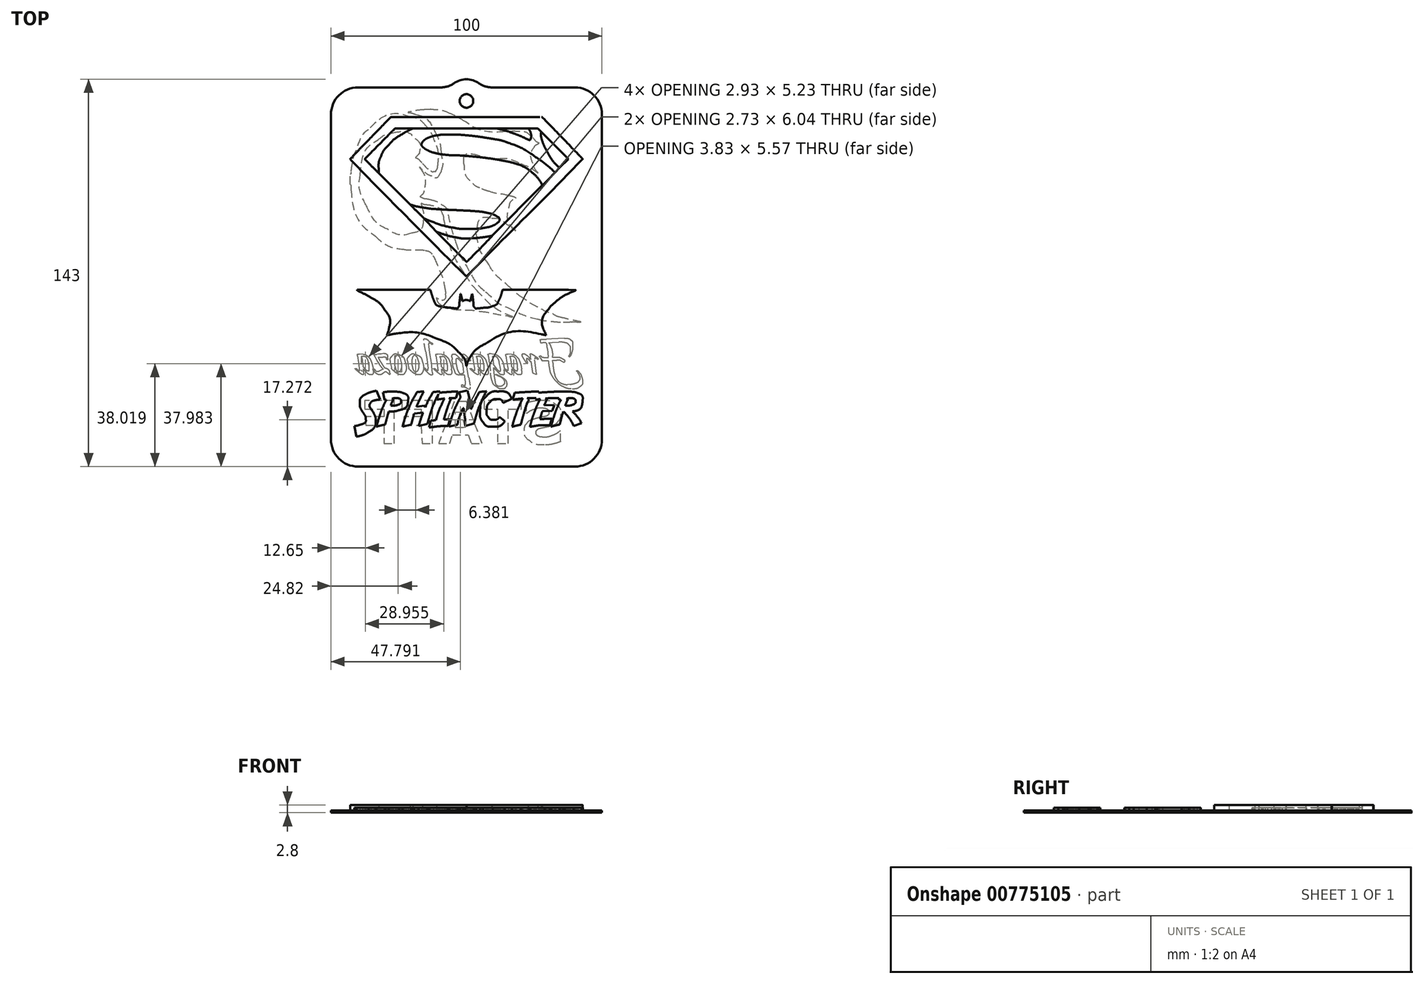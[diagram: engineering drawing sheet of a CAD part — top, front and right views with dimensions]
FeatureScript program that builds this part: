
annotation { "Feature Type Name" : "Feature", "Feature Type Description" : "" }
export const myFeature = defineFeature(function(context is Context, id is Id, definition is map)
    precondition{}
    {
        {
            var Q0;
            Q0=qCreatedBy(makeId("Top.planeOp"),FACE);
            var sketch = newSketch(context, id + "F0", { "sketchPlane" : qUnion([Q0])});
            skLineSegment(sketch, "E0.bottom", {"start": v(-40, 70) * mm, "end": v(-9.33, 70) * mm});
            skLineSegment(sketch, "E0.top", {"start": v(-40, -70) * mm, "end": v(40, -70) * mm});
            skLineSegment(sketch, "E0.left", {"start": v(-50, 60) * mm, "end": v(-50, -60) * mm});
            skLineSegment(sketch, "E0.right", {"start": v(50, 60) * mm, "end": v(50, -60) * mm});
            skPoint(sketch, "E0.middle", {"position": v(0, 0) * mm});
            skCircle(sketch, "E1", {"center": v(0, 65) * mm, "radius": 2.5 * mm});
            skPoint(sketch, "E2.visualSharp", {"position": v(-50, 70) * mm});
            skArc(sketch, "E2.filletArc", {"start": v(-40, 70) * mm, "mid": v(-47.07, 67.07) * mm, "end": v(-50, 60) * mm});
            skPoint(sketch, "E3.visualSharp", {"position": v(50, 70) * mm});
            skArc(sketch, "E3.filletArc", {"start": v(50, 60) * mm, "mid": v(47.07, 67.07) * mm, "end": v(40, 70) * mm});
            skPoint(sketch, "E4.visualSharp", {"position": v(50, -70) * mm});
            skArc(sketch, "E4.filletArc", {"start": v(40, -70) * mm, "mid": v(47.07, -67.07) * mm, "end": v(50, -60) * mm});
            skPoint(sketch, "E5.visualSharp", {"position": v(-50, -70) * mm});
            skArc(sketch, "E5.filletArc", {"start": v(-50, -60) * mm, "mid": v(-47.07, -67.07) * mm, "end": v(-40, -70) * mm});
            skArc(sketch, "E6", {"start": v(-4.66, 71.5) * mm, "mid": v(0, 73) * mm, "end": v(4.66, 71.5) * mm});
            skArc(sketch, "E7.filletArc", {"start": v(-9.33, 70) * mm, "mid": v(-6.88, 70.38) * mm, "end": v(-4.66, 71.5) * mm});
            skLineSegment(sketch, "E8", {"start": v(40, 70) * mm, "end": v(9.33, 70) * mm});
            skArc(sketch, "E9.filletArc", {"start": v(4.66, 71.5) * mm, "mid": v(6.88, 70.38) * mm, "end": v(9.33, 70) * mm});
            skSolve(sketch);
        }
        {
            var Q0;
            Q0=qCreatedBy(makeId("Top.planeOp"),FACE);
            var sketch = newSketch(context, id + "F1", { "sketchPlane" : qUnion([Q0])});
            skLineSegment(sketch, "E10", {"start": v(38.17, -16.7) * mm, "end": v(38.78, -16.7) * mm});
            skLineSegment(sketch, "E11", {"start": v(-13.07, 61.96) * mm, "end": v(-13.17, 61.96) * mm});
            skLineSegment(sketch, "E12", {"start": v(-14.17, 61.96) * mm, "end": v(-14.37, 61.96) * mm});
            skLineSegment(sketch, "E13", {"start": v(-42.85, 37.93) * mm, "end": v(-42.85, 36.81) * mm});
            skLineSegment(sketch, "E14", {"start": v(-42.85, 35.49) * mm, "end": v(-42.85, 34.98) * mm});
            skLineSegment(sketch, "E15", {"start": v(-42.85, 34.78) * mm, "end": v(-42.85, 34.16) * mm});
            skLineSegment(sketch, "E16", {"start": v(40.64, -16.7) * mm, "end": v(40.63, -16.62) * mm});
            skLineSegment(sketch, "E17", {"start": v(38.83, -16.7) * mm, "end": v(40.64, -16.7) * mm});
            skLineSegment(sketch, "E18", {"start": v(-42.85, 36.81) * mm, "end": v(-42.85, 35.49) * mm});
            skLineSegment(sketch, "E19", {"start": v(-13.21, 61.96) * mm, "end": v(-14.22, 61.96) * mm});
            skLineSegment(sketch, "E20", {"start": v(-42.85, 34.98) * mm, "end": v(-42.85, 34.77) * mm});
            skLineSegment(sketch, "E21", {"start": v(36.03, -31.52) * mm, "end": v(35.01, -30.98) * mm});
            skLineSegment(sketch, "E22", {"start": v(33.37, -30.7) * mm, "end": v(32.17, -30.75) * mm});
            skLineSegment(sketch, "E23", {"start": v(32.17, -30.75) * mm, "end": v(30.92, -30.82) * mm});
            skLineSegment(sketch, "E24", {"start": v(30.92, -30.82) * mm, "end": v(27.9, -30.82) * mm});
            skLineSegment(sketch, "E25", {"start": v(27.9, -30.82) * mm, "end": v(27.52, -30.26) * mm});
            skLineSegment(sketch, "E26", {"start": v(26.88, -29.35) * mm, "end": v(26.9, -29.28) * mm});
            skLineSegment(sketch, "E27", {"start": v(30.32, -29.76) * mm, "end": v(31.57, -29.76) * mm});
            skLineSegment(sketch, "E28", {"start": v(31.57, -29.76) * mm, "end": v(33.15, -29.76) * mm});
            skLineSegment(sketch, "E29", {"start": v(33.15, -29.76) * mm, "end": v(34.41, -29.76) * mm});
            skLineSegment(sketch, "E30", {"start": v(34.05, -24.06) * mm, "end": v(31.6, -24.16) * mm});
            skLineSegment(sketch, "E31", {"start": v(31.6, -24.16) * mm, "end": v(29.36, -24.3) * mm});
            skLineSegment(sketch, "E32", {"start": v(27.3, -24.39) * mm, "end": v(27.09, -23.13) * mm});
            skLineSegment(sketch, "E33", {"start": v(29.45, -22.97) * mm, "end": v(31.35, -22.93) * mm});
            skLineSegment(sketch, "E34", {"start": v(31.35, -22.93) * mm, "end": v(33.78, -22.78) * mm});
            skLineSegment(sketch, "E35", {"start": v(33.78, -22.78) * mm, "end": v(36.14, -22.66) * mm});
            skLineSegment(sketch, "E36", {"start": v(38.04, -29.5) * mm, "end": v(37.7, -29.32) * mm});
            skLineSegment(sketch, "E37", {"start": v(30.25, -30.2) * mm, "end": v(29.88, -26.54) * mm});
            skLineSegment(sketch, "E38", {"start": v(29.55, -24.56) * mm, "end": v(29.3, -24.3) * mm});
            skLineSegment(sketch, "E39", {"start": v(29.18, -23.96) * mm, "end": v(29.55, -24.04) * mm});
            skLineSegment(sketch, "E40", {"start": v(31.76, -29.06) * mm, "end": v(31.88, -31.82) * mm});
            skLineSegment(sketch, "E41", {"start": v(37.27, -39.71) * mm, "end": v(38.3, -39.63) * mm});
            skLineSegment(sketch, "E42", {"start": v(41.15, -35.4) * mm, "end": v(40.78, -34.92) * mm});
            skLineSegment(sketch, "E43", {"start": v(40.78, -34.92) * mm, "end": v(40.72, -34.76) * mm});
            skLineSegment(sketch, "E44", {"start": v(23.56, -29.53) * mm, "end": v(23.5, -28.89) * mm});
            skLineSegment(sketch, "E45", {"start": v(24.23, -28.54) * mm, "end": v(25.22, -29.23) * mm});
            skLineSegment(sketch, "E46", {"start": v(25.22, -29.23) * mm, "end": v(26.33, -30.01) * mm});
            skLineSegment(sketch, "E47", {"start": v(26.48, -30.3) * mm, "end": v(26.4, -30.34) * mm});
            skLineSegment(sketch, "E48", {"start": v(26.4, -30.34) * mm, "end": v(26.3, -30.32) * mm});
            skLineSegment(sketch, "E49", {"start": v(26.3, -30.32) * mm, "end": v(26.17, -30.3) * mm});
            skLineSegment(sketch, "E50", {"start": v(25.15, -30.3) * mm, "end": v(25.53, -33.54) * mm});
            skLineSegment(sketch, "E51", {"start": v(25.53, -33.54) * mm, "end": v(25.79, -35.64) * mm});
            skLineSegment(sketch, "E52", {"start": v(25.88, -36) * mm, "end": v(24.4, -35.44) * mm});
            skLineSegment(sketch, "E53", {"start": v(23.19, -29.85) * mm, "end": v(23.89, -30.75) * mm});
            skLineSegment(sketch, "E54", {"start": v(23.65, -31.18) * mm, "end": v(23.19, -30.77) * mm});
            skLineSegment(sketch, "E55", {"start": v(15.9, -29.4) * mm, "end": v(15.4, -29.4) * mm});
            skLineSegment(sketch, "E56", {"start": v(15.4, -29.4) * mm, "end": v(15.02, -29.33) * mm});
            skLineSegment(sketch, "E57", {"start": v(15.24, -28.42) * mm, "end": v(16.71, -28.55) * mm});
            skLineSegment(sketch, "E58", {"start": v(17.3, -34.56) * mm, "end": v(16.63, -33.84) * mm});
            skLineSegment(sketch, "E59", {"start": v(16.01, -32.3) * mm, "end": v(16.46, -32.84) * mm});
            skLineSegment(sketch, "E60", {"start": v(16.96, -29.4) * mm, "end": v(16.5, -29.4) * mm});
            skLineSegment(sketch, "E61", {"start": v(16.5, -29.4) * mm, "end": v(15.9, -29.4) * mm});
            skLineSegment(sketch, "E62", {"start": v(16.38, -31.1) * mm, "end": v(16.6, -32.79) * mm});
            skLineSegment(sketch, "E63", {"start": v(16.6, -32.79) * mm, "end": v(16.8, -34.4) * mm});
            skLineSegment(sketch, "E64", {"start": v(16.8, -34.4) * mm, "end": v(16.85, -35.3) * mm});
            skLineSegment(sketch, "E65", {"start": v(14.85, -34.45) * mm, "end": v(15.26, -34.75) * mm});
            skLineSegment(sketch, "E66", {"start": v(15.33, -34.51) * mm, "end": v(15.26, -33.72) * mm});
            skLineSegment(sketch, "E67", {"start": v(15.26, -33.72) * mm, "end": v(14.93, -31.64) * mm});
            skLineSegment(sketch, "E68", {"start": v(14.93, -31.64) * mm, "end": v(14.54, -29.14) * mm});
            skLineSegment(sketch, "E69", {"start": v(9.13, -29.4) * mm, "end": v(8.63, -29.4) * mm});
            skLineSegment(sketch, "E70", {"start": v(8.63, -29.4) * mm, "end": v(8.27, -29.31) * mm});
            skLineSegment(sketch, "E71", {"start": v(8.04, -29.08) * mm, "end": v(7.89, -28.74) * mm});
            skLineSegment(sketch, "E72", {"start": v(8.47, -28.35) * mm, "end": v(8.95, -28.35) * mm});
            skLineSegment(sketch, "E73", {"start": v(8.95, -28.35) * mm, "end": v(9.46, -28.52) * mm});
            skLineSegment(sketch, "E74", {"start": v(9.46, -28.52) * mm, "end": v(10.14, -28.6) * mm});
            skLineSegment(sketch, "E75", {"start": v(11.28, -34.74) * mm, "end": v(10.47, -33.88) * mm});
            skLineSegment(sketch, "E76", {"start": v(9.69, -32.05) * mm, "end": v(10.37, -32.95) * mm});
            skLineSegment(sketch, "E77", {"start": v(10.37, -32.95) * mm, "end": v(11.14, -33.94) * mm});
            skLineSegment(sketch, "E78", {"start": v(12.6, -34.13) * mm, "end": v(12.52, -33.32) * mm});
            skLineSegment(sketch, "E79", {"start": v(12.52, -33.32) * mm, "end": v(12.29, -32.26) * mm});
            skLineSegment(sketch, "E80", {"start": v(12.29, -32.26) * mm, "end": v(12.13, -31.6) * mm});
            skLineSegment(sketch, "E81", {"start": v(10.33, -29.4) * mm, "end": v(9.77, -29.4) * mm});
            skLineSegment(sketch, "E82", {"start": v(9.77, -29.4) * mm, "end": v(9.13, -29.4) * mm});
            skLineSegment(sketch, "E83", {"start": v(9.46, -28.84) * mm, "end": v(9.77, -30.97) * mm});
            skLineSegment(sketch, "E84", {"start": v(9.77, -30.97) * mm, "end": v(10.1, -34.04) * mm});
            skLineSegment(sketch, "E85", {"start": v(10.1, -34.04) * mm, "end": v(10.34, -36.29) * mm});
            skLineSegment(sketch, "E86", {"start": v(10.34, -36.29) * mm, "end": v(10.47, -37.68) * mm});
            skLineSegment(sketch, "E87", {"start": v(12.25, -36.7) * mm, "end": v(11.22, -36.28) * mm});
            skLineSegment(sketch, "E88", {"start": v(10.66, -36) * mm, "end": v(10.7, -35.94) * mm});
            skLineSegment(sketch, "E89", {"start": v(8.88, -35.3) * mm, "end": v(8.5, -31.75) * mm});
            skLineSegment(sketch, "E90", {"start": v(3.54, -29.4) * mm, "end": v(3.04, -29.4) * mm});
            skLineSegment(sketch, "E91", {"start": v(3.04, -29.4) * mm, "end": v(2.67, -29.33) * mm});
            skLineSegment(sketch, "E92", {"start": v(2.88, -28.42) * mm, "end": v(4.36, -28.55) * mm});
            skLineSegment(sketch, "E93", {"start": v(4.94, -34.56) * mm, "end": v(4.28, -33.84) * mm});
            skLineSegment(sketch, "E94", {"start": v(3.66, -32.3) * mm, "end": v(4.1, -32.84) * mm});
            skLineSegment(sketch, "E95", {"start": v(4.6, -29.4) * mm, "end": v(4.14, -29.4) * mm});
            skLineSegment(sketch, "E96", {"start": v(4.14, -29.4) * mm, "end": v(3.54, -29.4) * mm});
            skLineSegment(sketch, "E97", {"start": v(4.02, -31.1) * mm, "end": v(4.25, -32.79) * mm});
            skLineSegment(sketch, "E98", {"start": v(4.25, -32.79) * mm, "end": v(4.44, -34.4) * mm});
            skLineSegment(sketch, "E99", {"start": v(4.44, -34.4) * mm, "end": v(4.5, -35.3) * mm});
            skLineSegment(sketch, "E100", {"start": v(2.5, -34.45) * mm, "end": v(2.9, -34.75) * mm});
            skLineSegment(sketch, "E101", {"start": v(2.98, -34.51) * mm, "end": v(2.9, -33.72) * mm});
            skLineSegment(sketch, "E102", {"start": v(2.9, -33.72) * mm, "end": v(2.58, -31.64) * mm});
            skLineSegment(sketch, "E103", {"start": v(2.58, -31.64) * mm, "end": v(2.19, -29.14) * mm});
            skLineSegment(sketch, "E104", {"start": v(-0.07, -30.77) * mm, "end": v(0.03, -32.01) * mm});
            skLineSegment(sketch, "E105", {"start": v(0.03, -32.01) * mm, "end": v(0.35, -34.14) * mm});
            skLineSegment(sketch, "E106", {"start": v(0.35, -34.14) * mm, "end": v(0.85, -37.11) * mm});
            skLineSegment(sketch, "E107", {"start": v(0.96, -41.4) * mm, "end": v(0.32, -41.16) * mm});
            skLineSegment(sketch, "E108", {"start": v(-0.43, -39.67) * mm, "end": v(-0.47, -38.83) * mm});
            skLineSegment(sketch, "E109", {"start": v(-0.47, -38.83) * mm, "end": v(-0.77, -36.7) * mm});
            skLineSegment(sketch, "E110", {"start": v(-0.77, -36.7) * mm, "end": v(-1.14, -33.74) * mm});
            skLineSegment(sketch, "E111", {"start": v(-1.14, -33.74) * mm, "end": v(-1.34, -32.16) * mm});
            skLineSegment(sketch, "E112", {"start": v(-1.34, -32.16) * mm, "end": v(-1.56, -30.34) * mm});
            skLineSegment(sketch, "E113", {"start": v(-1.56, -30.34) * mm, "end": v(-1.62, -29.37) * mm});
            skLineSegment(sketch, "E114", {"start": v(-0.41, -35.45) * mm, "end": v(-0.36, -35.65) * mm});
            skLineSegment(sketch, "E115", {"start": v(-0.18, -36.1) * mm, "end": v(-0.24, -36.16) * mm});
            skLineSegment(sketch, "E116", {"start": v(-0.24, -36.16) * mm, "end": v(-0.31, -36.19) * mm});
            skLineSegment(sketch, "E117", {"start": v(-0.31, -36.19) * mm, "end": v(-0.7, -36.11) * mm});
            skLineSegment(sketch, "E118", {"start": v(-0.7, -36.11) * mm, "end": v(-1.4, -36.11) * mm});
            skLineSegment(sketch, "E119", {"start": v(-1.4, -36.11) * mm, "end": v(-2.27, -36.11) * mm});
            skLineSegment(sketch, "E120", {"start": v(-2.53, -30.03) * mm, "end": v(-1.85, -30.67) * mm});
            skLineSegment(sketch, "E121", {"start": v(-9.94, -29.4) * mm, "end": v(-10.44, -29.4) * mm});
            skLineSegment(sketch, "E122", {"start": v(-10.44, -29.4) * mm, "end": v(-10.8, -29.33) * mm});
            skLineSegment(sketch, "E123", {"start": v(-10.6, -28.42) * mm, "end": v(-9.12, -28.55) * mm});
            skLineSegment(sketch, "E124", {"start": v(-8.54, -34.56) * mm, "end": v(-9.2, -33.84) * mm});
            skLineSegment(sketch, "E125", {"start": v(-9.82, -32.3) * mm, "end": v(-9.37, -32.84) * mm});
            skLineSegment(sketch, "E126", {"start": v(-8.87, -29.4) * mm, "end": v(-9.34, -29.4) * mm});
            skLineSegment(sketch, "E127", {"start": v(-9.34, -29.4) * mm, "end": v(-9.94, -29.4) * mm});
            skLineSegment(sketch, "E128", {"start": v(-9.46, -31.1) * mm, "end": v(-9.23, -32.79) * mm});
            skLineSegment(sketch, "E129", {"start": v(-9.23, -32.79) * mm, "end": v(-9.04, -34.4) * mm});
            skLineSegment(sketch, "E130", {"start": v(-9.04, -34.4) * mm, "end": v(-8.99, -35.3) * mm});
            skLineSegment(sketch, "E131", {"start": v(-10.98, -34.45) * mm, "end": v(-10.58, -34.75) * mm});
            skLineSegment(sketch, "E132", {"start": v(-10.5, -34.51) * mm, "end": v(-10.58, -33.72) * mm});
            skLineSegment(sketch, "E133", {"start": v(-10.58, -33.72) * mm, "end": v(-10.9, -31.64) * mm});
            skLineSegment(sketch, "E134", {"start": v(-10.9, -31.64) * mm, "end": v(-11.29, -29.14) * mm});
            skLineSegment(sketch, "E135", {"start": v(-14.16, -33.74) * mm, "end": v(-14.26, -32.52) * mm});
            skLineSegment(sketch, "E136", {"start": v(-14.26, -32.52) * mm, "end": v(-14.56, -30.46) * mm});
            skLineSegment(sketch, "E137", {"start": v(-14.56, -30.46) * mm, "end": v(-15.08, -27.43) * mm});
            skLineSegment(sketch, "E138", {"start": v(-15, -22.92) * mm, "end": v(-14.03, -23.56) * mm});
            skLineSegment(sketch, "E139", {"start": v(-12.63, -24.87) * mm, "end": v(-12.86, -24.8) * mm});
            skLineSegment(sketch, "E140", {"start": v(-13.91, -24.76) * mm, "end": v(-13.85, -25.5) * mm});
            skLineSegment(sketch, "E141", {"start": v(-13.85, -25.5) * mm, "end": v(-13.65, -26.9) * mm});
            skLineSegment(sketch, "E142", {"start": v(-13.65, -26.9) * mm, "end": v(-13.36, -28.73) * mm});
            skLineSegment(sketch, "E143", {"start": v(-13.36, -28.73) * mm, "end": v(-13.08, -30.79) * mm});
            skLineSegment(sketch, "E144", {"start": v(-13.08, -30.79) * mm, "end": v(-12.8, -32.84) * mm});
            skLineSegment(sketch, "E145", {"start": v(-12.8, -32.84) * mm, "end": v(-12.61, -34.45) * mm});
            skLineSegment(sketch, "E146", {"start": v(-12.61, -34.45) * mm, "end": v(-12.55, -35.39) * mm});
            skLineSegment(sketch, "E147", {"start": v(-19.13, -35.54) * mm, "end": v(-20.12, -34.9) * mm});
            skLineSegment(sketch, "E148", {"start": v(-21.26, -33.55) * mm, "end": v(-21.5, -32.5) * mm});
            skLineSegment(sketch, "E149", {"start": v(-21.5, -32.5) * mm, "end": v(-21.73, -31.52) * mm});
            skLineSegment(sketch, "E150", {"start": v(-21.73, -31.52) * mm, "end": v(-21.79, -30.84) * mm});
            skLineSegment(sketch, "E151", {"start": v(-19.8, -28.37) * mm, "end": v(-19.36, -28.42) * mm});
            skLineSegment(sketch, "E152", {"start": v(-19.36, -28.42) * mm, "end": v(-18.37, -28.75) * mm});
            skLineSegment(sketch, "E153", {"start": v(-17.54, -31.66) * mm, "end": v(-18, -30.05) * mm});
            skLineSegment(sketch, "E154", {"start": v(-25.5, -35.54) * mm, "end": v(-26.5, -34.9) * mm});
            skLineSegment(sketch, "E155", {"start": v(-27.64, -33.55) * mm, "end": v(-27.88, -32.5) * mm});
            skLineSegment(sketch, "E156", {"start": v(-27.88, -32.5) * mm, "end": v(-28.1, -31.52) * mm});
            skLineSegment(sketch, "E157", {"start": v(-28.1, -31.52) * mm, "end": v(-28.17, -30.84) * mm});
            skLineSegment(sketch, "E158", {"start": v(-26.19, -28.37) * mm, "end": v(-25.74, -28.42) * mm});
            skLineSegment(sketch, "E159", {"start": v(-25.74, -28.42) * mm, "end": v(-24.75, -28.75) * mm});
            skLineSegment(sketch, "E160", {"start": v(-23.92, -31.66) * mm, "end": v(-24.38, -30.05) * mm});
            skLineSegment(sketch, "E161", {"start": v(-30.82, -29.63) * mm, "end": v(-31.6, -29.66) * mm});
            skLineSegment(sketch, "E162", {"start": v(-31.6, -29.66) * mm, "end": v(-32.28, -29.63) * mm});
            skLineSegment(sketch, "E163", {"start": v(-32.28, -29.63) * mm, "end": v(-32.6, -29.59) * mm});
            skLineSegment(sketch, "E164", {"start": v(-28.05, -35.7) * mm, "end": v(-28.34, -36) * mm});
            skLineSegment(sketch, "E165", {"start": v(-32.16, -32.19) * mm, "end": v(-32.67, -31.4) * mm});
            skLineSegment(sketch, "E166", {"start": v(-32.67, -31.4) * mm, "end": v(-33.23, -30.44) * mm});
            skLineSegment(sketch, "E167", {"start": v(-33.23, -30.44) * mm, "end": v(-33.8, -29.45) * mm});
            skLineSegment(sketch, "E168", {"start": v(-33.8, -29.45) * mm, "end": v(-34.28, -28.64) * mm});
            skLineSegment(sketch, "E169", {"start": v(-34.18, -28.33) * mm, "end": v(-34.02, -28.38) * mm});
            skLineSegment(sketch, "E170", {"start": v(-33.17, -28.56) * mm, "end": v(-32.43, -28.52) * mm});
            skLineSegment(sketch, "E171", {"start": v(-32.43, -28.52) * mm, "end": v(-31.52, -28.4) * mm});
            skLineSegment(sketch, "E172", {"start": v(-31.52, -28.4) * mm, "end": v(-30.4, -28.23) * mm});
            skLineSegment(sketch, "E173", {"start": v(-29.1, -29.33) * mm, "end": v(-29.02, -30) * mm});
            skLineSegment(sketch, "E174", {"start": v(-28.09, -35.68) * mm, "end": v(-28.22, -35.85) * mm});
            skLineSegment(sketch, "E175", {"start": v(-28.4, -35.95) * mm, "end": v(-29.27, -35.27) * mm});
            skLineSegment(sketch, "E176", {"start": v(-32.12, -34.67) * mm, "end": v(-31.13, -34.22) * mm});
            skLineSegment(sketch, "E177", {"start": v(-31.13, -34.22) * mm, "end": v(-30.22, -33.8) * mm});
            skLineSegment(sketch, "E178", {"start": v(-28.36, -35.08) * mm, "end": v(-28.32, -35.29) * mm});
            skLineSegment(sketch, "E179", {"start": v(-28.32, -35.29) * mm, "end": v(-28.26, -35.48) * mm});
            skLineSegment(sketch, "E180", {"start": v(-28.26, -35.48) * mm, "end": v(-28.09, -35.68) * mm});
            skLineSegment(sketch, "E181", {"start": v(-38.9, -29.4) * mm, "end": v(-39.4, -29.4) * mm});
            skLineSegment(sketch, "E182", {"start": v(-39.4, -29.4) * mm, "end": v(-39.76, -29.33) * mm});
            skLineSegment(sketch, "E183", {"start": v(-39.55, -28.42) * mm, "end": v(-38.08, -28.55) * mm});
            skLineSegment(sketch, "E184", {"start": v(-37.5, -34.56) * mm, "end": v(-38.15, -33.84) * mm});
            skLineSegment(sketch, "E185", {"start": v(-38.77, -32.3) * mm, "end": v(-38.33, -32.84) * mm});
            skLineSegment(sketch, "E186", {"start": v(-37.82, -29.4) * mm, "end": v(-38.3, -29.4) * mm});
            skLineSegment(sketch, "E187", {"start": v(-38.3, -29.4) * mm, "end": v(-38.9, -29.4) * mm});
            skLineSegment(sketch, "E188", {"start": v(-38.41, -31.1) * mm, "end": v(-38.19, -32.79) * mm});
            skLineSegment(sketch, "E189", {"start": v(-38.19, -32.79) * mm, "end": v(-38, -34.4) * mm});
            skLineSegment(sketch, "E190", {"start": v(-38, -34.4) * mm, "end": v(-37.94, -35.3) * mm});
            skLineSegment(sketch, "E191", {"start": v(-39.94, -34.45) * mm, "end": v(-39.53, -34.75) * mm});
            skLineSegment(sketch, "E192", {"start": v(-39.45, -34.51) * mm, "end": v(-39.53, -33.72) * mm});
            skLineSegment(sketch, "E193", {"start": v(-39.53, -33.72) * mm, "end": v(-39.86, -31.64) * mm});
            skLineSegment(sketch, "E194", {"start": v(-39.86, -31.64) * mm, "end": v(-40.24, -29.14) * mm});
            skLineSegment(sketch, "E195", {"start": v(22.49, -50.22) * mm, "end": v(22.06, -50.22) * mm});
            skLineSegment(sketch, "E196", {"start": v(22.06, -50.22) * mm, "end": v(22.06, -46.56) * mm});
            skLineSegment(sketch, "E197", {"start": v(34.32, -56.92) * mm, "end": v(34.76, -56.92) * mm});
            skLineSegment(sketch, "E198", {"start": v(34.76, -56.92) * mm, "end": v(34.76, -60.73) * mm});
            skLineSegment(sketch, "E199", {"start": v(6.54, -45.64) * mm, "end": v(20.3, -45.64) * mm});
            skLineSegment(sketch, "E200", {"start": v(20.3, -45.64) * mm, "end": v(20.3, -48.81) * mm});
            skLineSegment(sketch, "E201", {"start": v(20.3, -48.81) * mm, "end": v(15.36, -48.81) * mm});
            skLineSegment(sketch, "E202", {"start": v(15.36, -48.81) * mm, "end": v(15.36, -61.51) * mm});
            skLineSegment(sketch, "E203", {"start": v(15.36, -61.51) * mm, "end": v(11.47, -61.51) * mm});
            skLineSegment(sketch, "E204", {"start": v(11.47, -61.51) * mm, "end": v(11.47, -48.81) * mm});
            skLineSegment(sketch, "E205", {"start": v(11.47, -48.81) * mm, "end": v(6.54, -48.81) * mm});
            skLineSegment(sketch, "E206", {"start": v(6.54, -48.81) * mm, "end": v(6.54, -45.64) * mm});
            skLineSegment(sketch, "E207", {"start": v(-4.56, -45.99) * mm, "end": v(0.04, -45.99) * mm});
            skLineSegment(sketch, "E208", {"start": v(0.04, -45.99) * mm, "end": v(5.78, -61.51) * mm});
            skLineSegment(sketch, "E209", {"start": v(5.78, -61.51) * mm, "end": v(1.8, -61.51) * mm});
            skLineSegment(sketch, "E210", {"start": v(1.8, -61.51) * mm, "end": v(0.7, -58.34) * mm});
            skLineSegment(sketch, "E211", {"start": v(0.7, -58.34) * mm, "end": v(-5.12, -58.34) * mm});
            skLineSegment(sketch, "E212", {"start": v(-5.12, -58.34) * mm, "end": v(-6.2, -61.51) * mm});
            skLineSegment(sketch, "E213", {"start": v(-6.2, -61.51) * mm, "end": v(-10.3, -61.51) * mm});
            skLineSegment(sketch, "E214", {"start": v(-10.3, -61.51) * mm, "end": v(-4.56, -45.99) * mm});
            skLineSegment(sketch, "E215", {"start": v(-0.3, -55.51) * mm, "end": v(-2.2, -49.94) * mm});
            skLineSegment(sketch, "E216", {"start": v(-2.2, -49.94) * mm, "end": v(-4.12, -55.51) * mm});
            skLineSegment(sketch, "E217", {"start": v(-4.12, -55.51) * mm, "end": v(-0.3, -55.51) * mm});
            skLineSegment(sketch, "E218", {"start": v(-23.8, -45.64) * mm, "end": v(-12.51, -45.64) * mm});
            skLineSegment(sketch, "E219", {"start": v(-12.51, -45.64) * mm, "end": v(-12.51, -61.51) * mm});
            skLineSegment(sketch, "E220", {"start": v(-12.51, -61.51) * mm, "end": v(-16.4, -61.51) * mm});
            skLineSegment(sketch, "E221", {"start": v(-16.4, -61.51) * mm, "end": v(-16.75, -54.8) * mm});
            skLineSegment(sketch, "E222", {"start": v(-16.75, -54.8) * mm, "end": v(-23.1, -54.8) * mm});
            skLineSegment(sketch, "E223", {"start": v(-23.1, -54.8) * mm, "end": v(-23.1, -51.63) * mm});
            skLineSegment(sketch, "E224", {"start": v(-23.1, -51.63) * mm, "end": v(-16.75, -51.63) * mm});
            skLineSegment(sketch, "E225", {"start": v(-16.75, -51.63) * mm, "end": v(-16.75, -48.81) * mm});
            skLineSegment(sketch, "E226", {"start": v(-16.75, -48.81) * mm, "end": v(-23.8, -48.81) * mm});
            skLineSegment(sketch, "E227", {"start": v(-23.8, -48.81) * mm, "end": v(-23.8, -45.64) * mm});
            skLineSegment(sketch, "E228", {"start": v(-37.56, -45.64) * mm, "end": v(-26.63, -45.64) * mm});
            skLineSegment(sketch, "E229", {"start": v(-26.63, -45.64) * mm, "end": v(-26.63, -61.51) * mm});
            skLineSegment(sketch, "E230", {"start": v(-26.63, -61.51) * mm, "end": v(-30.5, -61.51) * mm});
            skLineSegment(sketch, "E231", {"start": v(-30.5, -61.51) * mm, "end": v(-30.5, -54.8) * mm});
            skLineSegment(sketch, "E232", {"start": v(-30.5, -54.8) * mm, "end": v(-37.2, -54.8) * mm});
            skLineSegment(sketch, "E233", {"start": v(-37.2, -54.8) * mm, "end": v(-37.2, -51.63) * mm});
            skLineSegment(sketch, "E234", {"start": v(-37.2, -51.63) * mm, "end": v(-30.5, -51.63) * mm});
            skLineSegment(sketch, "E235", {"start": v(-30.5, -51.63) * mm, "end": v(-30.5, -48.81) * mm});
            skLineSegment(sketch, "E236", {"start": v(-30.5, -48.81) * mm, "end": v(-37.56, -48.81) * mm});
            skLineSegment(sketch, "E237", {"start": v(-37.56, -48.81) * mm, "end": v(-37.56, -45.64) * mm});
            skFitSpline(sketch, "E238", {"points": [v(-14.37, 61.96) * mm, v(-14.8, 61.78) * mm, v(-15.26, 61.8) * mm, v(-15.71, 61.76) * mm]});
            skFitSpline(sketch, "E239", {"points": [v(-15.71, 61.76) * mm, v(-17.53, 61.62) * mm, v(-19.32, 61.38) * mm, v(-21.1, 60.93) * mm]});
            skFitSpline(sketch, "E240", {"points": [v(-21.1, 60.93) * mm, v(-21.24, 60.9) * mm, v(-21.43, 60.9) * mm, v(-21.54, 60.66) * mm]});
            skFitSpline(sketch, "E241", {"points": [v(-21.54, 60.66) * mm, v(-20.54, 60.63) * mm, v(-19.62, 60.35) * mm, v(-18.7, 60.03) * mm]});
            skFitSpline(sketch, "E242", {"points": [v(-18.7, 60.03) * mm, v(-15.38, 58.87) * mm, v(-13.15, 56.52) * mm, v(-11.58, 53.44) * mm]});
            skFitSpline(sketch, "E243", {"points": [v(-11.58, 53.44) * mm, v(-10.47, 51.29) * mm, v(-9.71, 49) * mm, v(-9.41, 46.6) * mm]});
            skFitSpline(sketch, "E244", {"points": [v(-9.41, 46.6) * mm, v(-9.11, 44.15) * mm, v(-8.77, 41.68) * mm, v(-9.35, 39.2) * mm]});
            skFitSpline(sketch, "E245", {"points": [v(-9.35, 39.2) * mm, v(-9.4, 38.94) * mm, v(-9.5, 38.7) * mm, v(-9.63, 38.47) * mm]});
            skFitSpline(sketch, "E246", {"points": [v(-9.63, 38.47) * mm, v(-10.22, 37.39) * mm, v(-11.1, 36.57) * mm, v(-12.72, 37.2) * mm]});
            skFitSpline(sketch, "E247", {"points": [v(-12.72, 37.2) * mm, v(-14.12, 37.75) * mm, v(-15.28, 38.64) * mm, v(-16.36, 39.65) * mm]});
            skFitSpline(sketch, "E248", {"points": [v(-16.36, 39.65) * mm, v(-16.66, 39.92) * mm, v(-16.91, 40.23) * mm, v(-17.25, 40.59) * mm]});
            skFitSpline(sketch, "E249", {"points": [v(-17.25, 40.59) * mm, v(-17.26, 40.3) * mm, v(-17.11, 40.19) * mm, v(-17.03, 40.05) * mm]});
            skFitSpline(sketch, "E250", {"points": [v(-17.03, 40.05) * mm, v(-15.47, 37.53) * mm, v(-15.17, 34.78) * mm, v(-15.68, 31.91) * mm]});
            skFitSpline(sketch, "E251", {"points": [v(-15.68, 31.91) * mm, v(-15.8, 31.24) * mm, v(-16.1, 30.64) * mm, v(-16.6, 30.16) * mm]});
            skFitSpline(sketch, "E252", {"points": [v(-16.6, 30.16) * mm, v(-17.12, 29.67) * mm, v(-17.1, 29.65) * mm, v(-16.44, 29.37) * mm]});
            skFitSpline(sketch, "E253", {"points": [v(-16.44, 29.37) * mm, v(-15.51, 28.97) * mm, v(-14.51, 28.87) * mm, v(-13.54, 28.62) * mm]});
            skFitSpline(sketch, "E254", {"points": [v(-13.54, 28.62) * mm, v(-11.87, 28.2) * mm, v(-10.3, 27.56) * mm, v(-8.86, 26.56) * mm]});
            skFitSpline(sketch, "E255", {"points": [v(-8.86, 26.56) * mm, v(-7.66, 25.72) * mm, v(-7.05, 24.5) * mm, v(-6.77, 23.12) * mm]});
            skFitSpline(sketch, "E256", {"points": [v(-6.77, 23.12) * mm, v(-6.07, 19.68) * mm, v(-5.15, 16.3) * mm, v(-4.03, 13) * mm]});
            skFitSpline(sketch, "E257", {"points": [v(-4.03, 13) * mm, v(-3.06, 10.12) * mm, v(-1.94, 7.3) * mm, v(-0.43, 4.69) * mm]});
            skFitSpline(sketch, "E258", {"points": [v(-0.43, 4.69) * mm, v(1.68, 1.04) * mm, v(3.89, -2.54) * mm, v(7.02, -5.42) * mm]});
            skFitSpline(sketch, "E259", {"points": [v(7.02, -5.42) * mm, v(9.48, -7.68) * mm, v(12.02, -9.8) * mm, v(15.04, -11.25) * mm]});
            skFitSpline(sketch, "E260", {"points": [v(15.04, -11.25) * mm, v(18.76, -13.03) * mm, v(22.58, -14.59) * mm, v(26.59, -15.61) * mm]});
            skFitSpline(sketch, "E261", {"points": [v(26.59, -15.61) * mm, v(28.25, -16.04) * mm, v(29.96, -16.23) * mm, v(31.67, -16.4) * mm]});
            skFitSpline(sketch, "E262", {"points": [v(31.67, -16.4) * mm, v(33.03, -16.54) * mm, v(34.4, -16.62) * mm, v(35.77, -16.62) * mm]});
            skFitSpline(sketch, "E263", {"points": [v(35.77, -16.62) * mm, v(36.22, -16.7) * mm, v(36.67, -16.64) * mm, v(37.13, -16.66) * mm]});
            skFitSpline(sketch, "E264", {"points": [v(37.13, -16.66) * mm, v(37.48, -16.68) * mm, v(37.83, -16.6) * mm, v(38.17, -16.7) * mm]});
            skFitSpline(sketch, "E265", {"points": [v(38.78, -16.7) * mm, v(39.38, -16.6) * mm, v(39.99, -16.69) * mm, v(40.59, -16.66) * mm]});
            skFitSpline(sketch, "E266", {"points": [v(40.59, -16.66) * mm, v(41.03, -16.65) * mm, v(41.48, -16.66) * mm, v(41.92, -16.65) * mm]});
            skFitSpline(sketch, "E267", {"points": [v(41.92, -16.65) * mm, v(42.02, -16.65) * mm, v(42.17, -16.71) * mm, v(42.18, -16.52) * mm]});
            skFitSpline(sketch, "E268", {"points": [v(42.18, -16.52) * mm, v(40.35, -16.18) * mm, v(38.52, -15.83) * mm, v(36.71, -15.35) * mm]});
            skFitSpline(sketch, "E269", {"points": [v(36.71, -15.35) * mm, v(36, -15.16) * mm, v(35.25, -15.03) * mm, v(34.53, -14.82) * mm]});
            skFitSpline(sketch, "E270", {"points": [v(34.53, -14.82) * mm, v(33.1, -14.38) * mm, v(31.81, -13.6) * mm, v(30.4, -13.1) * mm]});
            skFitSpline(sketch, "E271", {"points": [v(30.4, -13.1) * mm, v(28.9, -12.57) * mm, v(27.54, -11.75) * mm, v(26.13, -11.04) * mm]});
            skFitSpline(sketch, "E272", {"points": [v(26.13, -11.04) * mm, v(24.28, -10.1) * mm, v(22.61, -8.9) * mm, v(20.9, -7.78) * mm]});
            skFitSpline(sketch, "E273", {"points": [v(20.9, -7.78) * mm, v(19.32, -6.73) * mm, v(17.87, -5.46) * mm, v(16.43, -4.2) * mm]});
            skFitSpline(sketch, "E274", {"points": [v(16.43, -4.2) * mm, v(13.43, -1.57) * mm, v(10.5, 1.14) * mm, v(8.29, 4.51) * mm]});
            skFitSpline(sketch, "E275", {"points": [v(8.29, 4.51) * mm, v(6.39, 7.4) * mm, v(4.75, 10.42) * mm, v(4.04, 13.87) * mm]});
            skFitSpline(sketch, "E276", {"points": [v(4.04, 13.87) * mm, v(3.74, 15.29) * mm, v(3.6, 16.77) * mm, v(3.96, 18.15) * mm]});
            skFitSpline(sketch, "E277", {"points": [v(3.96, 18.15) * mm, v(4.68, 20.94) * mm, v(6.59, 22.1) * mm, v(9.37, 21.76) * mm]});
            skFitSpline(sketch, "E278", {"points": [v(9.37, 21.76) * mm, v(12.14, 21.42) * mm, v(14.36, 19.9) * mm, v(16.53, 18.28) * mm]});
            skFitSpline(sketch, "E279", {"points": [v(16.53, 18.28) * mm, v(17.05, 17.9) * mm, v(17.55, 17.5) * mm, v(18.06, 17.1) * mm]});
            skFitSpline(sketch, "E280", {"points": [v(18.06, 17.1) * mm, v(18.14, 17.24) * mm, v(18.06, 17.27) * mm, v(18.02, 17.3) * mm]});
            skFitSpline(sketch, "E281", {"points": [v(18.02, 17.3) * mm, v(15.67, 19.8) * mm, v(15.1, 22.76) * mm, v(15.81, 26.03) * mm]});
            skFitSpline(sketch, "E282", {"points": [v(15.81, 26.03) * mm, v(16.12, 27.45) * mm, v(16.96, 28.48) * mm, v(18.36, 29.08) * mm]});
            skFitSpline(sketch, "E283", {"points": [v(18.36, 29.08) * mm, v(17.45, 29.57) * mm, v(16.52, 29.83) * mm, v(15.58, 30.04) * mm]});
            skFitSpline(sketch, "E284", {"points": [v(15.58, 30.04) * mm, v(13.22, 30.57) * mm, v(10.83, 30.9) * mm, v(8.5, 31.57) * mm]});
            skFitSpline(sketch, "E285", {"points": [v(8.5, 31.57) * mm, v(7.27, 31.92) * mm, v(6.07, 32.36) * mm, v(4.9, 32.88) * mm]});
            skFitSpline(sketch, "E286", {"points": [v(4.9, 32.88) * mm, v(3.5, 33.5) * mm, v(2.36, 34.42) * mm, v(1.34, 35.53) * mm]});
            skFitSpline(sketch, "E287", {"points": [v(1.34, 35.53) * mm, v(0.04, 36.96) * mm, v(-0.59, 38.66) * mm, v(-0.74, 40.57) * mm]});
            skFitSpline(sketch, "E288", {"points": [v(-0.74, 40.57) * mm, v(-0.8, 41.38) * mm, v(-1, 42.17) * mm, v(-0.94, 43) * mm]});
            skFitSpline(sketch, "E289", {"points": [v(-0.94, 43) * mm, v(-0.85, 44.55) * mm, v(0.53, 45.67) * mm, v(2.04, 45.42) * mm]});
            skFitSpline(sketch, "E290", {"points": [v(2.04, 45.42) * mm, v(3.57, 45.16) * mm, v(5.04, 44.69) * mm, v(6.55, 44.35) * mm]});
            skFitSpline(sketch, "E291", {"points": [v(6.55, 44.35) * mm, v(8.37, 43.95) * mm, v(10.2, 43.7) * mm, v(12.06, 43.72) * mm]});
            skFitSpline(sketch, "E292", {"points": [v(12.06, 43.72) * mm, v(14.87, 43.77) * mm, v(17.47, 42.99) * mm, v(20.03, 41.9) * mm]});
            skFitSpline(sketch, "E293", {"points": [v(20.03, 41.9) * mm, v(22.15, 41) * mm, v(24.19, 39.94) * mm, v(26.08, 38.6) * mm]});
            skFitSpline(sketch, "E294", {"points": [v(26.08, 38.6) * mm, v(26.17, 38.53) * mm, v(26.25, 38.43) * mm, v(26.44, 38.49) * mm]});
            skFitSpline(sketch, "E295", {"points": [v(26.44, 38.49) * mm, v(25.56, 39.48) * mm, v(24.9, 40.61) * mm, v(24.5, 41.84) * mm]});
            skFitSpline(sketch, "E296", {"points": [v(24.5, 41.84) * mm, v(23.83, 43.93) * mm, v(23.78, 46.02) * mm, v(25.03, 47.97) * mm]});
            skFitSpline(sketch, "E297", {"points": [v(25.03, 47.97) * mm, v(25.46, 48.64) * mm, v(26.12, 49) * mm, v(26.82, 49.4) * mm]});
            skFitSpline(sketch, "E298", {"points": [v(26.82, 49.4) * mm, v(25.63, 50.1) * mm, v(24.78, 51.15) * mm, v(23.76, 52) * mm]});
            skFitSpline(sketch, "E299", {"points": [v(23.76, 52) * mm, v(22.25, 53.27) * mm, v(20.44, 53.7) * mm, v(18.55, 53.75) * mm]});
            skFitSpline(sketch, "E300", {"points": [v(18.55, 53.75) * mm, v(17.1, 53.78) * mm, v(15.64, 53.72) * mm, v(14.19, 53.67) * mm]});
            skFitSpline(sketch, "E301", {"points": [v(14.19, 53.67) * mm, v(9.06, 53.52) * mm, v(4.2, 54.58) * mm, v(-0.26, 57.24) * mm]});
            skFitSpline(sketch, "E302", {"points": [v(-0.26, 57.24) * mm, v(-2.15, 58.37) * mm, v(-4.03, 59.52) * mm, v(-6.07, 60.37) * mm]});
            skFitSpline(sketch, "E303", {"points": [v(-6.07, 60.37) * mm, v(-8.01, 61.18) * mm, v(-10.04, 61.62) * mm, v(-12.13, 61.77) * mm]});
            skFitSpline(sketch, "E304", {"points": [v(-12.13, 61.77) * mm, v(-12.45, 61.8) * mm, v(-12.78, 61.8) * mm, v(-13.07, 61.96) * mm]});
            skFitSpline(sketch, "E305", {"points": [v(-13.17, 61.96) * mm, v(-13.5, 61.88) * mm, v(-13.84, 61.88) * mm, v(-14.17, 61.96) * mm]});
            skFitSpline(sketch, "E306", {"points": [v(-42.85, 34.16) * mm, v(-42.6, 33.55) * mm, v(-42.66, 32.89) * mm, v(-42.57, 32.25) * mm]});
            skFitSpline(sketch, "E307", {"points": [v(-42.57, 32.25) * mm, v(-41.63, 25.4) * mm, v(-38.8, 19.57) * mm, v(-33.58, 15.04) * mm]});
            skFitSpline(sketch, "E308", {"points": [v(-33.58, 15.04) * mm, v(-30.64, 12.5) * mm, v(-27.24, 10.89) * mm, v(-23.4, 10.27) * mm]});
            skFitSpline(sketch, "E309", {"points": [v(-23.4, 10.27) * mm, v(-21.75, 10) * mm, v(-20.07, 10.08) * mm, v(-18.4, 10.01) * mm]});
            skFitSpline(sketch, "E310", {"points": [v(-18.4, 10.01) * mm, v(-17.32, 9.97) * mm, v(-16.24, 9.98) * mm, v(-15.16, 9.75) * mm]});
            skFitSpline(sketch, "E311", {"points": [v(-15.16, 9.75) * mm, v(-13.94, 9.5) * mm, v(-13.02, 8.84) * mm, v(-12.34, 7.82) * mm]});
            skFitSpline(sketch, "E312", {"points": [v(-12.34, 7.82) * mm, v(-12.12, 7.48) * mm, v(-11.9, 7.13) * mm, v(-11.74, 6.76) * mm]});
            skFitSpline(sketch, "E313", {"points": [v(-11.74, 6.76) * mm, v(-10.3, 3.3) * mm, v(-8.86, -0.17) * mm, v(-8.04, -3.86) * mm]});
            skFitSpline(sketch, "E314", {"points": [v(-8.04, -3.86) * mm, v(-7.85, -4.74) * mm, v(-7.75, -5.63) * mm, v(-7.8, -6.53) * mm]});
            skFitSpline(sketch, "E315", {"points": [v(-7.8, -6.53) * mm, v(-7.87, -7.98) * mm, v(-8.87, -8.66) * mm, v(-10.2, -8.17) * mm]});
            skFitSpline(sketch, "E316", {"points": [v(-10.2, -8.17) * mm, v(-10.5, -8.06) * mm, v(-10.77, -7.92) * mm, v(-11.11, -7.77) * mm]});
            skFitSpline(sketch, "E317", {"points": [v(-11.11, -7.77) * mm, v(-10.83, -8.76) * mm, v(-10.4, -9.55) * mm, v(-9.6, -10.14) * mm]});
            skFitSpline(sketch, "E318", {"points": [v(-9.6, -10.14) * mm, v(-8.24, -11.18) * mm, v(-6.68, -11.65) * mm, v(-5.02, -11.86) * mm]});
            skFitSpline(sketch, "E319", {"points": [v(-5.02, -11.86) * mm, v(-3.36, -12.08) * mm, v(-1.69, -12.11) * mm, v(-0.02, -12.17) * mm]});
            skFitSpline(sketch, "E320", {"points": [v(-0.02, -12.17) * mm, v(1.77, -12.22) * mm, v(3.54, -12.5) * mm, v(5.32, -12.72) * mm]});
            skFitSpline(sketch, "E321", {"points": [v(5.32, -12.72) * mm, v(8.35, -13.1) * mm, v(11.34, -13.75) * mm, v(14.36, -14.21) * mm]});
            skFitSpline(sketch, "E322", {"points": [v(14.36, -14.21) * mm, v(15.18, -14.34) * mm, v(15.97, -14.63) * mm, v(16.8, -14.73) * mm]});
            skFitSpline(sketch, "E323", {"points": [v(16.8, -14.73) * mm, v(16.9, -14.75) * mm, v(17.02, -14.82) * mm, v(17.01, -14.63) * mm]});
            skFitSpline(sketch, "E324", {"points": [v(17.01, -14.63) * mm, v(12.02, -12.4) * mm, v(7.75, -9.18) * mm, v(4.03, -5.13) * mm]});
            skFitSpline(sketch, "E325", {"points": [v(4.03, -5.13) * mm, v(2.16, -3.09) * mm, v(0.67, -0.8) * mm, v(-0.78, 1.53) * mm]});
            skFitSpline(sketch, "E326", {"points": [v(-0.78, 1.53) * mm, v(-4.46, 7.42) * mm, v(-6.77, 13.86) * mm, v(-8.17, 20.65) * mm]});
            skFitSpline(sketch, "E327", {"points": [v(-8.17, 20.65) * mm, v(-8.35, 21.53) * mm, v(-8.42, 22.43) * mm, v(-8.82, 23.24) * mm]});
            skFitSpline(sketch, "E328", {"points": [v(-8.82, 23.24) * mm, v(-9.7, 25.03) * mm, v(-11.2, 25.93) * mm, v(-13, 26.38) * mm]});
            skFitSpline(sketch, "E329", {"points": [v(-13, 26.38) * mm, v(-13.23, 26.44) * mm, v(-13.46, 26.48) * mm, v(-13.7, 26.5) * mm]});
            skFitSpline(sketch, "E330", {"points": [v(-13.7, 26.5) * mm, v(-14.73, 26.63) * mm, v(-15.75, 26.77) * mm, v(-16.72, 27.26) * mm]});
            skFitSpline(sketch, "E331", {"points": [v(-16.72, 27.26) * mm, v(-16.76, 26.85) * mm, v(-16.57, 26.54) * mm, v(-16.48, 26.2) * mm]});
            skFitSpline(sketch, "E332", {"points": [v(-16.48, 26.2) * mm, v(-16, 24.4) * mm, v(-15.74, 22.58) * mm, v(-16, 20.73) * mm]});
            skFitSpline(sketch, "E333", {"points": [v(-16, 20.73) * mm, v(-16.34, 18.26) * mm, v(-17.79, 16.82) * mm, v(-20.15, 16.25) * mm]});
            skFitSpline(sketch, "E334", {"points": [v(-20.15, 16.25) * mm, v(-23.4, 15.45) * mm, v(-26.44, 16.11) * mm, v(-29.3, 17.73) * mm]});
            skFitSpline(sketch, "E335", {"points": [v(-29.3, 17.73) * mm, v(-32.8, 19.7) * mm, v(-35.18, 22.74) * mm, v(-36.93, 26.32) * mm]});
            skFitSpline(sketch, "E336", {"points": [v(-36.93, 26.32) * mm, v(-38.65, 29.84) * mm, v(-39.63, 33.57) * mm, v(-39.2, 37.5) * mm]});
            skFitSpline(sketch, "E337", {"points": [v(-39.2, 37.5) * mm, v(-38.63, 42.7) * mm, v(-36.87, 47.38) * mm, v(-32.6, 50.7) * mm]});
            skFitSpline(sketch, "E338", {"points": [v(-32.6, 50.7) * mm, v(-31, 51.94) * mm, v(-29.21, 52.95) * mm, v(-27.17, 53.25) * mm]});
            skFitSpline(sketch, "E339", {"points": [v(-27.17, 53.25) * mm, v(-24.16, 53.7) * mm, v(-21.31, 53.26) * mm, v(-18.96, 51.14) * mm]});
            skFitSpline(sketch, "E340", {"points": [v(-18.96, 51.14) * mm, v(-17.44, 49.76) * mm, v(-17.08, 47.92) * mm, v(-17.36, 45.94) * mm]});
            skFitSpline(sketch, "E341", {"points": [v(-17.36, 45.94) * mm, v(-17.41, 45.6) * mm, v(-17.63, 45.32) * mm, v(-17.87, 45.07) * mm]});
            skFitSpline(sketch, "E342", {"points": [v(-17.87, 45.07) * mm, v(-18.18, 44.74) * mm, v(-18.5, 44.41) * mm, v(-18.82, 44.07) * mm]});
            skFitSpline(sketch, "E343", {"points": [v(-18.82, 44.07) * mm, v(-17.8, 43.58) * mm, v(-17.01, 42.78) * mm, v(-16.24, 41.96) * mm]});
            skFitSpline(sketch, "E344", {"points": [v(-16.24, 41.96) * mm, v(-15.3, 40.97) * mm, v(-14.34, 40.01) * mm, v(-13.2, 39.25) * mm]});
            skFitSpline(sketch, "E345", {"points": [v(-13.2, 39.25) * mm, v(-12.69, 38.9) * mm, v(-12.15, 38.94) * mm, v(-11.61, 38.96) * mm]});
            skFitSpline(sketch, "E346", {"points": [v(-11.61, 38.96) * mm, v(-11.36, 38.97) * mm, v(-11.24, 39.24) * mm, v(-11.12, 39.43) * mm]});
            skFitSpline(sketch, "E347", {"points": [v(-11.12, 39.43) * mm, v(-10.82, 39.9) * mm, v(-10.67, 40.43) * mm, v(-10.62, 40.96) * mm]});
            skFitSpline(sketch, "E348", {"points": [v(-10.62, 40.96) * mm, v(-10.29, 44.25) * mm, v(-10.66, 47.45) * mm, v(-11.87, 50.53) * mm]});
            skFitSpline(sketch, "E349", {"points": [v(-11.87, 50.53) * mm, v(-12.63, 52.45) * mm, v(-13.6, 54.26) * mm, v(-15, 55.8) * mm]});
            skFitSpline(sketch, "E350", {"points": [v(-15, 55.8) * mm, v(-16.53, 57.5) * mm, v(-18.38, 58.65) * mm, v(-20.61, 59.1) * mm]});
            skFitSpline(sketch, "E351", {"points": [v(-20.61, 59.1) * mm, v(-26.57, 60.31) * mm, v(-31.67, 58.5) * mm, v(-36.12, 54.5) * mm]});
            skFitSpline(sketch, "E352", {"points": [v(-36.12, 54.5) * mm, v(-38.56, 52.3) * mm, v(-39.83, 49.38) * mm, v(-40.94, 46.37) * mm]});
            skFitSpline(sketch, "E353", {"points": [v(-40.94, 46.37) * mm, v(-41.85, 43.9) * mm, v(-42.33, 41.33) * mm, v(-42.66, 38.73) * mm]});
            skFitSpline(sketch, "E354", {"points": [v(-42.66, 38.73) * mm, v(-42.7, 38.46) * mm, v(-42.67, 38.17) * mm, v(-42.85, 37.93) * mm]});
            skFitSpline(sketch, "E355", {"points": [v(-42.85, 36.81) * mm, v(-42.77, 36.37) * mm, v(-42.77, 35.93) * mm, v(-42.85, 35.49) * mm]});
            skFitSpline(sketch, "E356", {"points": [v(-42.85, 34.98) * mm, v(-42.8, 34.91) * mm, v(-42.8, 34.84) * mm, v(-42.85, 34.78) * mm]});
            skFitSpline(sketch, "E357", {"points": [v(40.63, -16.62) * mm, v(40.03, -16.65) * mm, v(39.42, -16.48) * mm, v(38.83, -16.7) * mm]});
            skFitSpline(sketch, "E358", {"points": [v(-42.85, 35.49) * mm, v(-42.69, 35.93) * mm, v(-42.69, 36.37) * mm, v(-42.85, 36.81) * mm]});
            skFitSpline(sketch, "E359", {"points": [v(-14.22, 61.96) * mm, v(-13.88, 61.8) * mm, v(-13.55, 61.8) * mm, v(-13.21, 61.96) * mm]});
            skFitSpline(sketch, "E360", {"points": [v(-42.85, 34.77) * mm, v(-42.7, 34.84) * mm, v(-42.72, 34.91) * mm, v(-42.85, 34.98) * mm]});
            skFitSpline(sketch, "E361", {"points": [v(36.2, -31.09) * mm, v(36.2, -31.19) * mm, v(36.14, -31.33) * mm, v(36.03, -31.52) * mm]});
            skFitSpline(sketch, "E362", {"points": [v(35.01, -30.98) * mm, v(34.51, -30.8) * mm, v(33.97, -30.7) * mm, v(33.37, -30.7) * mm]});
            skFitSpline(sketch, "E363", {"points": [v(27.52, -30.26) * mm, v(27.27, -29.84) * mm, v(27.06, -29.54) * mm, v(26.88, -29.35) * mm]});
            skFitSpline(sketch, "E364", {"points": [v(26.9, -29.28) * mm, v(26.91, -29.26) * mm, v(26.95, -29.22) * mm, v(27.02, -29.17) * mm]});
            skFitSpline(sketch, "E365", {"points": [v(27.02, -29.17) * mm, v(27.1, -29.12) * mm, v(27.16, -29.1) * mm, v(27.2, -29.1) * mm]});
            skFitSpline(sketch, "E366", {"points": [v(27.2, -29.1) * mm, v(27.32, -29.1) * mm, v(27.44, -29.17) * mm, v(27.55, -29.3) * mm]});
            skFitSpline(sketch, "E367", {"points": [v(27.55, -29.3) * mm, v(27.67, -29.44) * mm, v(27.78, -29.53) * mm, v(27.9, -29.57) * mm]});
            skFitSpline(sketch, "E368", {"points": [v(27.9, -29.57) * mm, v(28.63, -29.7) * mm, v(29.44, -29.76) * mm, v(30.32, -29.76) * mm]});
            skFitSpline(sketch, "E369", {"points": [v(34.41, -29.76) * mm, v(34.56, -29.76) * mm, v(34.8, -29.83) * mm, v(35.12, -29.97) * mm]});
            skFitSpline(sketch, "E370", {"points": [v(35.12, -29.97) * mm, v(35.46, -30.15) * mm, v(35.73, -30.31) * mm, v(35.93, -30.47) * mm]});
            skFitSpline(sketch, "E371", {"points": [v(35.93, -30.47) * mm, v(36.1, -30.6) * mm, v(36.2, -30.81) * mm, v(36.2, -31.09) * mm]});
            skFitSpline(sketch, "E372", {"points": [v(37.7, -29.32) * mm, v(38.17, -28.53) * mm, v(38.41, -27.65) * mm, v(38.41, -26.7) * mm]});
            skFitSpline(sketch, "E373", {"points": [v(38.41, -26.7) * mm, v(38.41, -26.04) * mm, v(38.22, -25.5) * mm, v(37.83, -25.09) * mm]});
            skFitSpline(sketch, "E374", {"points": [v(37.83, -25.09) * mm, v(37.44, -24.67) * mm, v(36.94, -24.4) * mm, v(36.33, -24.26) * mm]});
            skFitSpline(sketch, "E375", {"points": [v(36.33, -24.26) * mm, v(35.71, -24.13) * mm, v(34.95, -24.06) * mm, v(34.05, -24.06) * mm]});
            skFitSpline(sketch, "E376", {"points": [v(29.36, -24.3) * mm, v(28.94, -24.3) * mm, v(28.54, -24.31) * mm, v(28.15, -24.33) * mm]});
            skFitSpline(sketch, "E377", {"points": [v(28.15, -24.33) * mm, v(27.77, -24.35) * mm, v(27.48, -24.37) * mm, v(27.3, -24.39) * mm]});
            skFitSpline(sketch, "E378", {"points": [v(27.09, -23.13) * mm, v(28, -23.03) * mm, v(28.78, -22.97) * mm, v(29.45, -22.97) * mm]});
            skFitSpline(sketch, "E379", {"points": [v(36.14, -22.66) * mm, v(37.23, -22.66) * mm, v(38, -22.85) * mm, v(38.45, -23.23) * mm]});
            skFitSpline(sketch, "E380", {"points": [v(38.45, -23.23) * mm, v(38.93, -23.57) * mm, v(39.17, -24.28) * mm, v(39.17, -25.34) * mm]});
            skFitSpline(sketch, "E381", {"points": [v(39.17, -25.34) * mm, v(39.17, -26.27) * mm, v(39.07, -27.09) * mm, v(38.87, -27.8) * mm]});
            skFitSpline(sketch, "E382", {"points": [v(38.87, -27.8) * mm, v(38.67, -28.5) * mm, v(38.4, -29.07) * mm, v(38.04, -29.5) * mm]});
            skFitSpline(sketch, "E383", {"points": [v(41.6, -35.22) * mm, v(41.97, -35.64) * mm, v(42.27, -36.2) * mm, v(42.5, -36.9) * mm]});
            skFitSpline(sketch, "E384", {"points": [v(42.5, -36.9) * mm, v(42.74, -37.59) * mm, v(42.85, -38.1) * mm, v(42.85, -38.46) * mm]});
            skFitSpline(sketch, "E385", {"points": [v(42.85, -38.46) * mm, v(42.85, -39.3) * mm, v(42.5, -39.99) * mm, v(41.78, -40.53) * mm]});
            skFitSpline(sketch, "E386", {"points": [v(41.78, -40.53) * mm, v(41.06, -41.07) * mm, v(40, -41.34) * mm, v(38.6, -41.34) * mm]});
            skFitSpline(sketch, "E387", {"points": [v(38.6, -41.34) * mm, v(38.15, -41.34) * mm, v(37.7, -41.28) * mm, v(37.25, -41.15) * mm]});
            skFitSpline(sketch, "E388", {"points": [v(37.25, -41.15) * mm, v(36.8, -41.02) * mm, v(36.23, -40.79) * mm, v(35.56, -40.46) * mm]});
            skFitSpline(sketch, "E389", {"points": [v(35.56, -40.46) * mm, v(34.89, -40.13) * mm, v(34.18, -39.58) * mm, v(33.43, -38.82) * mm]});
            skFitSpline(sketch, "E390", {"points": [v(33.43, -38.82) * mm, v(32.68, -38.05) * mm, v(32.09, -37.3) * mm, v(31.65, -36.54) * mm]});
            skFitSpline(sketch, "E391", {"points": [v(31.65, -36.54) * mm, v(31.22, -35.8) * mm, v(30.9, -34.88) * mm, v(30.71, -33.8) * mm]});
            skFitSpline(sketch, "E392", {"points": [v(30.71, -33.8) * mm, v(30.52, -32.72) * mm, v(30.36, -31.52) * mm, v(30.25, -30.2) * mm]});
            skFitSpline(sketch, "E393", {"points": [v(29.88, -26.54) * mm, v(29.74, -25.38) * mm, v(29.63, -24.72) * mm, v(29.55, -24.56) * mm]});
            skFitSpline(sketch, "E394", {"points": [v(29.3, -24.3) * mm, v(29.2, -24.2) * mm, v(29.15, -24.15) * mm, v(29.13, -24.1) * mm]});
            skFitSpline(sketch, "E395", {"points": [v(29.13, -24.1) * mm, v(29.11, -24.07) * mm, v(29.1, -24.04) * mm, v(29.08, -24) * mm]});
            skFitSpline(sketch, "E396", {"points": [v(29.08, -24) * mm, v(29.12, -23.98) * mm, v(29.15, -23.96) * mm, v(29.18, -23.96) * mm]});
            skFitSpline(sketch, "E397", {"points": [v(29.55, -24.04) * mm, v(30.22, -24.23) * mm, v(30.7, -24.7) * mm, v(31.01, -25.46) * mm]});
            skFitSpline(sketch, "E398", {"points": [v(31.01, -25.46) * mm, v(31.32, -26.2) * mm, v(31.52, -26.85) * mm, v(31.61, -27.39) * mm]});
            skFitSpline(sketch, "E399", {"points": [v(31.61, -27.39) * mm, v(31.71, -27.92) * mm, v(31.76, -28.48) * mm, v(31.76, -29.06) * mm]});
            skFitSpline(sketch, "E400", {"points": [v(31.88, -31.82) * mm, v(31.88, -32.1) * mm, v(31.89, -32.36) * mm, v(31.92, -32.58) * mm]});
            skFitSpline(sketch, "E401", {"points": [v(31.92, -32.58) * mm, v(31.94, -32.8) * mm, v(32, -33.16) * mm, v(32.07, -33.64) * mm]});
            skFitSpline(sketch, "E402", {"points": [v(32.07, -33.64) * mm, v(32.15, -34.3) * mm, v(32.27, -34.99) * mm, v(32.45, -35.7) * mm]});
            skFitSpline(sketch, "E403", {"points": [v(32.45, -35.7) * mm, v(32.62, -36.42) * mm, v(32.86, -37.03) * mm, v(33.17, -37.52) * mm]});
            skFitSpline(sketch, "E404", {"points": [v(33.17, -37.52) * mm, v(33.47, -38.01) * mm, v(33.84, -38.43) * mm, v(34.26, -38.78) * mm]});
            skFitSpline(sketch, "E405", {"points": [v(34.26, -38.78) * mm, v(34.69, -39.09) * mm, v(35.16, -39.32) * mm, v(35.68, -39.48) * mm]});
            skFitSpline(sketch, "E406", {"points": [v(35.68, -39.48) * mm, v(36.2, -39.63) * mm, v(36.72, -39.71) * mm, v(37.27, -39.71) * mm]});
            skFitSpline(sketch, "E407", {"points": [v(38.3, -39.63) * mm, v(38.88, -39.54) * mm, v(39.37, -39.44) * mm, v(39.78, -39.32) * mm]});
            skFitSpline(sketch, "E408", {"points": [v(39.78, -39.32) * mm, v(40.19, -39.2) * mm, v(40.56, -39.06) * mm, v(40.88, -38.89) * mm]});
            skFitSpline(sketch, "E409", {"points": [v(40.88, -38.89) * mm, v(41.21, -38.72) * mm, v(41.47, -38.5) * mm, v(41.65, -38.22) * mm]});
            skFitSpline(sketch, "E410", {"points": [v(41.65, -38.22) * mm, v(41.83, -37.95) * mm, v(41.92, -37.64) * mm, v(41.92, -37.28) * mm]});
            skFitSpline(sketch, "E411", {"points": [v(41.92, -37.28) * mm, v(41.92, -37.03) * mm, v(41.88, -36.79) * mm, v(41.8, -36.55) * mm]});
            skFitSpline(sketch, "E412", {"points": [v(41.8, -36.55) * mm, v(41.73, -36.31) * mm, v(41.63, -36.11) * mm, v(41.52, -35.94) * mm]});
            skFitSpline(sketch, "E413", {"points": [v(41.52, -35.94) * mm, v(41.46, -35.83) * mm, v(41.42, -35.74) * mm, v(41.37, -35.68) * mm]});
            skFitSpline(sketch, "E414", {"points": [v(41.37, -35.68) * mm, v(41.32, -35.62) * mm, v(41.25, -35.53) * mm, v(41.15, -35.4) * mm]});
            skFitSpline(sketch, "E415", {"points": [v(40.72, -34.76) * mm, v(40.72, -34.65) * mm, v(40.78, -34.6) * mm, v(40.91, -34.6) * mm]});
            skFitSpline(sketch, "E416", {"points": [v(40.91, -34.6) * mm, v(41, -34.6) * mm, v(41.23, -34.8) * mm, v(41.6, -35.22) * mm]});
            skFitSpline(sketch, "E417", {"points": [v(24.15, -33.75) * mm, v(24.06, -33.18) * mm, v(23.87, -31.77) * mm, v(23.56, -29.53) * mm]});
            skFitSpline(sketch, "E418", {"points": [v(23.5, -28.89) * mm, v(23.5, -28.54) * mm, v(23.58, -28.37) * mm, v(23.75, -28.37) * mm]});
            skFitSpline(sketch, "E419", {"points": [v(23.75, -28.37) * mm, v(23.88, -28.37) * mm, v(24.04, -28.42) * mm, v(24.23, -28.54) * mm]});
            skFitSpline(sketch, "E420", {"points": [v(26.33, -30.01) * mm, v(26.43, -30.09) * mm, v(26.48, -30.19) * mm, v(26.48, -30.3) * mm]});
            skFitSpline(sketch, "E421", {"points": [v(26.17, -30.3) * mm, v(26.07, -30.28) * mm, v(25.91, -30.2) * mm, v(25.7, -30.04) * mm]});
            skFitSpline(sketch, "E422", {"points": [v(25.7, -30.04) * mm, v(25.49, -29.9) * mm, v(25.34, -29.82) * mm, v(25.26, -29.82) * mm]});
            skFitSpline(sketch, "E423", {"points": [v(25.26, -29.82) * mm, v(25.19, -29.82) * mm, v(25.15, -29.98) * mm, v(25.15, -30.3) * mm]});
            skFitSpline(sketch, "E424", {"points": [v(25.79, -35.64) * mm, v(25.8, -35.72) * mm, v(25.82, -35.8) * mm, v(25.83, -35.86) * mm]});
            skFitSpline(sketch, "E425", {"points": [v(25.83, -35.86) * mm, v(25.85, -35.93) * mm, v(25.87, -35.98) * mm, v(25.88, -36) * mm]});
            skFitSpline(sketch, "E426", {"points": [v(24.4, -35.44) * mm, v(24.32, -34.88) * mm, v(24.23, -34.32) * mm, v(24.15, -33.75) * mm]});
            skFitSpline(sketch, "E427", {"points": [v(21.46, -30.67) * mm, v(20.87, -29.75) * mm, v(20.57, -29.17) * mm, v(20.57, -28.93) * mm]});
            skFitSpline(sketch, "E428", {"points": [v(20.57, -28.93) * mm, v(20.57, -28.55) * mm, v(20.73, -28.37) * mm, v(21.05, -28.37) * mm]});
            skFitSpline(sketch, "E429", {"points": [v(21.05, -28.37) * mm, v(21.3, -28.37) * mm, v(21.63, -28.5) * mm, v(22.03, -28.76) * mm]});
            skFitSpline(sketch, "E430", {"points": [v(22.03, -28.76) * mm, v(22.44, -29.03) * mm, v(22.83, -29.4) * mm, v(23.19, -29.85) * mm]});
            skFitSpline(sketch, "E431", {"points": [v(23.89, -30.75) * mm, v(24.12, -30.85) * mm, v(24.23, -31.02) * mm, v(24.23, -31.25) * mm]});
            skFitSpline(sketch, "E432", {"points": [v(24.23, -31.25) * mm, v(24.23, -31.3) * mm, v(24.2, -31.35) * mm, v(24.14, -31.4) * mm]});
            skFitSpline(sketch, "E433", {"points": [v(24.14, -31.4) * mm, v(24.03, -31.4) * mm, v(23.87, -31.33) * mm, v(23.65, -31.18) * mm]});
            skFitSpline(sketch, "E434", {"points": [v(23.19, -30.77) * mm, v(22.74, -30.3) * mm, v(22.42, -30.07) * mm, v(22.24, -30.07) * mm]});
            skFitSpline(sketch, "E435", {"points": [v(22.24, -30.07) * mm, v(22.15, -30.07) * mm, v(22.1, -30.14) * mm, v(22.1, -30.27) * mm]});
            skFitSpline(sketch, "E436", {"points": [v(22.1, -30.27) * mm, v(22.1, -30.43) * mm, v(22.16, -30.68) * mm, v(22.27, -31) * mm]});
            skFitSpline(sketch, "E437", {"points": [v(22.27, -31) * mm, v(22.38, -31.33) * mm, v(22.44, -31.56) * mm, v(22.47, -31.7) * mm]});
            skFitSpline(sketch, "E438", {"points": [v(22.47, -31.7) * mm, v(22.5, -31.84) * mm, v(22.52, -31.96) * mm, v(22.53, -32.05) * mm]});
            skFitSpline(sketch, "E439", {"points": [v(22.53, -32.05) * mm, v(22.41, -32.05) * mm, v(22.06, -31.59) * mm, v(21.46, -30.67) * mm]});
            skFitSpline(sketch, "E440", {"points": [v(15.02, -29.33) * mm, v(14.92, -29.28) * mm, v(14.83, -29.19) * mm, v(14.76, -29.06) * mm]});
            skFitSpline(sketch, "E441", {"points": [v(14.76, -29.06) * mm, v(14.7, -28.94) * mm, v(14.65, -28.82) * mm, v(14.65, -28.72) * mm]});
            skFitSpline(sketch, "E442", {"points": [v(14.65, -28.72) * mm, v(14.65, -28.52) * mm, v(14.85, -28.42) * mm, v(15.24, -28.42) * mm]});
            skFitSpline(sketch, "E443", {"points": [v(16.71, -28.55) * mm, v(17.06, -28.55) * mm, v(17.39, -28.64) * mm, v(17.7, -28.8) * mm]});
            skFitSpline(sketch, "E444", {"points": [v(17.7, -28.8) * mm, v(18, -28.96) * mm, v(18.35, -29.24) * mm, v(18.73, -29.65) * mm]});
            skFitSpline(sketch, "E445", {"points": [v(18.73, -29.65) * mm, v(19.1, -30.06) * mm, v(19.4, -30.54) * mm, v(19.6, -31.09) * mm]});
            skFitSpline(sketch, "E446", {"points": [v(19.6, -31.09) * mm, v(19.8, -31.63) * mm, v(19.96, -32.08) * mm, v(20.05, -32.43) * mm]});
            skFitSpline(sketch, "E447", {"points": [v(20.05, -32.43) * mm, v(20.14, -32.78) * mm, v(20.2, -33.1) * mm, v(20.25, -33.38) * mm]});
            skFitSpline(sketch, "E448", {"points": [v(20.25, -33.38) * mm, v(20.3, -33.67) * mm, v(20.32, -33.9) * mm, v(20.34, -34.1) * mm]});
            skFitSpline(sketch, "E449", {"points": [v(20.34, -34.1) * mm, v(20.35, -34.28) * mm, v(20.36, -34.42) * mm, v(20.36, -34.5) * mm]});
            skFitSpline(sketch, "E450", {"points": [v(20.36, -34.5) * mm, v(20.36, -35.53) * mm, v(20.07, -36.04) * mm, v(19.5, -36.04) * mm]});
            skFitSpline(sketch, "E451", {"points": [v(19.5, -36.04) * mm, v(18.97, -36.04) * mm, v(18.24, -35.55) * mm, v(17.3, -34.56) * mm]});
            skFitSpline(sketch, "E452", {"points": [v(16.63, -33.84) * mm, v(16.43, -33.63) * mm, v(16.26, -33.42) * mm, v(16.13, -33.2) * mm]});
            skFitSpline(sketch, "E453", {"points": [v(16.13, -33.2) * mm, v(16, -32.97) * mm, v(15.93, -32.75) * mm, v(15.93, -32.53) * mm]});
            skFitSpline(sketch, "E454", {"points": [v(15.93, -32.53) * mm, v(15.93, -32.47) * mm, v(15.96, -32.39) * mm, v(16.01, -32.3) * mm]});
            skFitSpline(sketch, "E455", {"points": [v(16.46, -32.84) * mm, v(16.73, -33.22) * mm, v(17.05, -33.61) * mm, v(17.43, -34) * mm]});
            skFitSpline(sketch, "E456", {"points": [v(17.43, -34) * mm, v(17.8, -34.4) * mm, v(18.13, -34.6) * mm, v(18.4, -34.6) * mm]});
            skFitSpline(sketch, "E457", {"points": [v(18.4, -34.6) * mm, v(18.72, -34.6) * mm, v(18.88, -34.26) * mm, v(18.88, -33.58) * mm]});
            skFitSpline(sketch, "E458", {"points": [v(18.88, -33.58) * mm, v(18.88, -33.1) * mm, v(18.81, -32.5) * mm, v(18.68, -31.8) * mm]});
            skFitSpline(sketch, "E459", {"points": [v(18.68, -31.8) * mm, v(18.54, -31.1) * mm, v(18.39, -30.58) * mm, v(18.21, -30.24) * mm]});
            skFitSpline(sketch, "E460", {"points": [v(18.21, -30.24) * mm, v(18.04, -29.9) * mm, v(17.85, -29.68) * mm, v(17.65, -29.57) * mm]});
            skFitSpline(sketch, "E461", {"points": [v(17.65, -29.57) * mm, v(17.45, -29.46) * mm, v(17.22, -29.4) * mm, v(16.96, -29.4) * mm]});
            skFitSpline(sketch, "E462", {"points": [v(14.54, -29.14) * mm, v(14.54, -28.69) * mm, v(14.68, -28.46) * mm, v(14.97, -28.46) * mm]});
            skFitSpline(sketch, "E463", {"points": [v(14.97, -28.46) * mm, v(15.12, -28.46) * mm, v(15.3, -28.55) * mm, v(15.53, -28.73) * mm]});
            skFitSpline(sketch, "E464", {"points": [v(15.53, -28.73) * mm, v(15.72, -28.93) * mm, v(15.88, -29.18) * mm, v(16, -29.48) * mm]});
            skFitSpline(sketch, "E465", {"points": [v(16, -29.48) * mm, v(16.12, -29.78) * mm, v(16.2, -30.05) * mm, v(16.26, -30.28) * mm]});
            skFitSpline(sketch, "E466", {"points": [v(16.26, -30.28) * mm, v(16.31, -30.5) * mm, v(16.35, -30.78) * mm, v(16.38, -31.1) * mm]});
            skFitSpline(sketch, "E467", {"points": [v(16.85, -35.3) * mm, v(16.85, -35.79) * mm, v(16.74, -36.03) * mm, v(16.52, -36.03) * mm]});
            skFitSpline(sketch, "E468", {"points": [v(16.52, -36.03) * mm, v(16.3, -36.03) * mm, v(16.02, -35.88) * mm, v(15.66, -35.6) * mm]});
            skFitSpline(sketch, "E469", {"points": [v(15.66, -35.6) * mm, v(15.3, -35.35) * mm, v(14.71, -34.87) * mm, v(13.9, -34.14) * mm]});
            skFitSpline(sketch, "E470", {"points": [v(13.9, -34.14) * mm, v(13.85, -34.08) * mm, v(13.8, -34.03) * mm, v(13.78, -33.99) * mm]});
            skFitSpline(sketch, "E471", {"points": [v(13.78, -33.99) * mm, v(13.76, -33.95) * mm, v(13.74, -33.91) * mm, v(13.72, -33.87) * mm]});
            skFitSpline(sketch, "E472", {"points": [v(13.72, -33.87) * mm, v(13.72, -33.85) * mm, v(13.76, -33.81) * mm, v(13.82, -33.78) * mm]});
            skFitSpline(sketch, "E473", {"points": [v(13.82, -33.78) * mm, v(13.91, -33.78) * mm, v(14.02, -33.82) * mm, v(14.16, -33.91) * mm]});
            skFitSpline(sketch, "E474", {"points": [v(14.16, -33.91) * mm, v(14.3, -34) * mm, v(14.42, -34.1) * mm, v(14.54, -34.18) * mm]});
            skFitSpline(sketch, "E475", {"points": [v(14.54, -34.18) * mm, v(14.65, -34.27) * mm, v(14.76, -34.36) * mm, v(14.85, -34.45) * mm]});
            skFitSpline(sketch, "E476", {"points": [v(15.26, -34.75) * mm, v(15.27, -34.73) * mm, v(15.28, -34.71) * mm, v(15.3, -34.68) * mm]});
            skFitSpline(sketch, "E477", {"points": [v(15.3, -34.68) * mm, v(15.32, -34.65) * mm, v(15.33, -34.6) * mm, v(15.33, -34.51) * mm]});
            skFitSpline(sketch, "E478", {"points": [v(8.27, -29.31) * mm, v(8.17, -29.25) * mm, v(8.1, -29.17) * mm, v(8.04, -29.08) * mm]});
            skFitSpline(sketch, "E479", {"points": [v(7.89, -28.74) * mm, v(7.89, -28.55) * mm, v(8.08, -28.46) * mm, v(8.47, -28.35) * mm]});
            skFitSpline(sketch, "E480", {"points": [v(10.14, -28.6) * mm, v(10.8, -28.66) * mm, v(11.4, -28.9) * mm, v(11.9, -29.32) * mm]});
            skFitSpline(sketch, "E481", {"points": [v(11.9, -29.32) * mm, v(12.39, -29.73) * mm, v(12.8, -30.26) * mm, v(13.12, -30.9) * mm]});
            skFitSpline(sketch, "E482", {"points": [v(13.12, -30.9) * mm, v(13.45, -31.53) * mm, v(13.66, -32.18) * mm, v(13.76, -32.84) * mm]});
            skFitSpline(sketch, "E483", {"points": [v(13.76, -32.84) * mm, v(13.87, -33.5) * mm, v(13.92, -34.06) * mm, v(13.92, -34.53) * mm]});
            skFitSpline(sketch, "E484", {"points": [v(13.92, -34.53) * mm, v(13.92, -35.58) * mm, v(13.67, -36.1) * mm, v(13.16, -36.1) * mm]});
            skFitSpline(sketch, "E485", {"points": [v(13.16, -36.1) * mm, v(12.73, -36.1) * mm, v(12.1, -35.65) * mm, v(11.28, -34.74) * mm]});
            skFitSpline(sketch, "E486", {"points": [v(10.47, -33.88) * mm, v(10.2, -33.6) * mm, v(10.01, -33.4) * mm, v(9.88, -33.26) * mm]});
            skFitSpline(sketch, "E487", {"points": [v(9.88, -33.26) * mm, v(9.75, -33.12) * mm, v(9.62, -32.94) * mm, v(9.49, -32.74) * mm]});
            skFitSpline(sketch, "E488", {"points": [v(9.49, -32.74) * mm, v(9.35, -32.54) * mm, v(9.28, -32.33) * mm, v(9.28, -32.1) * mm]});
            skFitSpline(sketch, "E489", {"points": [v(9.28, -32.1) * mm, v(9.28, -31.93) * mm, v(9.32, -31.84) * mm, v(9.4, -31.84) * mm]});
            skFitSpline(sketch, "E490", {"points": [v(9.4, -31.84) * mm, v(9.48, -31.84) * mm, v(9.57, -31.9) * mm, v(9.69, -32.05) * mm]});
            skFitSpline(sketch, "E491", {"points": [v(11.14, -33.94) * mm, v(11.65, -34.48) * mm, v(12.02, -34.75) * mm, v(12.27, -34.75) * mm]});
            skFitSpline(sketch, "E492", {"points": [v(12.27, -34.75) * mm, v(12.49, -34.75) * mm, v(12.6, -34.54) * mm, v(12.6, -34.13) * mm]});
            skFitSpline(sketch, "E493", {"points": [v(12.13, -31.6) * mm, v(12.02, -31.02) * mm, v(11.87, -30.55) * mm, v(11.68, -30.21) * mm]});
            skFitSpline(sketch, "E494", {"points": [v(11.68, -30.21) * mm, v(11.5, -29.87) * mm, v(11.29, -29.65) * mm, v(11.07, -29.55) * mm]});
            skFitSpline(sketch, "E495", {"points": [v(11.07, -29.55) * mm, v(10.85, -29.44) * mm, v(10.6, -29.4) * mm, v(10.33, -29.4) * mm]});
            skFitSpline(sketch, "E496", {"points": [v(8.7, -28.7) * mm, v(8.82, -28.7) * mm, v(8.99, -28.7) * mm, v(9.2, -28.7) * mm]});
            skFitSpline(sketch, "E497", {"points": [v(9.2, -28.7) * mm, v(9.37, -28.7) * mm, v(9.46, -28.75) * mm, v(9.46, -28.84) * mm]});
            skFitSpline(sketch, "E498", {"points": [v(10.47, -37.68) * mm, v(10.47, -38.03) * mm, v(10.49, -38.32) * mm, v(10.52, -38.56) * mm]});
            skFitSpline(sketch, "E499", {"points": [v(10.52, -38.56) * mm, v(10.56, -38.8) * mm, v(10.61, -39.05) * mm, v(10.68, -39.3) * mm]});
            skFitSpline(sketch, "E500", {"points": [v(10.68, -39.3) * mm, v(10.78, -39.59) * mm, v(10.95, -39.8) * mm, v(11.18, -39.95) * mm]});
            skFitSpline(sketch, "E501", {"points": [v(11.18, -39.95) * mm, v(11.44, -40.14) * mm, v(11.82, -40.24) * mm, v(12.3, -40.24) * mm]});
            skFitSpline(sketch, "E502", {"points": [v(12.3, -40.24) * mm, v(12.8, -40.24) * mm, v(13.23, -40.1) * mm, v(13.6, -39.8) * mm]});
            skFitSpline(sketch, "E503", {"points": [v(13.6, -39.8) * mm, v(13.97, -39.51) * mm, v(14.15, -39.17) * mm, v(14.15, -38.79) * mm]});
            skFitSpline(sketch, "E504", {"points": [v(14.15, -38.79) * mm, v(14.15, -38.63) * mm, v(14.09, -38.42) * mm, v(13.97, -38.16) * mm]});
            skFitSpline(sketch, "E505", {"points": [v(13.97, -38.16) * mm, v(13.84, -37.9) * mm, v(13.64, -37.65) * mm, v(13.36, -37.43) * mm]});
            skFitSpline(sketch, "E506", {"points": [v(13.36, -37.43) * mm, v(13.09, -37.2) * mm, v(12.88, -37.06) * mm, v(12.75, -36.97) * mm]});
            skFitSpline(sketch, "E507", {"points": [v(12.75, -36.97) * mm, v(12.63, -36.89) * mm, v(12.46, -36.8) * mm, v(12.25, -36.7) * mm]});
            skFitSpline(sketch, "E508", {"points": [v(11.22, -36.28) * mm, v(11.05, -36.22) * mm, v(10.93, -36.17) * mm, v(10.85, -36.13) * mm]});
            skFitSpline(sketch, "E509", {"points": [v(10.85, -36.13) * mm, v(10.78, -36.1) * mm, v(10.71, -36.05) * mm, v(10.66, -36) * mm]});
            skFitSpline(sketch, "E510", {"points": [v(10.7, -35.94) * mm, v(10.92, -35.94) * mm, v(11.3, -36.06) * mm, v(11.84, -36.3) * mm]});
            skFitSpline(sketch, "E511", {"points": [v(11.84, -36.3) * mm, v(12.39, -36.55) * mm, v(12.92, -36.85) * mm, v(13.44, -37.22) * mm]});
            skFitSpline(sketch, "E512", {"points": [v(13.44, -37.22) * mm, v(13.97, -37.58) * mm, v(14.33, -37.93) * mm, v(14.53, -38.26) * mm]});
            skFitSpline(sketch, "E513", {"points": [v(14.53, -38.26) * mm, v(14.73, -38.6) * mm, v(14.83, -39.01) * mm, v(14.83, -39.5) * mm]});
            skFitSpline(sketch, "E514", {"points": [v(14.83, -39.5) * mm, v(14.83, -40) * mm, v(14.68, -40.42) * mm, v(14.4, -40.78) * mm]});
            skFitSpline(sketch, "E515", {"points": [v(14.4, -40.78) * mm, v(14.1, -41.15) * mm, v(13.7, -41.33) * mm, v(13.16, -41.33) * mm]});
            skFitSpline(sketch, "E516", {"points": [v(13.16, -41.33) * mm, v(12.49, -41.33) * mm, v(11.78, -41.05) * mm, v(11.02, -40.5) * mm]});
            skFitSpline(sketch, "E517", {"points": [v(11.02, -40.5) * mm, v(10.26, -39.94) * mm, v(9.75, -39.25) * mm, v(9.49, -38.43) * mm]});
            skFitSpline(sketch, "E518", {"points": [v(9.49, -38.43) * mm, v(9.22, -37.6) * mm, v(9.02, -36.56) * mm, v(8.88, -35.3) * mm]});
            skFitSpline(sketch, "E519", {"points": [v(8.5, -31.75) * mm, v(8.4, -30.62) * mm, v(8.24, -29.7) * mm, v(8.04, -28.95) * mm]});
            skFitSpline(sketch, "E520", {"points": [v(8.04, -28.95) * mm, v(8.04, -28.79) * mm, v(8.26, -28.7) * mm, v(8.7, -28.7) * mm]});
            skFitSpline(sketch, "E521", {"points": [v(2.67, -29.33) * mm, v(2.57, -29.28) * mm, v(2.48, -29.19) * mm, v(2.4, -29.06) * mm]});
            skFitSpline(sketch, "E522", {"points": [v(2.4, -29.06) * mm, v(2.34, -28.94) * mm, v(2.3, -28.82) * mm, v(2.3, -28.72) * mm]});
            skFitSpline(sketch, "E523", {"points": [v(2.3, -28.72) * mm, v(2.3, -28.52) * mm, v(2.5, -28.42) * mm, v(2.88, -28.42) * mm]});
            skFitSpline(sketch, "E524", {"points": [v(4.36, -28.55) * mm, v(4.7, -28.55) * mm, v(5.04, -28.64) * mm, v(5.35, -28.8) * mm]});
            skFitSpline(sketch, "E525", {"points": [v(5.35, -28.8) * mm, v(5.66, -28.96) * mm, v(6, -29.24) * mm, v(6.37, -29.65) * mm]});
            skFitSpline(sketch, "E526", {"points": [v(6.37, -29.65) * mm, v(6.75, -30.06) * mm, v(7.04, -30.54) * mm, v(7.25, -31.09) * mm]});
            skFitSpline(sketch, "E527", {"points": [v(7.25, -31.09) * mm, v(7.45, -31.63) * mm, v(7.6, -32.08) * mm, v(7.7, -32.43) * mm]});
            skFitSpline(sketch, "E528", {"points": [v(7.7, -32.43) * mm, v(7.78, -32.78) * mm, v(7.85, -33.1) * mm, v(7.9, -33.38) * mm]});
            skFitSpline(sketch, "E529", {"points": [v(7.9, -33.38) * mm, v(7.94, -33.67) * mm, v(7.97, -33.9) * mm, v(7.98, -34.1) * mm]});
            skFitSpline(sketch, "E530", {"points": [v(7.98, -34.1) * mm, v(8, -34.28) * mm, v(8, -34.42) * mm, v(8, -34.5) * mm]});
            skFitSpline(sketch, "E531", {"points": [v(8, -34.5) * mm, v(8, -35.53) * mm, v(7.72, -36.04) * mm, v(7.15, -36.04) * mm]});
            skFitSpline(sketch, "E532", {"points": [v(7.15, -36.04) * mm, v(6.62, -36.04) * mm, v(5.88, -35.55) * mm, v(4.94, -34.56) * mm]});
            skFitSpline(sketch, "E533", {"points": [v(4.28, -33.84) * mm, v(4.07, -33.63) * mm, v(3.9, -33.42) * mm, v(3.78, -33.2) * mm]});
            skFitSpline(sketch, "E534", {"points": [v(3.78, -33.2) * mm, v(3.65, -32.97) * mm, v(3.58, -32.75) * mm, v(3.58, -32.53) * mm]});
            skFitSpline(sketch, "E535", {"points": [v(3.58, -32.53) * mm, v(3.58, -32.47) * mm, v(3.6, -32.39) * mm, v(3.66, -32.3) * mm]});
            skFitSpline(sketch, "E536", {"points": [v(4.1, -32.84) * mm, v(4.38, -33.22) * mm, v(4.7, -33.61) * mm, v(5.07, -34) * mm]});
            skFitSpline(sketch, "E537", {"points": [v(5.07, -34) * mm, v(5.45, -34.4) * mm, v(5.77, -34.6) * mm, v(6.04, -34.6) * mm]});
            skFitSpline(sketch, "E538", {"points": [v(6.04, -34.6) * mm, v(6.37, -34.6) * mm, v(6.53, -34.26) * mm, v(6.53, -33.58) * mm]});
            skFitSpline(sketch, "E539", {"points": [v(6.53, -33.58) * mm, v(6.53, -33.1) * mm, v(6.46, -32.5) * mm, v(6.33, -31.8) * mm]});
            skFitSpline(sketch, "E540", {"points": [v(6.33, -31.8) * mm, v(6.19, -31.1) * mm, v(6.03, -30.58) * mm, v(5.86, -30.24) * mm]});
            skFitSpline(sketch, "E541", {"points": [v(5.86, -30.24) * mm, v(5.69, -29.9) * mm, v(5.5, -29.68) * mm, v(5.3, -29.57) * mm]});
            skFitSpline(sketch, "E542", {"points": [v(5.3, -29.57) * mm, v(5.1, -29.46) * mm, v(4.87, -29.4) * mm, v(4.6, -29.4) * mm]});
            skFitSpline(sketch, "E543", {"points": [v(2.19, -29.14) * mm, v(2.19, -28.69) * mm, v(2.33, -28.46) * mm, v(2.62, -28.46) * mm]});
            skFitSpline(sketch, "E544", {"points": [v(2.62, -28.46) * mm, v(2.77, -28.46) * mm, v(2.96, -28.55) * mm, v(3.17, -28.73) * mm]});
            skFitSpline(sketch, "E545", {"points": [v(3.17, -28.73) * mm, v(3.37, -28.93) * mm, v(3.52, -29.18) * mm, v(3.65, -29.48) * mm]});
            skFitSpline(sketch, "E546", {"points": [v(3.65, -29.48) * mm, v(3.77, -29.78) * mm, v(3.86, -30.05) * mm, v(3.9, -30.28) * mm]});
            skFitSpline(sketch, "E547", {"points": [v(3.9, -30.28) * mm, v(3.96, -30.5) * mm, v(4, -30.78) * mm, v(4.02, -31.1) * mm]});
            skFitSpline(sketch, "E548", {"points": [v(4.5, -35.3) * mm, v(4.5, -35.79) * mm, v(4.38, -36.03) * mm, v(4.16, -36.03) * mm]});
            skFitSpline(sketch, "E549", {"points": [v(4.16, -36.03) * mm, v(3.96, -36.03) * mm, v(3.67, -35.88) * mm, v(3.3, -35.6) * mm]});
            skFitSpline(sketch, "E550", {"points": [v(3.3, -35.6) * mm, v(2.95, -35.35) * mm, v(2.36, -34.87) * mm, v(1.54, -34.14) * mm]});
            skFitSpline(sketch, "E551", {"points": [v(1.54, -34.14) * mm, v(1.5, -34.08) * mm, v(1.45, -34.03) * mm, v(1.43, -33.99) * mm]});
            skFitSpline(sketch, "E552", {"points": [v(1.43, -33.99) * mm, v(1.4, -33.95) * mm, v(1.38, -33.91) * mm, v(1.37, -33.87) * mm]});
            skFitSpline(sketch, "E553", {"points": [v(1.37, -33.87) * mm, v(1.37, -33.85) * mm, v(1.4, -33.81) * mm, v(1.47, -33.78) * mm]});
            skFitSpline(sketch, "E554", {"points": [v(1.47, -33.78) * mm, v(1.56, -33.78) * mm, v(1.67, -33.82) * mm, v(1.8, -33.91) * mm]});
            skFitSpline(sketch, "E555", {"points": [v(1.8, -33.91) * mm, v(1.94, -34) * mm, v(2.07, -34.1) * mm, v(2.18, -34.18) * mm]});
            skFitSpline(sketch, "E556", {"points": [v(2.18, -34.18) * mm, v(2.3, -34.27) * mm, v(2.4, -34.36) * mm, v(2.5, -34.45) * mm]});
            skFitSpline(sketch, "E557", {"points": [v(2.9, -34.75) * mm, v(2.92, -34.73) * mm, v(2.93, -34.71) * mm, v(2.95, -34.68) * mm]});
            skFitSpline(sketch, "E558", {"points": [v(2.95, -34.68) * mm, v(2.97, -34.65) * mm, v(2.98, -34.6) * mm, v(2.98, -34.51) * mm]});
            skFitSpline(sketch, "E559", {"points": [v(0.84, -30.58) * mm, v(0.58, -30.28) * mm, v(0.36, -30.13) * mm, v(0.17, -30.13) * mm]});
            skFitSpline(sketch, "E560", {"points": [v(0.17, -30.13) * mm, v(0.01, -30.13) * mm, v(-0.07, -30.34) * mm, v(-0.07, -30.77) * mm]});
            skFitSpline(sketch, "E561", {"points": [v(0.85, -37.11) * mm, v(1.16, -38.88) * mm, v(1.31, -40.07) * mm, v(1.31, -40.66) * mm]});
            skFitSpline(sketch, "E562", {"points": [v(1.31, -40.66) * mm, v(1.31, -41.15) * mm, v(1.2, -41.4) * mm, v(0.96, -41.4) * mm]});
            skFitSpline(sketch, "E563", {"points": [v(0.32, -41.16) * mm, v(0.12, -41.06) * mm, v(-0.05, -40.98) * mm, v(-0.17, -40.93) * mm]});
            skFitSpline(sketch, "E564", {"points": [v(-0.17, -40.93) * mm, v(-0.3, -40.88) * mm, v(-0.44, -40.82) * mm, v(-0.6, -40.76) * mm]});
            skFitSpline(sketch, "E565", {"points": [v(-0.6, -40.76) * mm, v(-0.78, -40.7) * mm, v(-1.03, -40.66) * mm, v(-1.36, -40.66) * mm]});
            skFitSpline(sketch, "E566", {"points": [v(-1.36, -40.66) * mm, v(-1.61, -40.66) * mm, v(-1.73, -40.49) * mm, v(-1.73, -40.14) * mm]});
            skFitSpline(sketch, "E567", {"points": [v(-1.73, -40.14) * mm, v(-1.73, -39.9) * mm, v(-1.62, -39.79) * mm, v(-1.4, -39.79) * mm]});
            skFitSpline(sketch, "E568", {"points": [v(-1.4, -39.79) * mm, v(-1, -40.03) * mm, v(-0.75, -40.16) * mm, v(-0.65, -40.16) * mm]});
            skFitSpline(sketch, "E569", {"points": [v(-0.65, -40.16) * mm, v(-0.5, -40.16) * mm, v(-0.43, -40) * mm, v(-0.43, -39.67) * mm]});
            skFitSpline(sketch, "E570", {"points": [v(-1.62, -29.37) * mm, v(-1.62, -28.8) * mm, v(-1.5, -28.52) * mm, v(-1.25, -28.52) * mm]});
            skFitSpline(sketch, "E571", {"points": [v(-1.25, -28.52) * mm, v(-0.9, -28.52) * mm, v(-0.36, -28.87) * mm, v(0.38, -29.58) * mm]});
            skFitSpline(sketch, "E572", {"points": [v(0.38, -29.58) * mm, v(1.12, -30.28) * mm, v(1.49, -30.7) * mm, v(1.49, -30.85) * mm]});
            skFitSpline(sketch, "E573", {"points": [v(1.49, -30.85) * mm, v(1.49, -30.96) * mm, v(1.44, -31.02) * mm, v(1.35, -31.02) * mm]});
            skFitSpline(sketch, "E574", {"points": [v(1.35, -31.02) * mm, v(1.26, -31.02) * mm, v(1.09, -30.87) * mm, v(0.84, -30.58) * mm]});
            skFitSpline(sketch, "E575", {"points": [v(-0.94, -35.28) * mm, v(-0.83, -35.19) * mm, v(-0.72, -35.14) * mm, v(-0.6, -35.14) * mm]});
            skFitSpline(sketch, "E576", {"points": [v(-0.6, -35.14) * mm, v(-0.53, -35.15) * mm, v(-0.48, -35.19) * mm, v(-0.45, -35.24) * mm]});
            skFitSpline(sketch, "E577", {"points": [v(-0.45, -35.24) * mm, v(-0.43, -35.3) * mm, v(-0.41, -35.36) * mm, v(-0.41, -35.45) * mm]});
            skFitSpline(sketch, "E578", {"points": [v(-0.36, -35.65) * mm, v(-0.24, -35.85) * mm, v(-0.18, -36) * mm, v(-0.18, -36.1) * mm]});
            skFitSpline(sketch, "E579", {"points": [v(-2.27, -36.11) * mm, v(-3.28, -36.11) * mm, v(-3.98, -35.64) * mm, v(-4.35, -34.7) * mm]});
            skFitSpline(sketch, "E580", {"points": [v(-4.35, -34.7) * mm, v(-4.72, -33.76) * mm, v(-4.97, -32.87) * mm, v(-5.1, -32.03) * mm]});
            skFitSpline(sketch, "E581", {"points": [v(-5.1, -32.03) * mm, v(-5.24, -31.2) * mm, v(-5.3, -30.66) * mm, v(-5.32, -30.45) * mm]});
            skFitSpline(sketch, "E582", {"points": [v(-5.32, -30.45) * mm, v(-5.33, -30.24) * mm, v(-5.34, -30.04) * mm, v(-5.34, -29.84) * mm]});
            skFitSpline(sketch, "E583", {"points": [v(-5.34, -29.84) * mm, v(-5.34, -28.94) * mm, v(-5.11, -28.49) * mm, v(-4.66, -28.49) * mm]});
            skFitSpline(sketch, "E584", {"points": [v(-4.66, -28.49) * mm, v(-4.2, -28.49) * mm, v(-3.5, -29) * mm, v(-2.53, -30.03) * mm]});
            skFitSpline(sketch, "E585", {"points": [v(-1.85, -30.67) * mm, v(-1.51, -30.98) * mm, v(-1.27, -31.23) * mm, v(-1.13, -31.41) * mm]});
            skFitSpline(sketch, "E586", {"points": [v(-1.13, -31.41) * mm, v(-0.99, -31.6) * mm, v(-0.92, -31.79) * mm, v(-0.92, -32) * mm]});
            skFitSpline(sketch, "E587", {"points": [v(-0.92, -32) * mm, v(-0.92, -32.05) * mm, v(-0.95, -32.1) * mm, v(-1.02, -32.17) * mm]});
            skFitSpline(sketch, "E588", {"points": [v(-1.02, -32.17) * mm, v(-1.18, -32.17) * mm, v(-1.58, -31.8) * mm, v(-2.22, -31.05) * mm]});
            skFitSpline(sketch, "E589", {"points": [v(-2.22, -31.05) * mm, v(-2.76, -30.47) * mm, v(-3.17, -30.18) * mm, v(-3.44, -30.18) * mm]});
            skFitSpline(sketch, "E590", {"points": [v(-3.44, -30.18) * mm, v(-3.72, -30.18) * mm, v(-3.87, -30.47) * mm, v(-3.87, -31.07) * mm]});
            skFitSpline(sketch, "E591", {"points": [v(-3.87, -31.07) * mm, v(-3.87, -31.6) * mm, v(-3.78, -32.28) * mm, v(-3.6, -33.1) * mm]});
            skFitSpline(sketch, "E592", {"points": [v(-3.6, -33.1) * mm, v(-3.43, -33.93) * mm, v(-3.2, -34.56) * mm, v(-2.94, -35) * mm]});
            skFitSpline(sketch, "E593", {"points": [v(-2.94, -35) * mm, v(-2.68, -35.43) * mm, v(-2.37, -35.65) * mm, v(-2, -35.65) * mm]});
            skFitSpline(sketch, "E594", {"points": [v(-2, -35.65) * mm, v(-1.7, -35.65) * mm, v(-1.34, -35.52) * mm, v(-0.94, -35.28) * mm]});
            skFitSpline(sketch, "E595", {"points": [v(-10.8, -29.33) * mm, v(-10.91, -29.28) * mm, v(-11, -29.19) * mm, v(-11.07, -29.06) * mm]});
            skFitSpline(sketch, "E596", {"points": [v(-11.07, -29.06) * mm, v(-11.14, -28.94) * mm, v(-11.18, -28.82) * mm, v(-11.18, -28.72) * mm]});
            skFitSpline(sketch, "E597", {"points": [v(-11.18, -28.72) * mm, v(-11.18, -28.52) * mm, v(-10.98, -28.42) * mm, v(-10.6, -28.42) * mm]});
            skFitSpline(sketch, "E598", {"points": [v(-9.12, -28.55) * mm, v(-8.77, -28.55) * mm, v(-8.44, -28.64) * mm, v(-8.13, -28.8) * mm]});
            skFitSpline(sketch, "E599", {"points": [v(-8.13, -28.8) * mm, v(-7.82, -28.96) * mm, v(-7.48, -29.24) * mm, v(-7.1, -29.65) * mm]});
            skFitSpline(sketch, "E600", {"points": [v(-7.1, -29.65) * mm, v(-6.73, -30.06) * mm, v(-6.44, -30.54) * mm, v(-6.23, -31.09) * mm]});
            skFitSpline(sketch, "E601", {"points": [v(-6.23, -31.09) * mm, v(-6.03, -31.63) * mm, v(-5.88, -32.08) * mm, v(-5.79, -32.43) * mm]});
            skFitSpline(sketch, "E602", {"points": [v(-5.79, -32.43) * mm, v(-5.7, -32.78) * mm, v(-5.63, -33.1) * mm, v(-5.58, -33.38) * mm]});
            skFitSpline(sketch, "E603", {"points": [v(-5.58, -33.38) * mm, v(-5.54, -33.67) * mm, v(-5.5, -33.9) * mm, v(-5.5, -34.1) * mm]});
            skFitSpline(sketch, "E604", {"points": [v(-5.5, -34.1) * mm, v(-5.48, -34.28) * mm, v(-5.48, -34.42) * mm, v(-5.48, -34.5) * mm]});
            skFitSpline(sketch, "E605", {"points": [v(-5.48, -34.5) * mm, v(-5.48, -35.53) * mm, v(-5.76, -36.04) * mm, v(-6.33, -36.04) * mm]});
            skFitSpline(sketch, "E606", {"points": [v(-6.33, -36.04) * mm, v(-6.86, -36.04) * mm, v(-7.6, -35.55) * mm, v(-8.54, -34.56) * mm]});
            skFitSpline(sketch, "E607", {"points": [v(-9.2, -33.84) * mm, v(-9.4, -33.63) * mm, v(-9.57, -33.42) * mm, v(-9.7, -33.2) * mm]});
            skFitSpline(sketch, "E608", {"points": [v(-9.7, -33.2) * mm, v(-9.83, -32.97) * mm, v(-9.9, -32.75) * mm, v(-9.9, -32.53) * mm]});
            skFitSpline(sketch, "E609", {"points": [v(-9.9, -32.53) * mm, v(-9.9, -32.47) * mm, v(-9.87, -32.39) * mm, v(-9.82, -32.3) * mm]});
            skFitSpline(sketch, "E610", {"points": [v(-9.37, -32.84) * mm, v(-9.1, -33.22) * mm, v(-8.78, -33.61) * mm, v(-8.4, -34) * mm]});
            skFitSpline(sketch, "E611", {"points": [v(-8.4, -34) * mm, v(-8.03, -34.4) * mm, v(-7.7, -34.6) * mm, v(-7.43, -34.6) * mm]});
            skFitSpline(sketch, "E612", {"points": [v(-7.43, -34.6) * mm, v(-7.11, -34.6) * mm, v(-6.95, -34.26) * mm, v(-6.95, -33.58) * mm]});
            skFitSpline(sketch, "E613", {"points": [v(-6.95, -33.58) * mm, v(-6.95, -33.1) * mm, v(-7.02, -32.5) * mm, v(-7.15, -31.8) * mm]});
            skFitSpline(sketch, "E614", {"points": [v(-7.15, -31.8) * mm, v(-7.29, -31.1) * mm, v(-7.44, -30.58) * mm, v(-7.62, -30.24) * mm]});
            skFitSpline(sketch, "E615", {"points": [v(-7.62, -30.24) * mm, v(-7.8, -29.9) * mm, v(-7.98, -29.68) * mm, v(-8.18, -29.57) * mm]});
            skFitSpline(sketch, "E616", {"points": [v(-8.18, -29.57) * mm, v(-8.38, -29.46) * mm, v(-8.61, -29.4) * mm, v(-8.87, -29.4) * mm]});
            skFitSpline(sketch, "E617", {"points": [v(-11.29, -29.14) * mm, v(-11.29, -28.69) * mm, v(-11.15, -28.46) * mm, v(-10.86, -28.46) * mm]});
            skFitSpline(sketch, "E618", {"points": [v(-10.86, -28.46) * mm, v(-10.7, -28.46) * mm, v(-10.52, -28.55) * mm, v(-10.3, -28.73) * mm]});
            skFitSpline(sketch, "E619", {"points": [v(-10.3, -28.73) * mm, v(-10.11, -28.93) * mm, v(-9.95, -29.18) * mm, v(-9.83, -29.48) * mm]});
            skFitSpline(sketch, "E620", {"points": [v(-9.83, -29.48) * mm, v(-9.7, -29.78) * mm, v(-9.62, -30.05) * mm, v(-9.57, -30.28) * mm]});
            skFitSpline(sketch, "E621", {"points": [v(-9.57, -30.28) * mm, v(-9.52, -30.5) * mm, v(-9.48, -30.78) * mm, v(-9.46, -31.1) * mm]});
            skFitSpline(sketch, "E622", {"points": [v(-8.99, -35.3) * mm, v(-8.99, -35.79) * mm, v(-9.1, -36.03) * mm, v(-9.32, -36.03) * mm]});
            skFitSpline(sketch, "E623", {"points": [v(-9.32, -36.03) * mm, v(-9.52, -36.03) * mm, v(-9.8, -35.88) * mm, v(-10.17, -35.6) * mm]});
            skFitSpline(sketch, "E624", {"points": [v(-10.17, -35.6) * mm, v(-10.53, -35.35) * mm, v(-11.12, -34.87) * mm, v(-11.93, -34.14) * mm]});
            skFitSpline(sketch, "E625", {"points": [v(-11.93, -34.14) * mm, v(-11.99, -34.08) * mm, v(-12.02, -34.03) * mm, v(-12.05, -33.99) * mm]});
            skFitSpline(sketch, "E626", {"points": [v(-12.05, -33.99) * mm, v(-12.08, -33.95) * mm, v(-12.1, -33.91) * mm, v(-12.1, -33.87) * mm]});
            skFitSpline(sketch, "E627", {"points": [v(-12.1, -33.87) * mm, v(-12.1, -33.85) * mm, v(-12.08, -33.81) * mm, v(-12.01, -33.78) * mm]});
            skFitSpline(sketch, "E628", {"points": [v(-12.01, -33.78) * mm, v(-11.92, -33.78) * mm, v(-11.8, -33.82) * mm, v(-11.67, -33.91) * mm]});
            skFitSpline(sketch, "E629", {"points": [v(-11.67, -33.91) * mm, v(-11.54, -34) * mm, v(-11.41, -34.1) * mm, v(-11.3, -34.18) * mm]});
            skFitSpline(sketch, "E630", {"points": [v(-11.3, -34.18) * mm, v(-11.18, -34.27) * mm, v(-11.07, -34.36) * mm, v(-10.98, -34.45) * mm]});
            skFitSpline(sketch, "E631", {"points": [v(-10.58, -34.75) * mm, v(-10.56, -34.73) * mm, v(-10.55, -34.71) * mm, v(-10.53, -34.68) * mm]});
            skFitSpline(sketch, "E632", {"points": [v(-10.53, -34.68) * mm, v(-10.5, -34.65) * mm, v(-10.5, -34.6) * mm, v(-10.5, -34.51) * mm]});
            skFitSpline(sketch, "E633", {"points": [v(-15.04, -33.96) * mm, v(-14.75, -34.25) * mm, v(-14.54, -34.4) * mm, v(-14.4, -34.4) * mm]});
            skFitSpline(sketch, "E634", {"points": [v(-14.4, -34.4) * mm, v(-14.24, -34.4) * mm, v(-14.16, -34.18) * mm, v(-14.16, -33.74) * mm]});
            skFitSpline(sketch, "E635", {"points": [v(-15.08, -27.43) * mm, v(-15.46, -25.24) * mm, v(-15.66, -23.89) * mm, v(-15.66, -23.38) * mm]});
            skFitSpline(sketch, "E636", {"points": [v(-15.66, -23.38) * mm, v(-15.66, -22.98) * mm, v(-15.57, -22.78) * mm, v(-15.39, -22.78) * mm]});
            skFitSpline(sketch, "E637", {"points": [v(-15.39, -22.78) * mm, v(-15.26, -22.78) * mm, v(-15.13, -22.83) * mm, v(-15, -22.92) * mm]});
            skFitSpline(sketch, "E638", {"points": [v(-14.03, -23.56) * mm, v(-13.56, -23.88) * mm, v(-13.19, -24.12) * mm, v(-12.9, -24.28) * mm]});
            skFitSpline(sketch, "E639", {"points": [v(-12.9, -24.28) * mm, v(-12.62, -24.44) * mm, v(-12.48, -24.6) * mm, v(-12.48, -24.72) * mm]});
            skFitSpline(sketch, "E640", {"points": [v(-12.48, -24.72) * mm, v(-12.5, -24.82) * mm, v(-12.55, -24.87) * mm, v(-12.63, -24.87) * mm]});
            skFitSpline(sketch, "E641", {"points": [v(-12.86, -24.8) * mm, v(-13.36, -24.5) * mm, v(-13.64, -24.35) * mm, v(-13.72, -24.35) * mm]});
            skFitSpline(sketch, "E642", {"points": [v(-13.72, -24.35) * mm, v(-13.85, -24.35) * mm, v(-13.91, -24.49) * mm, v(-13.91, -24.76) * mm]});
            skFitSpline(sketch, "E643", {"points": [v(-12.55, -35.39) * mm, v(-12.55, -35.9) * mm, v(-12.67, -36.16) * mm, v(-12.9, -36.16) * mm]});
            skFitSpline(sketch, "E644", {"points": [v(-12.9, -36.16) * mm, v(-13.25, -36.16) * mm, v(-13.82, -35.77) * mm, v(-14.6, -35) * mm]});
            skFitSpline(sketch, "E645", {"points": [v(-14.6, -35) * mm, v(-15.37, -34.22) * mm, v(-15.75, -33.78) * mm, v(-15.75, -33.66) * mm]});
            skFitSpline(sketch, "E646", {"points": [v(-15.75, -33.66) * mm, v(-15.75, -33.57) * mm, v(-15.7, -33.52) * mm, v(-15.6, -33.52) * mm]});
            skFitSpline(sketch, "E647", {"points": [v(-15.6, -33.52) * mm, v(-15.5, -33.52) * mm, v(-15.32, -33.67) * mm, v(-15.04, -33.96) * mm]});
            skFitSpline(sketch, "E648", {"points": [v(-18.37, -28.75) * mm, v(-17.76, -28.96) * mm, v(-17.33, -29.2) * mm, v(-17.05, -29.48) * mm]});
            skFitSpline(sketch, "E649", {"points": [v(-17.05, -29.48) * mm, v(-16.78, -29.75) * mm, v(-16.52, -30.34) * mm, v(-16.26, -31.23) * mm]});
            skFitSpline(sketch, "E650", {"points": [v(-16.26, -31.23) * mm, v(-16, -32.12) * mm, v(-15.87, -32.85) * mm, v(-15.87, -33.43) * mm]});
            skFitSpline(sketch, "E651", {"points": [v(-15.87, -33.43) * mm, v(-15.87, -34.16) * mm, v(-16.02, -34.78) * mm, v(-16.32, -35.3) * mm]});
            skFitSpline(sketch, "E652", {"points": [v(-16.32, -35.3) * mm, v(-16.61, -35.8) * mm, v(-17.03, -36.06) * mm, v(-17.56, -36.06) * mm]});
            skFitSpline(sketch, "E653", {"points": [v(-17.56, -36.06) * mm, v(-18.1, -36.06) * mm, v(-18.62, -35.9) * mm, v(-19.13, -35.54) * mm]});
            skFitSpline(sketch, "E654", {"points": [v(-20.12, -34.9) * mm, v(-20.3, -34.79) * mm, v(-20.45, -34.68) * mm, v(-20.58, -34.57) * mm]});
            skFitSpline(sketch, "E655", {"points": [v(-20.58, -34.57) * mm, v(-20.71, -34.46) * mm, v(-20.84, -34.34) * mm, v(-20.97, -34.2) * mm]});
            skFitSpline(sketch, "E656", {"points": [v(-20.97, -34.2) * mm, v(-21.1, -34.08) * mm, v(-21.2, -33.86) * mm, v(-21.26, -33.55) * mm]});
            skFitSpline(sketch, "E657", {"points": [v(-21.79, -30.84) * mm, v(-21.79, -30.26) * mm, v(-21.54, -29.7) * mm, v(-21.06, -29.17) * mm]});
            skFitSpline(sketch, "E658", {"points": [v(-21.06, -29.17) * mm, v(-20.57, -28.63) * mm, v(-20.16, -28.37) * mm, v(-19.8, -28.37) * mm]});
            skFitSpline(sketch, "E659", {"points": [v(-18, -30.05) * mm, v(-18.1, -29.8) * mm, v(-18.2, -29.6) * mm, v(-18.3, -29.45) * mm]});
            skFitSpline(sketch, "E660", {"points": [v(-18.3, -29.45) * mm, v(-18.42, -29.32) * mm, v(-18.52, -29.24) * mm, v(-18.58, -29.2) * mm]});
            skFitSpline(sketch, "E661", {"points": [v(-18.58, -29.2) * mm, v(-18.63, -29.16) * mm, v(-18.7, -29.11) * mm, v(-18.79, -29.05) * mm]});
            skFitSpline(sketch, "E662", {"points": [v(-18.79, -29.05) * mm, v(-18.87, -29) * mm, v(-18.97, -28.97) * mm, v(-19.1, -28.97) * mm]});
            skFitSpline(sketch, "E663", {"points": [v(-19.1, -28.97) * mm, v(-19.3, -28.97) * mm, v(-19.5, -29.07) * mm, v(-19.68, -29.29) * mm]});
            skFitSpline(sketch, "E664", {"points": [v(-19.68, -29.29) * mm, v(-19.86, -29.5) * mm, v(-19.96, -29.73) * mm, v(-20, -29.97) * mm]});
            skFitSpline(sketch, "E665", {"points": [v(-20, -29.97) * mm, v(-20.1, -30.43) * mm, v(-20.16, -30.87) * mm, v(-20.16, -31.31) * mm]});
            skFitSpline(sketch, "E666", {"points": [v(-20.16, -31.31) * mm, v(-20.16, -32.05) * mm, v(-20.07, -32.74) * mm, v(-19.9, -33.39) * mm]});
            skFitSpline(sketch, "E667", {"points": [v(-19.9, -33.39) * mm, v(-19.74, -34.03) * mm, v(-19.53, -34.46) * mm, v(-19.3, -34.68) * mm]});
            skFitSpline(sketch, "E668", {"points": [v(-19.3, -34.68) * mm, v(-19.05, -34.9) * mm, v(-18.89, -35) * mm, v(-18.8, -35) * mm]});
            skFitSpline(sketch, "E669", {"points": [v(-18.8, -35) * mm, v(-18.64, -35) * mm, v(-18.45, -34.92) * mm, v(-18.2, -34.77) * mm]});
            skFitSpline(sketch, "E670", {"points": [v(-18.2, -34.77) * mm, v(-17.97, -34.61) * mm, v(-17.78, -34.33) * mm, v(-17.65, -33.91) * mm]});
            skFitSpline(sketch, "E671", {"points": [v(-17.65, -33.91) * mm, v(-17.5, -33.5) * mm, v(-17.44, -33.04) * mm, v(-17.44, -32.53) * mm]});
            skFitSpline(sketch, "E672", {"points": [v(-17.44, -32.53) * mm, v(-17.44, -32.15) * mm, v(-17.47, -31.86) * mm, v(-17.54, -31.66) * mm]});
            skFitSpline(sketch, "E673", {"points": [v(-24.75, -28.75) * mm, v(-24.15, -28.96) * mm, v(-23.7, -29.2) * mm, v(-23.43, -29.48) * mm]});
            skFitSpline(sketch, "E674", {"points": [v(-23.43, -29.48) * mm, v(-23.16, -29.75) * mm, v(-22.9, -30.34) * mm, v(-22.64, -31.23) * mm]});
            skFitSpline(sketch, "E675", {"points": [v(-22.64, -31.23) * mm, v(-22.38, -32.12) * mm, v(-22.25, -32.85) * mm, v(-22.25, -33.43) * mm]});
            skFitSpline(sketch, "E676", {"points": [v(-22.25, -33.43) * mm, v(-22.25, -34.16) * mm, v(-22.4, -34.78) * mm, v(-22.7, -35.3) * mm]});
            skFitSpline(sketch, "E677", {"points": [v(-22.7, -35.3) * mm, v(-23, -35.8) * mm, v(-23.4, -36.06) * mm, v(-23.94, -36.06) * mm]});
            skFitSpline(sketch, "E678", {"points": [v(-23.94, -36.06) * mm, v(-24.48, -36.06) * mm, v(-25, -35.9) * mm, v(-25.5, -35.54) * mm]});
            skFitSpline(sketch, "E679", {"points": [v(-26.5, -34.9) * mm, v(-26.68, -34.79) * mm, v(-26.83, -34.68) * mm, v(-26.96, -34.57) * mm]});
            skFitSpline(sketch, "E680", {"points": [v(-26.96, -34.57) * mm, v(-27.1, -34.46) * mm, v(-27.22, -34.34) * mm, v(-27.35, -34.2) * mm]});
            skFitSpline(sketch, "E681", {"points": [v(-27.35, -34.2) * mm, v(-27.48, -34.08) * mm, v(-27.58, -33.86) * mm, v(-27.64, -33.55) * mm]});
            skFitSpline(sketch, "E682", {"points": [v(-28.17, -30.84) * mm, v(-28.17, -30.26) * mm, v(-27.92, -29.7) * mm, v(-27.44, -29.17) * mm]});
            skFitSpline(sketch, "E683", {"points": [v(-27.44, -29.17) * mm, v(-26.95, -28.63) * mm, v(-26.54, -28.37) * mm, v(-26.19, -28.37) * mm]});
            skFitSpline(sketch, "E684", {"points": [v(-24.38, -30.05) * mm, v(-24.48, -29.8) * mm, v(-24.57, -29.6) * mm, v(-24.68, -29.45) * mm]});
            skFitSpline(sketch, "E685", {"points": [v(-24.68, -29.45) * mm, v(-24.8, -29.32) * mm, v(-24.9, -29.24) * mm, v(-24.96, -29.2) * mm]});
            skFitSpline(sketch, "E686", {"points": [v(-24.96, -29.2) * mm, v(-25.02, -29.16) * mm, v(-25.09, -29.11) * mm, v(-25.17, -29.05) * mm]});
            skFitSpline(sketch, "E687", {"points": [v(-25.17, -29.05) * mm, v(-25.25, -29) * mm, v(-25.35, -28.97) * mm, v(-25.47, -28.97) * mm]});
            skFitSpline(sketch, "E688", {"points": [v(-25.47, -28.97) * mm, v(-25.7, -28.97) * mm, v(-25.89, -29.07) * mm, v(-26.06, -29.29) * mm]});
            skFitSpline(sketch, "E689", {"points": [v(-26.06, -29.29) * mm, v(-26.24, -29.5) * mm, v(-26.34, -29.73) * mm, v(-26.38, -29.97) * mm]});
            skFitSpline(sketch, "E690", {"points": [v(-26.38, -29.97) * mm, v(-26.49, -30.43) * mm, v(-26.54, -30.87) * mm, v(-26.54, -31.31) * mm]});
            skFitSpline(sketch, "E691", {"points": [v(-26.54, -31.31) * mm, v(-26.54, -32.05) * mm, v(-26.45, -32.74) * mm, v(-26.29, -33.39) * mm]});
            skFitSpline(sketch, "E692", {"points": [v(-26.29, -33.39) * mm, v(-26.12, -34.03) * mm, v(-25.91, -34.46) * mm, v(-25.67, -34.68) * mm]});
            skFitSpline(sketch, "E693", {"points": [v(-25.67, -34.68) * mm, v(-25.43, -34.9) * mm, v(-25.27, -35) * mm, v(-25.18, -35) * mm]});
            skFitSpline(sketch, "E694", {"points": [v(-25.18, -35) * mm, v(-25.02, -35) * mm, v(-24.83, -34.92) * mm, v(-24.59, -34.77) * mm]});
            skFitSpline(sketch, "E695", {"points": [v(-24.59, -34.77) * mm, v(-24.35, -34.61) * mm, v(-24.16, -34.33) * mm, v(-24.03, -33.91) * mm]});
            skFitSpline(sketch, "E696", {"points": [v(-24.03, -33.91) * mm, v(-23.9, -33.5) * mm, v(-23.82, -33.04) * mm, v(-23.82, -32.53) * mm]});
            skFitSpline(sketch, "E697", {"points": [v(-23.82, -32.53) * mm, v(-23.82, -32.15) * mm, v(-23.85, -31.86) * mm, v(-23.92, -31.66) * mm]});
            skFitSpline(sketch, "E698", {"points": [v(-29.49, -30.2) * mm, v(-29.52, -29.94) * mm, v(-29.64, -29.77) * mm, v(-29.82, -29.71) * mm]});
            skFitSpline(sketch, "E699", {"points": [v(-29.82, -29.71) * mm, v(-30.01, -29.65) * mm, v(-30.34, -29.63) * mm, v(-30.82, -29.63) * mm]});
            skFitSpline(sketch, "E700", {"points": [v(-32.6, -29.59) * mm, v(-32.3, -30.26) * mm, v(-31.89, -31) * mm, v(-31.38, -31.82) * mm]});
            skFitSpline(sketch, "E701", {"points": [v(-31.38, -31.82) * mm, v(-30.87, -32.63) * mm, v(-30.37, -33.32) * mm, v(-29.9, -33.87) * mm]});
            skFitSpline(sketch, "E702", {"points": [v(-29.9, -33.87) * mm, v(-29.43, -34.43) * mm, v(-28.81, -35.04) * mm, v(-28.05, -35.7) * mm]});
            skFitSpline(sketch, "E703", {"points": [v(-28.34, -36) * mm, v(-28.77, -35.68) * mm, v(-29.35, -35.2) * mm, v(-30.1, -34.53) * mm]});
            skFitSpline(sketch, "E704", {"points": [v(-30.1, -34.53) * mm, v(-30.84, -33.87) * mm, v(-31.53, -33.1) * mm, v(-32.16, -32.19) * mm]});
            skFitSpline(sketch, "E705", {"points": [v(-34.28, -28.64) * mm, v(-34.3, -28.6) * mm, v(-34.31, -28.54) * mm, v(-34.31, -28.46) * mm]});
            skFitSpline(sketch, "E706", {"points": [v(-34.31, -28.46) * mm, v(-34.31, -28.37) * mm, v(-34.27, -28.33) * mm, v(-34.18, -28.33) * mm]});
            skFitSpline(sketch, "E707", {"points": [v(-34.02, -28.38) * mm, v(-33.87, -28.5) * mm, v(-33.58, -28.56) * mm, v(-33.17, -28.56) * mm]});
            skFitSpline(sketch, "E708", {"points": [v(-30.4, -28.23) * mm, v(-30.06, -28.23) * mm, v(-29.8, -28.29) * mm, v(-29.6, -28.4) * mm]});
            skFitSpline(sketch, "E709", {"points": [v(-29.6, -28.4) * mm, v(-29.4, -28.52) * mm, v(-29.28, -28.65) * mm, v(-29.22, -28.8) * mm]});
            skFitSpline(sketch, "E710", {"points": [v(-29.22, -28.8) * mm, v(-29.17, -28.93) * mm, v(-29.12, -29.12) * mm, v(-29.1, -29.33) * mm]});
            skFitSpline(sketch, "E711", {"points": [v(-29.02, -30) * mm, v(-29.02, -30.4) * mm, v(-29.1, -30.61) * mm, v(-29.23, -30.61) * mm]});
            skFitSpline(sketch, "E712", {"points": [v(-29.23, -30.61) * mm, v(-29.36, -30.61) * mm, v(-29.45, -30.48) * mm, v(-29.49, -30.2) * mm]});
            skFitSpline(sketch, "E713", {"points": [v(-28.22, -35.85) * mm, v(-28.25, -35.88) * mm, v(-28.3, -35.9) * mm, v(-28.4, -35.95) * mm]});
            skFitSpline(sketch, "E714", {"points": [v(-29.27, -35.27) * mm, v(-29.45, -35.15) * mm, v(-29.62, -35.1) * mm, v(-29.78, -35.1) * mm]});
            skFitSpline(sketch, "E715", {"points": [v(-29.78, -35.1) * mm, v(-30.02, -35.1) * mm, v(-30.42, -35.3) * mm, v(-30.96, -35.68) * mm]});
            skFitSpline(sketch, "E716", {"points": [v(-30.96, -35.68) * mm, v(-31.27, -35.94) * mm, v(-31.63, -36.06) * mm, v(-32.03, -36.06) * mm]});
            skFitSpline(sketch, "E717", {"points": [v(-32.03, -36.06) * mm, v(-32.43, -36.06) * mm, v(-32.81, -35.93) * mm, v(-33.19, -35.66) * mm]});
            skFitSpline(sketch, "E718", {"points": [v(-33.19, -35.66) * mm, v(-33.56, -35.4) * mm, v(-33.83, -35.1) * mm, v(-33.98, -34.79) * mm]});
            skFitSpline(sketch, "E719", {"points": [v(-33.98, -34.79) * mm, v(-34.14, -34.47) * mm, v(-34.22, -34.25) * mm, v(-34.22, -34.12) * mm]});
            skFitSpline(sketch, "E720", {"points": [v(-34.22, -34.12) * mm, v(-34.22, -34.07) * mm, v(-34.19, -34.02) * mm, v(-34.12, -33.97) * mm]});
            skFitSpline(sketch, "E721", {"points": [v(-34.12, -33.97) * mm, v(-34, -33.97) * mm, v(-33.9, -34.05) * mm, v(-33.83, -34.22) * mm]});
            skFitSpline(sketch, "E722", {"points": [v(-33.83, -34.22) * mm, v(-33.56, -34.62) * mm, v(-33.23, -34.82) * mm, v(-32.84, -34.82) * mm]});
            skFitSpline(sketch, "E723", {"points": [v(-32.84, -34.82) * mm, v(-32.71, -34.82) * mm, v(-32.6, -34.81) * mm, v(-32.48, -34.78) * mm]});
            skFitSpline(sketch, "E724", {"points": [v(-32.48, -34.78) * mm, v(-32.37, -34.76) * mm, v(-32.25, -34.72) * mm, v(-32.12, -34.67) * mm]});
            skFitSpline(sketch, "E725", {"points": [v(-30.22, -33.8) * mm, v(-30.1, -33.74) * mm, v(-29.98, -33.72) * mm, v(-29.83, -33.72) * mm]});
            skFitSpline(sketch, "E726", {"points": [v(-29.83, -33.72) * mm, v(-29.5, -33.72) * mm, v(-29.2, -33.86) * mm, v(-28.91, -34.13) * mm]});
            skFitSpline(sketch, "E727", {"points": [v(-28.91, -34.13) * mm, v(-28.64, -34.41) * mm, v(-28.45, -34.73) * mm, v(-28.36, -35.08) * mm]});
            skFitSpline(sketch, "E728", {"points": [v(-39.76, -29.33) * mm, v(-39.87, -29.28) * mm, v(-39.95, -29.19) * mm, v(-40.03, -29.06) * mm]});
            skFitSpline(sketch, "E729", {"points": [v(-40.03, -29.06) * mm, v(-40.1, -28.94) * mm, v(-40.13, -28.82) * mm, v(-40.13, -28.72) * mm]});
            skFitSpline(sketch, "E730", {"points": [v(-40.13, -28.72) * mm, v(-40.13, -28.52) * mm, v(-39.94, -28.42) * mm, v(-39.55, -28.42) * mm]});
            skFitSpline(sketch, "E731", {"points": [v(-38.08, -28.55) * mm, v(-37.73, -28.55) * mm, v(-37.4, -28.64) * mm, v(-37.09, -28.8) * mm]});
            skFitSpline(sketch, "E732", {"points": [v(-37.09, -28.8) * mm, v(-36.78, -28.96) * mm, v(-36.43, -29.24) * mm, v(-36.06, -29.65) * mm]});
            skFitSpline(sketch, "E733", {"points": [v(-36.06, -29.65) * mm, v(-35.68, -30.06) * mm, v(-35.4, -30.54) * mm, v(-35.19, -31.09) * mm]});
            skFitSpline(sketch, "E734", {"points": [v(-35.19, -31.09) * mm, v(-34.98, -31.63) * mm, v(-34.83, -32.08) * mm, v(-34.74, -32.43) * mm]});
            skFitSpline(sketch, "E735", {"points": [v(-34.74, -32.43) * mm, v(-34.65, -32.78) * mm, v(-34.58, -33.1) * mm, v(-34.54, -33.38) * mm]});
            skFitSpline(sketch, "E736", {"points": [v(-34.54, -33.38) * mm, v(-34.5, -33.67) * mm, v(-34.46, -33.9) * mm, v(-34.45, -34.1) * mm]});
            skFitSpline(sketch, "E737", {"points": [v(-34.45, -34.1) * mm, v(-34.44, -34.28) * mm, v(-34.43, -34.42) * mm, v(-34.43, -34.5) * mm]});
            skFitSpline(sketch, "E738", {"points": [v(-34.43, -34.5) * mm, v(-34.43, -35.53) * mm, v(-34.71, -36.04) * mm, v(-35.28, -36.04) * mm]});
            skFitSpline(sketch, "E739", {"points": [v(-35.28, -36.04) * mm, v(-35.81, -36.04) * mm, v(-36.55, -35.55) * mm, v(-37.5, -34.56) * mm]});
            skFitSpline(sketch, "E740", {"points": [v(-38.15, -33.84) * mm, v(-38.36, -33.63) * mm, v(-38.53, -33.42) * mm, v(-38.66, -33.2) * mm]});
            skFitSpline(sketch, "E741", {"points": [v(-38.66, -33.2) * mm, v(-38.79, -32.97) * mm, v(-38.85, -32.75) * mm, v(-38.85, -32.53) * mm]});
            skFitSpline(sketch, "E742", {"points": [v(-38.85, -32.53) * mm, v(-38.85, -32.47) * mm, v(-38.83, -32.39) * mm, v(-38.77, -32.3) * mm]});
            skFitSpline(sketch, "E743", {"points": [v(-38.33, -32.84) * mm, v(-38.06, -33.22) * mm, v(-37.73, -33.61) * mm, v(-37.36, -34) * mm]});
            skFitSpline(sketch, "E744", {"points": [v(-37.36, -34) * mm, v(-36.98, -34.4) * mm, v(-36.66, -34.6) * mm, v(-36.39, -34.6) * mm]});
            skFitSpline(sketch, "E745", {"points": [v(-36.39, -34.6) * mm, v(-36.07, -34.6) * mm, v(-35.9, -34.26) * mm, v(-35.9, -33.58) * mm]});
            skFitSpline(sketch, "E746", {"points": [v(-35.9, -33.58) * mm, v(-35.9, -33.1) * mm, v(-35.97, -32.5) * mm, v(-36.1, -31.8) * mm]});
            skFitSpline(sketch, "E747", {"points": [v(-36.1, -31.8) * mm, v(-36.24, -31.1) * mm, v(-36.4, -30.58) * mm, v(-36.57, -30.24) * mm]});
            skFitSpline(sketch, "E748", {"points": [v(-36.57, -30.24) * mm, v(-36.75, -29.9) * mm, v(-36.94, -29.68) * mm, v(-37.14, -29.57) * mm]});
            skFitSpline(sketch, "E749", {"points": [v(-37.14, -29.57) * mm, v(-37.34, -29.46) * mm, v(-37.57, -29.4) * mm, v(-37.82, -29.4) * mm]});
            skFitSpline(sketch, "E750", {"points": [v(-40.24, -29.14) * mm, v(-40.24, -28.69) * mm, v(-40.1, -28.46) * mm, v(-39.82, -28.46) * mm]});
            skFitSpline(sketch, "E751", {"points": [v(-39.82, -28.46) * mm, v(-39.66, -28.46) * mm, v(-39.48, -28.55) * mm, v(-39.26, -28.73) * mm]});
            skFitSpline(sketch, "E752", {"points": [v(-39.26, -28.73) * mm, v(-39.07, -28.93) * mm, v(-38.9, -29.18) * mm, v(-38.79, -29.48) * mm]});
            skFitSpline(sketch, "E753", {"points": [v(-38.79, -29.48) * mm, v(-38.66, -29.78) * mm, v(-38.58, -30.05) * mm, v(-38.53, -30.28) * mm]});
            skFitSpline(sketch, "E754", {"points": [v(-38.53, -30.28) * mm, v(-38.47, -30.5) * mm, v(-38.44, -30.78) * mm, v(-38.41, -31.1) * mm]});
            skFitSpline(sketch, "E755", {"points": [v(-37.94, -35.3) * mm, v(-37.94, -35.79) * mm, v(-38.05, -36.03) * mm, v(-38.27, -36.03) * mm]});
            skFitSpline(sketch, "E756", {"points": [v(-38.27, -36.03) * mm, v(-38.48, -36.03) * mm, v(-38.76, -35.88) * mm, v(-39.12, -35.6) * mm]});
            skFitSpline(sketch, "E757", {"points": [v(-39.12, -35.6) * mm, v(-39.49, -35.35) * mm, v(-40.07, -34.87) * mm, v(-40.89, -34.14) * mm]});
            skFitSpline(sketch, "E758", {"points": [v(-40.89, -34.14) * mm, v(-40.94, -34.08) * mm, v(-40.98, -34.03) * mm, v(-41, -33.99) * mm]});
            skFitSpline(sketch, "E759", {"points": [v(-41, -33.99) * mm, v(-41.03, -33.95) * mm, v(-41.05, -33.91) * mm, v(-41.06, -33.87) * mm]});
            skFitSpline(sketch, "E760", {"points": [v(-41.06, -33.87) * mm, v(-41.06, -33.85) * mm, v(-41.03, -33.81) * mm, v(-40.97, -33.78) * mm]});
            skFitSpline(sketch, "E761", {"points": [v(-40.97, -33.78) * mm, v(-40.88, -33.78) * mm, v(-40.76, -33.82) * mm, v(-40.63, -33.91) * mm]});
            skFitSpline(sketch, "E762", {"points": [v(-40.63, -33.91) * mm, v(-40.5, -34) * mm, v(-40.37, -34.1) * mm, v(-40.25, -34.18) * mm]});
            skFitSpline(sketch, "E763", {"points": [v(-40.25, -34.18) * mm, v(-40.13, -34.27) * mm, v(-40.03, -34.36) * mm, v(-39.94, -34.45) * mm]});
            skFitSpline(sketch, "E764", {"points": [v(-39.53, -34.75) * mm, v(-39.52, -34.73) * mm, v(-39.5, -34.71) * mm, v(-39.48, -34.68) * mm]});
            skFitSpline(sketch, "E765", {"points": [v(-39.48, -34.68) * mm, v(-39.46, -34.65) * mm, v(-39.45, -34.6) * mm, v(-39.45, -34.51) * mm]});
            skFitSpline(sketch, "E766", {"points": [v(22.3, -54) * mm, v(22.86, -53.32) * mm, v(23.74, -52.78) * mm, v(24.93, -52.38) * mm]});
            skFitSpline(sketch, "E767", {"points": [v(24.93, -52.38) * mm, v(25.54, -52.18) * mm, v(26.1, -52.02) * mm, v(26.63, -51.9) * mm]});
            skFitSpline(sketch, "E768", {"points": [v(26.63, -51.9) * mm, v(27.16, -51.8) * mm, v(27.71, -51.68) * mm, v(28.28, -51.56) * mm]});
            skFitSpline(sketch, "E769", {"points": [v(28.28, -51.56) * mm, v(29.15, -51.37) * mm, v(29.75, -51.17) * mm, v(30.06, -50.94) * mm]});
            skFitSpline(sketch, "E770", {"points": [v(30.06, -50.94) * mm, v(30.37, -50.72) * mm, v(30.53, -50.4) * mm, v(30.53, -49.98) * mm]});
            skFitSpline(sketch, "E771", {"points": [v(30.53, -49.98) * mm, v(30.53, -49.7) * mm, v(30.43, -49.45) * mm, v(30.24, -49.23) * mm]});
            skFitSpline(sketch, "E772", {"points": [v(30.24, -49.23) * mm, v(30.04, -49.02) * mm, v(29.8, -48.86) * mm, v(29.54, -48.75) * mm]});
            skFitSpline(sketch, "E773", {"points": [v(29.54, -48.75) * mm, v(29.23, -48.62) * mm, v(28.91, -48.53) * mm, v(28.58, -48.49) * mm]});
            skFitSpline(sketch, "E774", {"points": [v(28.58, -48.49) * mm, v(28.25, -48.44) * mm, v(27.92, -48.42) * mm, v(27.58, -48.42) * mm]});
            skFitSpline(sketch, "E775", {"points": [v(27.58, -48.42) * mm, v(26.63, -48.42) * mm, v(25.7, -48.6) * mm, v(24.8, -48.94) * mm]});
            skFitSpline(sketch, "E776", {"points": [v(24.8, -48.94) * mm, v(23.88, -49.28) * mm, v(23.11, -49.7) * mm, v(22.49, -50.22) * mm]});
            skFitSpline(sketch, "E777", {"points": [v(22.06, -46.56) * mm, v(22.8, -46.25) * mm, v(23.66, -46) * mm, v(24.66, -45.8) * mm]});
            skFitSpline(sketch, "E778", {"points": [v(24.66, -45.8) * mm, v(25.66, -45.6) * mm, v(26.67, -45.5) * mm, v(27.7, -45.5) * mm]});
            skFitSpline(sketch, "E779", {"points": [v(27.7, -45.5) * mm, v(29.74, -45.5) * mm, v(31.41, -45.96) * mm, v(32.71, -46.9) * mm]});
            skFitSpline(sketch, "E780", {"points": [v(32.71, -46.9) * mm, v(34.01, -47.83) * mm, v(34.66, -49.04) * mm, v(34.66, -50.52) * mm]});
            skFitSpline(sketch, "E781", {"points": [v(34.66, -50.52) * mm, v(34.66, -51.62) * mm, v(34.38, -52.55) * mm, v(33.8, -53.29) * mm]});
            skFitSpline(sketch, "E782", {"points": [v(33.8, -53.29) * mm, v(33.23, -54.03) * mm, v(32.28, -54.62) * mm, v(30.97, -55.06) * mm]});
            skFitSpline(sketch, "E783", {"points": [v(30.97, -55.06) * mm, v(30.4, -55.25) * mm, v(29.79, -55.4) * mm, v(29.13, -55.53) * mm]});
            skFitSpline(sketch, "E784", {"points": [v(29.13, -55.53) * mm, v(28.48, -55.66) * mm, v(27.86, -55.79) * mm, v(27.28, -55.93) * mm]});
            skFitSpline(sketch, "E785", {"points": [v(27.28, -55.93) * mm, v(26.72, -56.07) * mm, v(26.3, -56.26) * mm, v(26, -56.51) * mm]});
            skFitSpline(sketch, "E786", {"points": [v(26, -56.51) * mm, v(25.72, -56.77) * mm, v(25.57, -57.07) * mm, v(25.57, -57.42) * mm]});
            skFitSpline(sketch, "E787", {"points": [v(25.57, -57.42) * mm, v(25.57, -57.8) * mm, v(25.67, -58.08) * mm, v(25.87, -58.27) * mm]});
            skFitSpline(sketch, "E788", {"points": [v(25.87, -58.27) * mm, v(26.07, -58.46) * mm, v(26.32, -58.62) * mm, v(26.63, -58.75) * mm]});
            skFitSpline(sketch, "E789", {"points": [v(26.63, -58.75) * mm, v(26.88, -58.85) * mm, v(27.2, -58.92) * mm, v(27.6, -58.96) * mm]});
            skFitSpline(sketch, "E790", {"points": [v(27.6, -58.96) * mm, v(28, -59) * mm, v(28.32, -59.03) * mm, v(28.56, -59.03) * mm]});
            skFitSpline(sketch, "E791", {"points": [v(28.56, -59.03) * mm, v(29.51, -59.03) * mm, v(30.5, -58.85) * mm, v(31.53, -58.48) * mm]});
            skFitSpline(sketch, "E792", {"points": [v(31.53, -58.48) * mm, v(32.56, -58.12) * mm, v(33.49, -57.6) * mm, v(34.32, -56.92) * mm]});
            skFitSpline(sketch, "E793", {"points": [v(34.76, -60.73) * mm, v(33.92, -61.1) * mm, v(33.02, -61.38) * mm, v(32.06, -61.62) * mm]});
            skFitSpline(sketch, "E794", {"points": [v(32.06, -61.62) * mm, v(31.1, -61.85) * mm, v(29.98, -61.96) * mm, v(28.7, -61.96) * mm]});
            skFitSpline(sketch, "E795", {"points": [v(28.7, -61.96) * mm, v(26.46, -61.96) * mm, v(24.7, -61.47) * mm, v(23.4, -60.5) * mm]});
            skFitSpline(sketch, "E796", {"points": [v(23.4, -60.5) * mm, v(22.1, -59.52) * mm, v(21.44, -58.24) * mm, v(21.44, -56.68) * mm]});
            skFitSpline(sketch, "E797", {"points": [v(21.44, -56.68) * mm, v(21.44, -55.58) * mm, v(21.72, -54.7) * mm, v(22.3, -54) * mm]});
            skSolve(sketch);
        }
        {
            var Q0;
            Q0=qSketchRegion(id+"F0",true);
            extrude(context, id + "F2", {"entities" : qUnion([Q0]), "depth" : 0.8 * mm, "offsetDistance" : 25 * mm, "symmetric" : true});
        }
        {
            var Q0;
            Q0=qSketchRegion(id+"F1",true);
            var Q1;
            Q1=makeQuery(id+"F2.opExtrude","CAP_FACE",FACE,{"disambiguationData":[OSD([sQuery(id+"F0.wireOp",EDGE,"E0.bottom"),sQuery(id+"F0.wireOp",EDGE,"E0.top"),sQuery(id+"F0.wireOp",EDGE,"E0.left"),sQuery(id+"F0.wireOp",EDGE,"E0.right"),sQuery(id+"F0.wireOp",EDGE,"E1"),sQuery(id+"F0.wireOp",EDGE,"E2.filletArc"),sQuery(id+"F0.wireOp",EDGE,"E3.filletArc"),sQuery(id+"F0.wireOp",EDGE,"E4.filletArc"),sQuery(id+"F0.wireOp",EDGE,"E5.filletArc")])],"isStart":true});
            extrude(context, id + "F3", {"entities" : qUnion([Q0]), "operationType" : NewBodyOperationType.REMOVE, "endBound" : BoundingType.UP_TO_SURFACE, "oppositeDirection" : true, "depth" : 25 * mm, "endBoundEntityFace" : qUnion([Q1]), "offsetDistance" : 25 * mm});
        }
        {
            var Q0;
            Q0=qSketchRegion(id+"F1",true);
            var Q1;
            {var subQ27=sQuery(id+"F0.wireOp",EDGE,"E4.filletArc");var subQ29=sQuery(id+"F0.wireOp",EDGE,"E0.left");var subQ31=sQuery(id+"F0.wireOp",EDGE,"E0.top");var subQ32=sQuery(id+"F0.wireOp",EDGE,"E0.right");var subQ33=sQuery(id+"F0.wireOp",EDGE,"E1");var subQ34=sQuery(id+"F0.wireOp",EDGE,"E0.bottom");var subQ37=sQuery(id+"F0.wireOp",EDGE,"E2.filletArc");var subQ39=sQuery(id+"F0.wireOp",EDGE,"E5.filletArc");var subQ40=sQuery(id+"F0.wireOp",EDGE,"E3.filletArc");Q1=makeQuery(id+"F3.boolean.opBoolean","SPLIT",FACE,{"disambiguationData":[TD([makeQuery(id+"F2.opExtrude","SWEPT_FACE",FACE,{"disambiguationData":[OSD([subQ34])]})])],"derivedFrom":makeQuery(id+"F2.opExtrude","CAP_FACE",FACE,{"disambiguationData":[OSD([subQ34,subQ31,subQ29,subQ32,subQ33,subQ37,subQ40,subQ27,subQ39])],"isStart":true})});}
            extrude(context, id + "F4", {"entities" : qUnion([Q0]), "endBound" : BoundingType.UP_TO_SURFACE, "oppositeDirection" : true, "depth" : 25 * mm, "endBoundEntityFace" : qUnion([Q1]), "offsetDistance" : 25 * mm});
        }
        {
            var Q0;
            Q0=makeQuery(id+"F2.opExtrude","CAP_FACE",FACE,{"disambiguationData":[OSD([sQuery(id+"F0.wireOp",EDGE,"E0.bottom"),sQuery(id+"F0.wireOp",EDGE,"E0.top"),sQuery(id+"F0.wireOp",EDGE,"E0.left"),sQuery(id+"F0.wireOp",EDGE,"E0.right"),sQuery(id+"F0.wireOp",EDGE,"E1"),sQuery(id+"F0.wireOp",EDGE,"E2.filletArc"),sQuery(id+"F0.wireOp",EDGE,"E3.filletArc"),sQuery(id+"F0.wireOp",EDGE,"E4.filletArc"),sQuery(id+"F0.wireOp",EDGE,"E5.filletArc"),sQuery(id+"F0.wireOp",EDGE,"E6"),sQuery(id+"F0.wireOp",EDGE,"E7.filletArc"),sQuery(id+"F0.wireOp",EDGE,"E8"),sQuery(id+"F0.wireOp",EDGE,"E9.filletArc")])],"isStart":false});
            var sketch = newSketch(context, id + "F5", { "sketchPlane" : qUnion([Q0])});
            skLineSegment(sketch, "E798", {"start": v(11.46, 54.85) * mm, "end": v(11.45, 54.81) * mm});
            skLineSegment(sketch, "E799", {"start": v(27.64, 53.63) * mm, "end": v(27.59, 53.58) * mm});
            skLineSegment(sketch, "E800", {"start": v(27.59, 53.58) * mm, "end": v(27.56, 53.5) * mm});
            skLineSegment(sketch, "E801", {"start": v(-32.37, 38.36) * mm, "end": v(-32.33, 38.38) * mm});
            skLineSegment(sketch, "E802", {"start": v(-19.8, 54.8) * mm, "end": v(-19.82, 54.85) * mm});
            skLineSegment(sketch, "E803", {"start": v(-10.99, 16.65) * mm, "end": v(-11.02, 16.61) * mm});
            skLineSegment(sketch, "E804", {"start": v(-20.74, 26.75) * mm, "end": v(-20.77, 26.72) * mm});
            skLineSegment(sketch, "E805", {"start": v(-37.13, -52.42) * mm, "end": v(-37.13, -52.55) * mm});
            skLineSegment(sketch, "E806", {"start": v(-41.4, -55.03) * mm, "end": v(-40.67, -58.98) * mm});
            skLineSegment(sketch, "E807", {"start": v(-33.47, -53.21) * mm, "end": v(-33.47, -52.96) * mm});
            skLineSegment(sketch, "E808", {"start": v(-31.8, -45.27) * mm, "end": v(-33.2, -41.97) * mm});
            skLineSegment(sketch, "E809", {"start": v(-27.2, -47.5) * mm, "end": v(-27.94, -47.52) * mm});
            skLineSegment(sketch, "E810", {"start": v(-26.97, -45.28) * mm, "end": v(-27.57, -44.97) * mm});
            skLineSegment(sketch, "E811", {"start": v(-26.15, -44.7) * mm, "end": v(-25.93, -44.7) * mm});
            skLineSegment(sketch, "E812", {"start": v(-30.79, -42.6) * mm, "end": v(-30.16, -45.5) * mm});
            skLineSegment(sketch, "E813", {"start": v(-30.08, -54.51) * mm, "end": v(-29.98, -54.5) * mm});
            skLineSegment(sketch, "E814", {"start": v(-28.92, -50.53) * mm, "end": v(-28.64, -49.65) * mm});
            skLineSegment(sketch, "E815", {"start": v(-12, -42.47) * mm, "end": v(-12.35, -42.5) * mm});
            skLineSegment(sketch, "E816", {"start": v(-15.18, -48.1) * mm, "end": v(-15.49, -47.51) * mm});
            skLineSegment(sketch, "E817", {"start": v(-15.49, -47.51) * mm, "end": v(-18.42, -47.89) * mm});
            skLineSegment(sketch, "E818", {"start": v(-17.98, -42.47) * mm, "end": v(-18.3, -42.5) * mm});
            skLineSegment(sketch, "E819", {"start": v(-23.6, -55.3) * mm, "end": v(-20.4, -54.52) * mm});
            skLineSegment(sketch, "E820", {"start": v(-19.48, -51.11) * mm, "end": v(-19.27, -50.4) * mm});
            skLineSegment(sketch, "E821", {"start": v(-19.27, -50.4) * mm, "end": v(-15.97, -50.01) * mm});
            skLineSegment(sketch, "E822", {"start": v(-17.66, -55.01) * mm, "end": v(-14.44, -54.23) * mm});
            skLineSegment(sketch, "E823", {"start": v(-12.28, -52.94) * mm, "end": v(-13.13, -53.02) * mm});
            skLineSegment(sketch, "E824", {"start": v(-13.13, -53.02) * mm, "end": v(-13.87, -55.57) * mm});
            skLineSegment(sketch, "E825", {"start": v(-6.86, -55.02) * mm, "end": v(-6.07, -52.55) * mm});
            skLineSegment(sketch, "E826", {"start": v(-6.07, -52.55) * mm, "end": v(-7.39, -52.6) * mm});
            skLineSegment(sketch, "E827", {"start": v(-5.77, -45.17) * mm, "end": v(-6.5, -44.77) * mm});
            skLineSegment(sketch, "E828", {"start": v(-3.93, -44.74) * mm, "end": v(-3.14, -42.27) * mm});
            skLineSegment(sketch, "E829", {"start": v(-10.2, -42.74) * mm, "end": v(-10.93, -45.28) * mm});
            skLineSegment(sketch, "E830", {"start": v(-11.02, -51.9) * mm, "end": v(-11.32, -52.87) * mm});
            skLineSegment(sketch, "E831", {"start": v(-6.45, -55.27) * mm, "end": v(-3.24, -54.47) * mm});
            skLineSegment(sketch, "E832", {"start": v(-2.32, -51.06) * mm, "end": v(-1.2, -48.4) * mm});
            skLineSegment(sketch, "E833", {"start": v(-0.5, -54.96) * mm, "end": v(2.72, -54.17) * mm});
            skLineSegment(sketch, "E834", {"start": v(5.16, -42.42) * mm, "end": v(4.8, -42.45) * mm});
            skLineSegment(sketch, "E835", {"start": v(2.39, -47.13) * mm, "end": v(2.05, -47.96) * mm});
            skLineSegment(sketch, "E836", {"start": v(0.34, -41.86) * mm, "end": v(-2.77, -42.56) * mm});
            skLineSegment(sketch, "E837", {"start": v(13.51, -46.54) * mm, "end": v(16.71, -44.9) * mm});
            skLineSegment(sketch, "E838", {"start": v(14.17, -53.27) * mm, "end": v(12.25, -51.69) * mm});
            skLineSegment(sketch, "E839", {"start": v(17.83, -42.74) * mm, "end": v(17.08, -45.28) * mm});
            skLineSegment(sketch, "E840", {"start": v(19.98, -54.55) * mm, "end": v(20.07, -54.51) * mm});
            skLineSegment(sketch, "E841", {"start": v(23.12, -45.17) * mm, "end": v(22.38, -44.77) * mm});
            skLineSegment(sketch, "E842", {"start": v(24.96, -44.74) * mm, "end": v(25.98, -44.74) * mm});
            skLineSegment(sketch, "E843", {"start": v(25.98, -44.74) * mm, "end": v(26.76, -42.27) * mm});
            skLineSegment(sketch, "E844", {"start": v(26.25, -42.74) * mm, "end": v(25.5, -45.28) * mm});
            skLineSegment(sketch, "E845", {"start": v(23.44, -55.28) * mm, "end": v(23.44, -55.3) * mm});
            skLineSegment(sketch, "E846", {"start": v(28.93, -54.71) * mm, "end": v(30.75, -54.71) * mm});
            skLineSegment(sketch, "E847", {"start": v(30.75, -54.71) * mm, "end": v(31.56, -52.27) * mm});
            skLineSegment(sketch, "E848", {"start": v(28, -49.56) * mm, "end": v(31.6, -49.43) * mm});
            skLineSegment(sketch, "E849", {"start": v(31.6, -49.43) * mm, "end": v(32.38, -47.22) * mm});
            skLineSegment(sketch, "E850", {"start": v(32.38, -47.22) * mm, "end": v(28.73, -47.36) * mm});
            skLineSegment(sketch, "E851", {"start": v(29.66, -45.17) * mm, "end": v(29.13, -44.87) * mm});
            skLineSegment(sketch, "E852", {"start": v(33.42, -44.74) * mm, "end": v(34.4, -44.74) * mm});
            skLineSegment(sketch, "E853", {"start": v(34.4, -44.74) * mm, "end": v(35.18, -42.27) * mm});
            skLineSegment(sketch, "E854", {"start": v(33.6, -42.6) * mm, "end": v(34.22, -45.5) * mm});
            skLineSegment(sketch, "E855", {"start": v(34.3, -54.51) * mm, "end": v(34.4, -54.5) * mm});
            skLineSegment(sketch, "E856", {"start": v(35.46, -50.53) * mm, "end": v(35.75, -49.65) * mm});
            skLineSegment(sketch, "E857", {"start": v(35.75, -49.65) * mm, "end": v(36.18, -50.01) * mm});
            skLineSegment(sketch, "E858", {"start": v(39.55, -55.03) * mm, "end": v(42.47, -53.97) * mm});
            skLineSegment(sketch, "E859", {"start": v(37.18, -47.5) * mm, "end": v(36.45, -47.52) * mm});
            skLineSegment(sketch, "E860", {"start": v(37.42, -45.28) * mm, "end": v(36.82, -44.97) * mm});
            skLineSegment(sketch, "E861", {"start": v(38.24, -44.7) * mm, "end": v(38.46, -44.7) * mm});
            skLineSegment(sketch, "E862", {"start": v(-2.2, -6.19) * mm, "end": v(-2.11, -6.19) * mm});
            skFitSpline(sketch, "E863", {"points": [v(11.45, 54.81) * mm, v(11.51, 54.8) * mm, v(11.57, 54.77) * mm, v(11.63, 54.76) * mm]});
            skFitSpline(sketch, "E864", {"points": [v(11.63, 54.76) * mm, v(13.5, 54.3) * mm, v(15.32, 53.75) * mm, v(17.13, 53.1) * mm]});
            skFitSpline(sketch, "E865", {"points": [v(17.13, 53.1) * mm, v(18.61, 52.56) * mm, v(20.09, 52) * mm, v(21.5, 51.3) * mm]});
            skFitSpline(sketch, "E866", {"points": [v(21.5, 51.3) * mm, v(21.79, 51.15) * mm, v(22.09, 51.02) * mm, v(22.38, 50.9) * mm]});
            skFitSpline(sketch, "E867", {"points": [v(22.38, 50.9) * mm, v(22.58, 50.81) * mm, v(22.78, 50.73) * mm, v(22.98, 50.67) * mm]});
            skFitSpline(sketch, "E868", {"points": [v(22.98, 50.67) * mm, v(23.31, 50.58) * mm, v(23.6, 50.72) * mm, v(23.74, 51.03) * mm]});
            skFitSpline(sketch, "E869", {"points": [v(23.74, 51.03) * mm, v(23.77, 51.11) * mm, v(23.8, 51.2) * mm, v(23.82, 51.28) * mm]});
            skFitSpline(sketch, "E870", {"points": [v(23.82, 51.28) * mm, v(23.88, 51.81) * mm, v(23.9, 52.34) * mm, v(23.78, 52.86) * mm]});
            skFitSpline(sketch, "E871", {"points": [v(23.78, 52.86) * mm, v(23.64, 53.52) * mm, v(23.33, 54.1) * mm, v(22.97, 54.66) * mm]});
            skFitSpline(sketch, "E872", {"points": [v(22.97, 54.66) * mm, v(22.89, 54.8) * mm, v(22.8, 54.86) * mm, v(22.62, 54.86) * mm]});
            skFitSpline(sketch, "E873", {"points": [v(22.62, 54.86) * mm, v(18.97, 54.85) * mm, v(15.32, 54.85) * mm, v(11.67, 54.85) * mm]});
            skFitSpline(sketch, "E874", {"points": [v(11.67, 54.85) * mm, v(11.6, 54.85) * mm, v(11.53, 54.85) * mm, v(11.46, 54.85) * mm]});
            skFitSpline(sketch, "E875", {"points": [v(27.56, 53.5) * mm, v(27.47, 53.19) * mm, v(27.46, 52.87) * mm, v(27.49, 52.56) * mm]});
            skFitSpline(sketch, "E876", {"points": [v(27.49, 52.56) * mm, v(27.55, 51.66) * mm, v(27.77, 50.8) * mm, v(28.06, 49.96) * mm]});
            skFitSpline(sketch, "E877", {"points": [v(28.06, 49.96) * mm, v(28.47, 48.79) * mm, v(29, 47.67) * mm, v(29.6, 46.58) * mm]});
            skFitSpline(sketch, "E878", {"points": [v(29.6, 46.58) * mm, v(30.15, 45.56) * mm, v(30.75, 44.56) * mm, v(31.39, 43.6) * mm]});
            skFitSpline(sketch, "E879", {"points": [v(31.39, 43.6) * mm, v(32.2, 42.37) * mm, v(33.22, 41.34) * mm, v(34.3, 40.36) * mm]});
            skFitSpline(sketch, "E880", {"points": [v(34.3, 40.36) * mm, v(34.32, 40.35) * mm, v(34.35, 40.34) * mm, v(34.39, 40.32) * mm]});
            skFitSpline(sketch, "E881", {"points": [v(34.39, 40.32) * mm, v(35.45, 41.4) * mm, v(36.52, 42.49) * mm, v(37.6, 43.58) * mm]});
            skFitSpline(sketch, "E882", {"points": [v(37.6, 43.58) * mm, v(34.26, 46.94) * mm, v(30.95, 50.28) * mm, v(27.64, 53.63) * mm]});
            skFitSpline(sketch, "E883", {"points": [v(-32.33, 38.38) * mm, v(-32.33, 38.47) * mm, v(-32.34, 38.57) * mm, v(-32.34, 38.67) * mm]});
            skFitSpline(sketch, "E884", {"points": [v(-32.34, 38.67) * mm, v(-32.37, 39.22) * mm, v(-32.4, 39.77) * mm, v(-32.4, 40.32) * mm]});
            skFitSpline(sketch, "E885", {"points": [v(-32.4, 40.32) * mm, v(-32.42, 41.82) * mm, v(-32.11, 43.26) * mm, v(-31.52, 44.63) * mm]});
            skFitSpline(sketch, "E886", {"points": [v(-31.52, 44.63) * mm, v(-30.88, 46.1) * mm, v(-29.98, 47.39) * mm, v(-28.9, 48.56) * mm]});
            skFitSpline(sketch, "E887", {"points": [v(-28.9, 48.56) * mm, v(-27.16, 50.45) * mm, v(-25.1, 51.95) * mm, v(-22.9, 53.25) * mm]});
            skFitSpline(sketch, "E888", {"points": [v(-22.9, 53.25) * mm, v(-21.96, 53.8) * mm, v(-20.99, 54.26) * mm, v(-20, 54.7) * mm]});
            skFitSpline(sketch, "E889", {"points": [v(-20, 54.7) * mm, v(-19.94, 54.74) * mm, v(-19.87, 54.78) * mm, v(-19.8, 54.8) * mm]});
            skFitSpline(sketch, "E890", {"points": [v(-19.82, 54.85) * mm, v(-19.9, 54.85) * mm, v(-19.97, 54.85) * mm, v(-20.04, 54.85) * mm]});
            skFitSpline(sketch, "E891", {"points": [v(-20.04, 54.85) * mm, v(-22.05, 54.85) * mm, v(-24.07, 54.85) * mm, v(-26.08, 54.86) * mm]});
            skFitSpline(sketch, "E892", {"points": [v(-26.08, 54.86) * mm, v(-26.27, 54.86) * mm, v(-26.4, 54.8) * mm, v(-26.52, 54.67) * mm]});
            skFitSpline(sketch, "E893", {"points": [v(-26.52, 54.67) * mm, v(-27.27, 53.92) * mm, v(-28.04, 53.17) * mm, v(-28.78, 52.41) * mm]});
            skFitSpline(sketch, "E894", {"points": [v(-28.78, 52.41) * mm, v(-31.65, 49.52) * mm, v(-34.5, 46.62) * mm, v(-37.37, 43.73) * mm]});
            skFitSpline(sketch, "E895", {"points": [v(-37.37, 43.73) * mm, v(-37.41, 43.68) * mm, v(-37.46, 43.63) * mm, v(-37.51, 43.57) * mm]});
            skFitSpline(sketch, "E896", {"points": [v(-37.51, 43.57) * mm, v(-35.84, 41.78) * mm, v(-34.1, 40.08) * mm, v(-32.37, 38.36) * mm]});
            skFitSpline(sketch, "E897", {"points": [v(-11.02, 16.61) * mm, v(-7.33, 12.94) * mm, v(-3.65, 9.25) * mm, v(0.07, 5.62) * mm]});
            skFitSpline(sketch, "E898", {"points": [v(0.07, 5.62) * mm, v(0.28, 5.77) * mm, v(9.4, 15.06) * mm, v(9.46, 15.2) * mm]});
            skFitSpline(sketch, "E899", {"points": [v(9.46, 15.2) * mm, v(9.4, 15.19) * mm, v(9.35, 15.19) * mm, v(9.3, 15.18) * mm]});
            skFitSpline(sketch, "E900", {"points": [v(9.3, 15.18) * mm, v(7.87, 14.92) * mm, v(6.43, 14.7) * mm, v(4.99, 14.54) * mm]});
            skFitSpline(sketch, "E901", {"points": [v(4.99, 14.54) * mm, v(3.7, 14.4) * mm, v(2.41, 14.3) * mm, v(1.12, 14.25) * mm]});
            skFitSpline(sketch, "E902", {"points": [v(1.12, 14.25) * mm, v(-0.66, 14.17) * mm, v(-2.42, 14.34) * mm, v(-4.16, 14.69) * mm]});
            skFitSpline(sketch, "E903", {"points": [v(-4.16, 14.69) * mm, v(-6.06, 15.07) * mm, v(-7.92, 15.62) * mm, v(-9.76, 16.23) * mm]});
            skFitSpline(sketch, "E904", {"points": [v(-9.76, 16.23) * mm, v(-10.17, 16.37) * mm, v(-10.58, 16.51) * mm, v(-10.99, 16.65) * mm]});
            skFitSpline(sketch, "E905", {"points": [v(-20.77, 26.72) * mm, v(-20.72, 26.67) * mm, v(-20.68, 26.61) * mm, v(-20.62, 26.56) * mm]});
            skFitSpline(sketch, "E906", {"points": [v(-20.62, 26.56) * mm, v(-20.43, 26.36) * mm, v(-20.23, 26.16) * mm, v(-20.04, 25.96) * mm]});
            skFitSpline(sketch, "E907", {"points": [v(-20.04, 25.96) * mm, v(-18.76, 24.7) * mm, v(-17.48, 23.44) * mm, v(-16.2, 22.18) * mm]});
            skFitSpline(sketch, "E908", {"points": [v(-16.2, 22.18) * mm, v(-15.86, 21.84) * mm, v(-15.47, 21.55) * mm, v(-15.03, 21.34) * mm]});
            skFitSpline(sketch, "E909", {"points": [v(-15.03, 21.34) * mm, v(-14.6, 21.15) * mm, v(-14.18, 20.97) * mm, v(-13.75, 20.81) * mm]});
            skFitSpline(sketch, "E910", {"points": [v(-13.75, 20.81) * mm, v(-10.92, 19.76) * mm, v(-8.06, 18.85) * mm, v(-5.1, 18.26) * mm]});
            skFitSpline(sketch, "E911", {"points": [v(-5.1, 18.26) * mm, v(-3.53, 17.95) * mm, v(-1.96, 17.73) * mm, v(-0.37, 17.72) * mm]});
            skFitSpline(sketch, "E912", {"points": [v(-0.37, 17.72) * mm, v(0.67, 17.72) * mm, v(1.72, 17.75) * mm, v(2.76, 17.8) * mm]});
            skFitSpline(sketch, "E913", {"points": [v(2.76, 17.8) * mm, v(4.2, 17.84) * mm, v(5.63, 17.98) * mm, v(7.05, 18.24) * mm]});
            skFitSpline(sketch, "E914", {"points": [v(7.05, 18.24) * mm, v(7.97, 18.4) * mm, v(8.88, 18.63) * mm, v(9.74, 18.99) * mm]});
            skFitSpline(sketch, "E915", {"points": [v(9.74, 18.99) * mm, v(10.3, 19.22) * mm, v(10.82, 19.5) * mm, v(11.27, 19.9) * mm]});
            skFitSpline(sketch, "E916", {"points": [v(11.27, 19.9) * mm, v(12.1, 20.62) * mm, v(12.06, 21.74) * mm, v(11.18, 22.4) * mm]});
            skFitSpline(sketch, "E917", {"points": [v(11.18, 22.4) * mm, v(11.05, 22.5) * mm, v(10.92, 22.59) * mm, v(10.78, 22.66) * mm]});
            skFitSpline(sketch, "E918", {"points": [v(10.78, 22.66) * mm, v(10.58, 22.77) * mm, v(10.37, 22.87) * mm, v(10.16, 22.96) * mm]});
            skFitSpline(sketch, "E919", {"points": [v(10.16, 22.96) * mm, v(9.31, 23.32) * mm, v(8.42, 23.53) * mm, v(7.52, 23.7) * mm]});
            skFitSpline(sketch, "E920", {"points": [v(7.52, 23.7) * mm, v(5.81, 24.04) * mm, v(4.1, 24.23) * mm, v(2.36, 24.36) * mm]});
            skFitSpline(sketch, "E921", {"points": [v(2.36, 24.36) * mm, v(1.06, 24.45) * mm, v(-0.25, 24.52) * mm, v(-1.56, 24.58) * mm]});
            skFitSpline(sketch, "E922", {"points": [v(-1.56, 24.58) * mm, v(-3.47, 24.67) * mm, v(-5.38, 24.75) * mm, v(-7.28, 24.85) * mm]});
            skFitSpline(sketch, "E923", {"points": [v(-7.28, 24.85) * mm, v(-8.91, 24.93) * mm, v(-10.54, 25.03) * mm, v(-12.17, 25.13) * mm]});
            skFitSpline(sketch, "E924", {"points": [v(-12.17, 25.13) * mm, v(-12.54, 25.15) * mm, v(-12.9, 25.17) * mm, v(-13.27, 25.22) * mm]});
            skFitSpline(sketch, "E925", {"points": [v(-13.27, 25.22) * mm, v(-14.29, 25.37) * mm, v(-15.3, 25.53) * mm, v(-16.32, 25.7) * mm]});
            skFitSpline(sketch, "E926", {"points": [v(-16.32, 25.7) * mm, v(-17.5, 25.9) * mm, v(-18.67, 26.13) * mm, v(-19.82, 26.47) * mm]});
            skFitSpline(sketch, "E927", {"points": [v(-19.82, 26.47) * mm, v(-20.13, 26.56) * mm, v(-20.44, 26.66) * mm, v(-20.74, 26.75) * mm]});
            skFitSpline(sketch, "E928", {"points": [v(32.73, 38.61) * mm, v(32.66, 38.67) * mm, v(32.6, 38.7) * mm, v(32.56, 38.74) * mm]});
            skFitSpline(sketch, "E929", {"points": [v(32.56, 38.74) * mm, v(30.26, 40.8) * mm, v(27.84, 42.7) * mm, v(25.29, 44.46) * mm]});
            skFitSpline(sketch, "E930", {"points": [v(25.29, 44.46) * mm, v(22.25, 46.54) * mm, v(19.02, 48.22) * mm, v(15.57, 49.49) * mm]});
            skFitSpline(sketch, "E931", {"points": [v(15.57, 49.49) * mm, v(13.96, 50.08) * mm, v(12.33, 50.54) * mm, v(10.64, 50.83) * mm]});
            skFitSpline(sketch, "E932", {"points": [v(10.64, 50.83) * mm, v(8.98, 51.11) * mm, v(7.3, 51.39) * mm, v(5.64, 51.65) * mm]});
            skFitSpline(sketch, "E933", {"points": [v(5.64, 51.65) * mm, v(4.61, 51.8) * mm, v(3.58, 51.94) * mm, v(2.54, 52.06) * mm]});
            skFitSpline(sketch, "E934", {"points": [v(2.54, 52.06) * mm, v(1.61, 52.17) * mm, v(0.69, 52.27) * mm, v(-0.24, 52.35) * mm]});
            skFitSpline(sketch, "E935", {"points": [v(-0.24, 52.35) * mm, v(-1.21, 52.43) * mm, v(-2.18, 52.5) * mm, v(-3.15, 52.54) * mm]});
            skFitSpline(sketch, "E936", {"points": [v(-3.15, 52.54) * mm, v(-4.23, 52.58) * mm, v(-5.3, 52.59) * mm, v(-6.39, 52.6) * mm]});
            skFitSpline(sketch, "E937", {"points": [v(-6.39, 52.6) * mm, v(-7.8, 52.61) * mm, v(-9.2, 52.54) * mm, v(-10.59, 52.34) * mm]});
            skFitSpline(sketch, "E938", {"points": [v(-10.59, 52.34) * mm, v(-11.55, 52.2) * mm, v(-12.5, 52) * mm, v(-13.4, 51.66) * mm]});
            skFitSpline(sketch, "E939", {"points": [v(-13.4, 51.66) * mm, v(-14.27, 51.35) * mm, v(-15.08, 50.94) * mm, v(-15.78, 50.33) * mm]});
            skFitSpline(sketch, "E940", {"points": [v(-15.78, 50.33) * mm, v(-16.1, 50.06) * mm, v(-16.33, 49.72) * mm, v(-16.47, 49.33) * mm]});
            skFitSpline(sketch, "E941", {"points": [v(-16.47, 49.33) * mm, v(-16.61, 48.96) * mm, v(-16.58, 48.6) * mm, v(-16.35, 48.28) * mm]});
            skFitSpline(sketch, "E942", {"points": [v(-16.35, 48.28) * mm, v(-16.26, 48.13) * mm, v(-16.14, 47.99) * mm, v(-16, 47.88) * mm]});
            skFitSpline(sketch, "E943", {"points": [v(-16, 47.88) * mm, v(-15.7, 47.65) * mm, v(-15.4, 47.4) * mm, v(-15.08, 47.22) * mm]});
            skFitSpline(sketch, "E944", {"points": [v(-15.08, 47.22) * mm, v(-13.88, 46.53) * mm, v(-12.6, 46.04) * mm, v(-11.25, 45.72) * mm]});
            skFitSpline(sketch, "E945", {"points": [v(-11.25, 45.72) * mm, v(-10.07, 45.43) * mm, v(-8.88, 45.26) * mm, v(-7.67, 45.13) * mm]});
            skFitSpline(sketch, "E946", {"points": [v(-7.67, 45.13) * mm, v(-6.53, 45) * mm, v(-5.38, 44.96) * mm, v(-4.24, 44.92) * mm]});
            skFitSpline(sketch, "E947", {"points": [v(-4.24, 44.92) * mm, v(-3.57, 44.9) * mm, v(-2.9, 44.9) * mm, v(-2.23, 44.86) * mm]});
            skFitSpline(sketch, "E948", {"points": [v(-2.23, 44.86) * mm, v(-1.32, 44.81) * mm, v(-0.4, 44.73) * mm, v(0.51, 44.66) * mm]});
            skFitSpline(sketch, "E949", {"points": [v(0.51, 44.66) * mm, v(1.53, 44.57) * mm, v(2.55, 44.48) * mm, v(3.56, 44.37) * mm]});
            skFitSpline(sketch, "E950", {"points": [v(3.56, 44.37) * mm, v(4.67, 44.26) * mm, v(5.78, 44.13) * mm, v(6.9, 44) * mm]});
            skFitSpline(sketch, "E951", {"points": [v(6.9, 44) * mm, v(7.92, 43.87) * mm, v(8.95, 43.74) * mm, v(9.97, 43.58) * mm]});
            skFitSpline(sketch, "E952", {"points": [v(9.97, 43.58) * mm, v(11.17, 43.38) * mm, v(12.37, 43.16) * mm, v(13.57, 42.93) * mm]});
            skFitSpline(sketch, "E953", {"points": [v(13.57, 42.93) * mm, v(15.18, 42.62) * mm, v(16.77, 42.26) * mm, v(18.34, 41.78) * mm]});
            skFitSpline(sketch, "E954", {"points": [v(18.34, 41.78) * mm, v(19.06, 41.57) * mm, v(19.78, 41.35) * mm, v(20.46, 41.03) * mm]});
            skFitSpline(sketch, "E955", {"points": [v(20.46, 41.03) * mm, v(21.7, 40.43) * mm, v(22.84, 39.69) * mm, v(23.9, 38.81) * mm]});
            skFitSpline(sketch, "E956", {"points": [v(23.9, 38.81) * mm, v(25.48, 37.5) * mm, v(26.78, 35.95) * mm, v(27.86, 34.2) * mm]});
            skFitSpline(sketch, "E957", {"points": [v(27.86, 34.2) * mm, v(27.91, 34.12) * mm, v(27.97, 34.03) * mm, v(28.04, 33.92) * mm]});
            skFitSpline(sketch, "E958", {"points": [v(28.04, 33.92) * mm, v(29.66, 35.43) * mm, v(31.16, 37.01) * mm, v(32.73, 38.61) * mm]});
            skFitSpline(sketch, "E959", {"points": [v(0.03, 0.2) * mm, v(-0.4, 0.54) * mm, v(-42.5, 43.09) * mm, v(-42.87, 43.56) * mm]});
            skFitSpline(sketch, "E960", {"points": [v(-42.87, 43.56) * mm, v(-42.82, 43.62) * mm, v(-42.77, 43.7) * mm, v(-42.7, 43.75) * mm]});
            skFitSpline(sketch, "E961", {"points": [v(-42.7, 43.75) * mm, v(-41.16, 45.37) * mm, v(-39.63, 47) * mm, v(-38.07, 48.62) * mm]});
            skFitSpline(sketch, "E962", {"points": [v(-38.07, 48.62) * mm, v(-34.77, 52.02) * mm, v(-31.45, 55.41) * mm, v(-28.15, 58.8) * mm]});
            skFitSpline(sketch, "E963", {"points": [v(-28.15, 58.8) * mm, v(-28.03, 58.93) * mm, v(-27.92, 58.98) * mm, v(-27.75, 58.98) * mm]});
            skFitSpline(sketch, "E964", {"points": [v(-27.75, 58.98) * mm, v(-9.25, 58.98) * mm, v(9.26, 58.98) * mm, v(27.76, 58.98) * mm]});
            skFitSpline(sketch, "E965", {"points": [v(27.76, 58.98) * mm, v(27.92, 58.98) * mm, v(28.03, 58.94) * mm, v(28.14, 58.82) * mm]});
            skFitSpline(sketch, "E966", {"points": [v(28.14, 58.82) * mm, v(32.5, 54.32) * mm, v(36.87, 49.82) * mm, v(41.24, 45.32) * mm]});
            skFitSpline(sketch, "E967", {"points": [v(41.24, 45.32) * mm, v(41.74, 44.8) * mm, v(42.23, 44.27) * mm, v(42.72, 43.75) * mm]});
            skFitSpline(sketch, "E968", {"points": [v(42.72, 43.75) * mm, v(42.77, 43.7) * mm, v(42.82, 43.63) * mm, v(42.87, 43.58) * mm]});
            skFitSpline(sketch, "E969", {"points": [v(42.87, 43.58) * mm, v(42.86, 43.54) * mm, v(42.85, 43.52) * mm, v(42.84, 43.5) * mm]});
            skFitSpline(sketch, "E970", {"points": [v(42.84, 43.5) * mm, v(28.65, 29) * mm, v(14.28, 14.66) * mm, v(0.03, 0.2) * mm]});
            skFitSpline(sketch, "E971", {"points": [v(-33.2, -41.97) * mm, v(-35.1, -42.44) * mm, v(-36.52, -42.95) * mm, v(-37.47, -43.5) * mm]});
            skFitSpline(sketch, "E972", {"points": [v(-37.47, -43.5) * mm, v(-38.7, -44.22) * mm, v(-39.31, -45.4) * mm, v(-39.31, -47.05) * mm]});
            skFitSpline(sketch, "E973", {"points": [v(-39.31, -47.05) * mm, v(-39.31, -47.82) * mm, v(-38.98, -48.73) * mm, v(-38.32, -49.77) * mm]});
            skFitSpline(sketch, "E974", {"points": [v(-38.32, -49.77) * mm, v(-37.94, -50.36) * mm, v(-37.68, -50.77) * mm, v(-37.53, -50.99) * mm]});
            skFitSpline(sketch, "E975", {"points": [v(-37.53, -50.99) * mm, v(-37.26, -51.52) * mm, v(-37.13, -52) * mm, v(-37.13, -52.42) * mm]});
            skFitSpline(sketch, "E976", {"points": [v(-37.13, -52.55) * mm, v(-37.13, -53.4) * mm, v(-37.86, -54.07) * mm, v(-39.32, -54.57) * mm]});
            skFitSpline(sketch, "E977", {"points": [v(-39.32, -54.57) * mm, v(-39.94, -54.78) * mm, v(-40.64, -54.93) * mm, v(-41.4, -55.03) * mm]});
            skFitSpline(sketch, "E978", {"points": [v(-40.67, -58.98) * mm, v(-38.63, -58.47) * mm, v(-37.14, -57.9) * mm, v(-36.22, -57.29) * mm]});
            skFitSpline(sketch, "E979", {"points": [v(-36.22, -57.29) * mm, v(-34.53, -56.17) * mm, v(-33.61, -54.81) * mm, v(-33.47, -53.21) * mm]});
            skFitSpline(sketch, "E980", {"points": [v(-33.47, -52.96) * mm, v(-33.47, -52.3) * mm, v(-33.71, -51.4) * mm, v(-34.2, -50.26) * mm]});
            skFitSpline(sketch, "E981", {"points": [v(-34.2, -50.26) * mm, v(-34.3, -50.07) * mm, v(-34.6, -49.6) * mm, v(-35.14, -48.82) * mm]});
            skFitSpline(sketch, "E982", {"points": [v(-35.14, -48.82) * mm, v(-35.54, -48.24) * mm, v(-35.74, -47.75) * mm, v(-35.74, -47.37) * mm]});
            skFitSpline(sketch, "E983", {"points": [v(-35.74, -47.37) * mm, v(-35.74, -47.14) * mm, v(-35.67, -46.92) * mm, v(-35.52, -46.71) * mm]});
            skFitSpline(sketch, "E984", {"points": [v(-35.52, -46.71) * mm, v(-35.08, -46.1) * mm, v(-34.34, -45.68) * mm, v(-33.3, -45.44) * mm]});
            skFitSpline(sketch, "E985", {"points": [v(-33.3, -45.44) * mm, v(-32.88, -45.35) * mm, v(-32.38, -45.3) * mm, v(-31.8, -45.27) * mm]});
            skFitSpline(sketch, "E986", {"points": [v(-25.3, -47.18) * mm, v(-25.81, -47.37) * mm, v(-26.45, -47.48) * mm, v(-27.2, -47.5) * mm]});
            skFitSpline(sketch, "E987", {"points": [v(-27.94, -47.52) * mm, v(-27.73, -46.95) * mm, v(-27.61, -46.65) * mm, v(-27.6, -46.61) * mm]});
            skFitSpline(sketch, "E988", {"points": [v(-27.6, -46.61) * mm, v(-27.38, -46.09) * mm, v(-27.17, -45.64) * mm, v(-26.97, -45.28) * mm]});
            skFitSpline(sketch, "E989", {"points": [v(-27.57, -44.97) * mm, v(-26.98, -44.8) * mm, v(-26.5, -44.71) * mm, v(-26.15, -44.7) * mm]});
            skFitSpline(sketch, "E990", {"points": [v(-25.93, -44.7) * mm, v(-25.53, -44.7) * mm, v(-25.25, -44.73) * mm, v(-25.07, -44.8) * mm]});
            skFitSpline(sketch, "E991", {"points": [v(-25.07, -44.8) * mm, v(-24.47, -45.02) * mm, v(-24.17, -45.36) * mm, v(-24.17, -45.8) * mm]});
            skFitSpline(sketch, "E992", {"points": [v(-24.17, -45.8) * mm, v(-24.17, -46.42) * mm, v(-24.54, -46.88) * mm, v(-25.3, -47.18) * mm]});
            skFitSpline(sketch, "E993", {"points": [v(-24.9, -49.17) * mm, v(-22.97, -48.55) * mm, v(-21.86, -47.52) * mm, v(-21.59, -46.09) * mm]});
            skFitSpline(sketch, "E994", {"points": [v(-21.59, -46.09) * mm, v(-21.54, -45.82) * mm, v(-21.51, -45.6) * mm, v(-21.51, -45.44) * mm]});
            skFitSpline(sketch, "E995", {"points": [v(-21.51, -45.44) * mm, v(-21.51, -44.24) * mm, v(-22.1, -43.4) * mm, v(-23.3, -42.9) * mm]});
            skFitSpline(sketch, "E996", {"points": [v(-23.3, -42.9) * mm, v(-23.83, -42.67) * mm, v(-24.32, -42.51) * mm, v(-24.76, -42.44) * mm]});
            skFitSpline(sketch, "E997", {"points": [v(-24.76, -42.44) * mm, v(-24.88, -42.42) * mm, v(-25.36, -42.38) * mm, v(-26.2, -42.32) * mm]});
            skFitSpline(sketch, "E998", {"points": [v(-26.2, -42.32) * mm, v(-26.5, -42.29) * mm, v(-26.78, -42.27) * mm, v(-27.02, -42.27) * mm]});
            skFitSpline(sketch, "E999", {"points": [v(-27.02, -42.27) * mm, v(-28.08, -42.27) * mm, v(-29.33, -42.38) * mm, v(-30.79, -42.6) * mm]});
            skFitSpline(sketch, "E1000", {"points": [v(-30.16, -45.5) * mm, v(-29.99, -45.46) * mm, v(-29.78, -45.4) * mm, v(-29.55, -45.32) * mm]});
            skFitSpline(sketch, "E1001", {"points": [v(-29.55, -45.32) * mm, v(-29.82, -45.87) * mm, v(-30.04, -46.3) * mm, v(-30.18, -46.61) * mm]});
            skFitSpline(sketch, "E1002", {"points": [v(-30.18, -46.61) * mm, v(-30.91, -48.2) * mm, v(-31.44, -49.5) * mm, v(-31.78, -50.53) * mm]});
            skFitSpline(sketch, "E1003", {"points": [v(-31.78, -50.53) * mm, v(-32.33, -52.16) * mm, v(-32.8, -53.73) * mm, v(-33.2, -55.25) * mm]});
            skFitSpline(sketch, "E1004", {"points": [v(-33.2, -55.25) * mm, v(-32.02, -54.94) * mm, v(-30.98, -54.69) * mm, v(-30.08, -54.51) * mm]});
            skFitSpline(sketch, "E1005", {"points": [v(-29.98, -54.5) * mm, v(-29.47, -52.5) * mm, v(-29.12, -51.17) * mm, v(-28.92, -50.53) * mm]});
            skFitSpline(sketch, "E1006", {"points": [v(-28.64, -49.65) * mm, v(-27.18, -49.65) * mm, v(-25.94, -49.5) * mm, v(-24.9, -49.17) * mm]});
            skFitSpline(sketch, "E1007", {"points": [v(-12.35, -42.5) * mm, v(-13.55, -44.63) * mm, v(-14.49, -46.5) * mm, v(-15.18, -48.1) * mm]});
            skFitSpline(sketch, "E1008", {"points": [v(-18.42, -47.89) * mm, v(-18.26, -47.47) * mm, v(-18.17, -47.24) * mm, v(-18.15, -47.19) * mm]});
            skFitSpline(sketch, "E1009", {"points": [v(-18.15, -47.19) * mm, v(-17.14, -45) * mm, v(-16.35, -43.36) * mm, v(-15.75, -42.28) * mm]});
            skFitSpline(sketch, "E1010", {"points": [v(-15.75, -42.28) * mm, v(-16.6, -42.33) * mm, v(-17.33, -42.4) * mm, v(-17.98, -42.47) * mm]});
            skFitSpline(sketch, "E1011", {"points": [v(-18.3, -42.5) * mm, v(-19.4, -44.46) * mm, v(-20.21, -46.02) * mm, v(-20.75, -47.19) * mm]});
            skFitSpline(sketch, "E1012", {"points": [v(-20.75, -47.19) * mm, v(-21.45, -48.7) * mm, v(-21.98, -50.01) * mm, v(-22.35, -51.11) * mm]});
            skFitSpline(sketch, "E1013", {"points": [v(-22.35, -51.11) * mm, v(-22.82, -52.55) * mm, v(-23.24, -53.95) * mm, v(-23.6, -55.3) * mm]});
            skFitSpline(sketch, "E1014", {"points": [v(-20.4, -54.52) * mm, v(-19.96, -52.84) * mm, v(-19.66, -51.7) * mm, v(-19.48, -51.11) * mm]});
            skFitSpline(sketch, "E1015", {"points": [v(-15.97, -50.01) * mm, v(-16.2, -50.63) * mm, v(-16.33, -51) * mm, v(-16.38, -51.11) * mm]});
            skFitSpline(sketch, "E1016", {"points": [v(-16.38, -51.11) * mm, v(-16.84, -52.41) * mm, v(-17.26, -53.71) * mm, v(-17.66, -55.01) * mm]});
            skFitSpline(sketch, "E1017", {"points": [v(-14.44, -54.23) * mm, v(-13.99, -52.67) * mm, v(-13.68, -51.63) * mm, v(-13.52, -51.11) * mm]});
            skFitSpline(sketch, "E1018", {"points": [v(-13.52, -51.11) * mm, v(-12.93, -49.18) * mm, v(-12.5, -47.87) * mm, v(-12.2, -47.19) * mm]});
            skFitSpline(sketch, "E1019", {"points": [v(-12.2, -47.19) * mm, v(-11.35, -45.29) * mm, v(-10.56, -43.65) * mm, v(-9.8, -42.28) * mm]});
            skFitSpline(sketch, "E1020", {"points": [v(-9.8, -42.28) * mm, v(-10.63, -42.33) * mm, v(-11.37, -42.4) * mm, v(-12, -42.47) * mm]});
            skFitSpline(sketch, "E1021", {"points": [v(-13.87, -55.57) * mm, v(-11.57, -55.28) * mm, v(-10.1, -55.1) * mm, v(-9.44, -55.05) * mm]});
            skFitSpline(sketch, "E1022", {"points": [v(-9.44, -55.05) * mm, v(-9.04, -55.03) * mm, v(-8.18, -55.02) * mm, v(-6.86, -55.02) * mm]});
            skFitSpline(sketch, "E1023", {"points": [v(-7.39, -52.6) * mm, v(-7.83, -52.63) * mm, v(-8.15, -52.64) * mm, v(-8.33, -52.65) * mm]});
            skFitSpline(sketch, "E1024", {"points": [v(-8.33, -52.65) * mm, v(-8.15, -51.93) * mm, v(-7.95, -51.23) * mm, v(-7.75, -50.56) * mm]});
            skFitSpline(sketch, "E1025", {"points": [v(-7.75, -50.56) * mm, v(-7.18, -48.74) * mm, v(-6.73, -47.43) * mm, v(-6.4, -46.64) * mm]});
            skFitSpline(sketch, "E1026", {"points": [v(-6.4, -46.64) * mm, v(-6.15, -45.99) * mm, v(-5.94, -45.5) * mm, v(-5.77, -45.17) * mm]});
            skFitSpline(sketch, "E1027", {"points": [v(-6.5, -44.77) * mm, v(-5.87, -44.75) * mm, v(-5.01, -44.74) * mm, v(-3.93, -44.74) * mm]});
            skFitSpline(sketch, "E1028", {"points": [v(-3.14, -42.27) * mm, v(-4.2, -42.3) * mm, v(-5.44, -42.36) * mm, v(-6.85, -42.46) * mm]});
            skFitSpline(sketch, "E1029", {"points": [v(-6.85, -42.46) * mm, v(-8.19, -42.57) * mm, v(-9.3, -42.66) * mm, v(-10.2, -42.74) * mm]});
            skFitSpline(sketch, "E1030", {"points": [v(-10.93, -45.28) * mm, v(-9.69, -45.1) * mm, v(-8.75, -44.97) * mm, v(-8.14, -44.87) * mm]});
            skFitSpline(sketch, "E1031", {"points": [v(-8.14, -44.87) * mm, v(-8.53, -45.63) * mm, v(-8.81, -46.22) * mm, v(-8.99, -46.64) * mm]});
            skFitSpline(sketch, "E1032", {"points": [v(-8.99, -46.64) * mm, v(-9.72, -48.24) * mm, v(-10.26, -49.55) * mm, v(-10.6, -50.56) * mm]});
            skFitSpline(sketch, "E1033", {"points": [v(-10.6, -50.56) * mm, v(-10.82, -51.24) * mm, v(-10.96, -51.7) * mm, v(-11.02, -51.9) * mm]});
            skFitSpline(sketch, "E1034", {"points": [v(-11.32, -52.87) * mm, v(-11.71, -52.9) * mm, v(-12.03, -52.92) * mm, v(-12.28, -52.94) * mm]});
            skFitSpline(sketch, "E1035", {"points": [v(-2.46, -43.46) * mm, v(-2.32, -43.86) * mm, v(-2.24, -44.15) * mm, v(-2.24, -44.34) * mm]});
            skFitSpline(sketch, "E1036", {"points": [v(-2.24, -44.34) * mm, v(-2.24, -44.4) * mm, v(-2.26, -44.49) * mm, v(-2.3, -44.6) * mm]});
            skFitSpline(sketch, "E1037", {"points": [v(-2.3, -44.6) * mm, v(-2.85, -45.6) * mm, v(-3.28, -46.46) * mm, v(-3.59, -47.13) * mm]});
            skFitSpline(sketch, "E1038", {"points": [v(-3.59, -47.13) * mm, v(-4.3, -48.67) * mm, v(-4.83, -49.98) * mm, v(-5.19, -51.06) * mm]});
            skFitSpline(sketch, "E1039", {"points": [v(-5.19, -51.06) * mm, v(-5.65, -52.48) * mm, v(-6.07, -53.88) * mm, v(-6.45, -55.27) * mm]});
            skFitSpline(sketch, "E1040", {"points": [v(-3.24, -54.47) * mm, v(-3.13, -53.4) * mm, v(-2.82, -52.27) * mm, v(-2.32, -51.06) * mm]});
            skFitSpline(sketch, "E1041", {"points": [v(-1.2, -48.4) * mm, v(-1.12, -48.4) * mm, v(-1.02, -48.79) * mm, v(-0.9, -49.58) * mm]});
            skFitSpline(sketch, "E1042", {"points": [v(-0.9, -49.58) * mm, v(-0.6, -51.58) * mm, v(-0.45, -53.2) * mm, v(-0.45, -54.4) * mm]});
            skFitSpline(sketch, "E1043", {"points": [v(-0.45, -54.4) * mm, v(-0.45, -54.65) * mm, v(-0.47, -54.84) * mm, v(-0.5, -54.96) * mm]});
            skFitSpline(sketch, "E1044", {"points": [v(2.72, -54.17) * mm, v(3.18, -52.61) * mm, v(3.48, -51.58) * mm, v(3.65, -51.06) * mm]});
            skFitSpline(sketch, "E1045", {"points": [v(3.65, -51.06) * mm, v(4.23, -49.13) * mm, v(4.67, -47.82) * mm, v(4.97, -47.13) * mm]});
            skFitSpline(sketch, "E1046", {"points": [v(4.97, -47.13) * mm, v(5.8, -45.24) * mm, v(6.6, -43.6) * mm, v(7.36, -42.23) * mm]});
            skFitSpline(sketch, "E1047", {"points": [v(7.36, -42.23) * mm, v(6.53, -42.28) * mm, v(5.8, -42.34) * mm, v(5.16, -42.42) * mm]});
            skFitSpline(sketch, "E1048", {"points": [v(4.8, -42.45) * mm, v(3.56, -44.71) * mm, v(2.75, -46.27) * mm, v(2.39, -47.13) * mm]});
            skFitSpline(sketch, "E1049", {"points": [v(2.05, -47.96) * mm, v(1.83, -48.48) * mm, v(1.7, -48.74) * mm, v(1.67, -48.74) * mm]});
            skFitSpline(sketch, "E1050", {"points": [v(1.67, -48.74) * mm, v(1.4, -46.6) * mm, v(0.96, -44.31) * mm, v(0.34, -41.86) * mm]});
            skFitSpline(sketch, "E1051", {"points": [v(-2.77, -42.56) * mm, v(-2.75, -42.64) * mm, v(-2.65, -42.94) * mm, v(-2.46, -43.46) * mm]});
            skFitSpline(sketch, "E1052", {"points": [v(12.25, -51.69) * mm, v(11.6, -52.38) * mm, v(10.85, -52.72) * mm, v(10, -52.72) * mm]});
            skFitSpline(sketch, "E1053", {"points": [v(10, -52.72) * mm, v(9.21, -52.72) * mm, v(8.58, -52.4) * mm, v(8.08, -51.76) * mm]});
            skFitSpline(sketch, "E1054", {"points": [v(8.08, -51.76) * mm, v(7.6, -51.16) * mm, v(7.37, -50.44) * mm, v(7.37, -49.6) * mm]});
            skFitSpline(sketch, "E1055", {"points": [v(7.37, -49.6) * mm, v(7.37, -49.4) * mm, v(7.39, -49.18) * mm, v(7.43, -48.92) * mm]});
            skFitSpline(sketch, "E1056", {"points": [v(7.43, -48.92) * mm, v(7.59, -47.8) * mm, v(8, -46.89) * mm, v(8.66, -46.2) * mm]});
            skFitSpline(sketch, "E1057", {"points": [v(8.66, -46.2) * mm, v(9.37, -45.49) * mm, v(10.25, -45.13) * mm, v(11.3, -45.13) * mm]});
            skFitSpline(sketch, "E1058", {"points": [v(11.3, -45.13) * mm, v(12.34, -45.13) * mm, v(13.08, -45.6) * mm, v(13.51, -46.54) * mm]});
            skFitSpline(sketch, "E1059", {"points": [v(16.71, -44.9) * mm, v(15.7, -43.15) * mm, v(13.96, -42.27) * mm, v(11.51, -42.27) * mm]});
            skFitSpline(sketch, "E1060", {"points": [v(11.51, -42.27) * mm, v(9.89, -42.27) * mm, v(8.45, -42.9) * mm, v(7.18, -44.17) * mm]});
            skFitSpline(sketch, "E1061", {"points": [v(7.18, -44.17) * mm, v(5.95, -45.41) * mm, v(5.24, -46.9) * mm, v(5.05, -48.62) * mm]});
            skFitSpline(sketch, "E1062", {"points": [v(5.05, -48.62) * mm, v(5.02, -49) * mm, v(5, -49.37) * mm, v(5, -49.72) * mm]});
            skFitSpline(sketch, "E1063", {"points": [v(5, -49.72) * mm, v(5, -51.32) * mm, v(5.39, -52.62) * mm, v(6.15, -53.62) * mm]});
            skFitSpline(sketch, "E1064", {"points": [v(6.15, -53.62) * mm, v(6.99, -54.71) * mm, v(8.15, -55.25) * mm, v(9.64, -55.25) * mm]});
            skFitSpline(sketch, "E1065", {"points": [v(9.64, -55.25) * mm, v(11.48, -55.25) * mm, v(13, -54.6) * mm, v(14.17, -53.27) * mm]});
            skFitSpline(sketch, "E1066", {"points": [v(22.04, -42.46) * mm, v(20.46, -42.56) * mm, v(19.06, -42.65) * mm, v(17.83, -42.74) * mm]});
            skFitSpline(sketch, "E1067", {"points": [v(17.08, -45.28) * mm, v(18.45, -45.1) * mm, v(19.67, -44.97) * mm, v(20.75, -44.87) * mm]});
            skFitSpline(sketch, "E1068", {"points": [v(20.75, -44.87) * mm, v(20.35, -45.64) * mm, v(20.07, -46.23) * mm, v(19.9, -46.64) * mm]});
            skFitSpline(sketch, "E1069", {"points": [v(19.9, -46.64) * mm, v(19.15, -48.27) * mm, v(18.61, -49.58) * mm, v(18.29, -50.56) * mm]});
            skFitSpline(sketch, "E1070", {"points": [v(18.29, -50.56) * mm, v(17.75, -52.15) * mm, v(17.28, -53.73) * mm, v(16.86, -55.3) * mm]});
            skFitSpline(sketch, "E1071", {"points": [v(16.86, -55.3) * mm, v(18.18, -54.94) * mm, v(19.22, -54.69) * mm, v(19.98, -54.55) * mm]});
            skFitSpline(sketch, "E1072", {"points": [v(20.07, -54.51) * mm, v(20.5, -52.85) * mm, v(20.84, -51.53) * mm, v(21.13, -50.56) * mm]});
            skFitSpline(sketch, "E1073", {"points": [v(21.13, -50.56) * mm, v(21.9, -48) * mm, v(22.57, -46.21) * mm, v(23.12, -45.17) * mm]});
            skFitSpline(sketch, "E1074", {"points": [v(22.38, -44.77) * mm, v(23.1, -44.75) * mm, v(23.96, -44.74) * mm, v(24.96, -44.74) * mm]});
            skFitSpline(sketch, "E1075", {"points": [v(26.76, -42.27) * mm, v(24.58, -42.34) * mm, v(23, -42.4) * mm, v(22.04, -42.46) * mm]});
            skFitSpline(sketch, "E1076", {"points": [v(30.45, -42.46) * mm, v(28.82, -42.56) * mm, v(27.42, -42.65) * mm, v(26.25, -42.74) * mm]});
            skFitSpline(sketch, "E1077", {"points": [v(25.5, -45.28) * mm, v(26.02, -45.22) * mm, v(26.58, -45.15) * mm, v(27.18, -45.1) * mm]});
            skFitSpline(sketch, "E1078", {"points": [v(27.18, -45.1) * mm, v(26.9, -45.63) * mm, v(26.65, -46.14) * mm, v(26.42, -46.64) * mm]});
            skFitSpline(sketch, "E1079", {"points": [v(26.42, -46.64) * mm, v(25.83, -47.96) * mm, v(25.3, -49.27) * mm, v(24.83, -50.56) * mm]});
            skFitSpline(sketch, "E1080", {"points": [v(24.83, -50.56) * mm, v(24.56, -51.34) * mm, v(24.24, -52.34) * mm, v(23.89, -53.57) * mm]});
            skFitSpline(sketch, "E1081", {"points": [v(23.89, -53.57) * mm, v(23.6, -54.63) * mm, v(23.44, -55.2) * mm, v(23.44, -55.28) * mm]});
            skFitSpline(sketch, "E1082", {"points": [v(23.44, -55.3) * mm, v(25.86, -54.91) * mm, v(27.69, -54.71) * mm, v(28.93, -54.71) * mm]});
            skFitSpline(sketch, "E1083", {"points": [v(31.56, -52.27) * mm, v(29.6, -52.36) * mm, v(28.13, -52.43) * mm, v(27.15, -52.5) * mm]});
            skFitSpline(sketch, "E1084", {"points": [v(27.15, -52.5) * mm, v(27.46, -51.3) * mm, v(27.75, -50.33) * mm, v(28, -49.56) * mm]});
            skFitSpline(sketch, "E1085", {"points": [v(28.73, -47.36) * mm, v(28.84, -47.08) * mm, v(28.94, -46.84) * mm, v(29.04, -46.64) * mm]});
            skFitSpline(sketch, "E1086", {"points": [v(29.04, -46.64) * mm, v(29.37, -45.85) * mm, v(29.58, -45.36) * mm, v(29.66, -45.17) * mm]});
            skFitSpline(sketch, "E1087", {"points": [v(29.13, -44.87) * mm, v(30.16, -44.78) * mm, v(31.6, -44.74) * mm, v(33.42, -44.74) * mm]});
            skFitSpline(sketch, "E1088", {"points": [v(35.18, -42.27) * mm, v(33, -42.34) * mm, v(31.43, -42.4) * mm, v(30.45, -42.46) * mm]});
            skFitSpline(sketch, "E1089", {"points": [v(42.87, -45.44) * mm, v(42.87, -44.24) * mm, v(42.28, -43.4) * mm, v(41.1, -42.9) * mm]});
            skFitSpline(sketch, "E1090", {"points": [v(41.1, -42.9) * mm, v(40.56, -42.67) * mm, v(40.07, -42.51) * mm, v(39.62, -42.44) * mm]});
            skFitSpline(sketch, "E1091", {"points": [v(39.62, -42.44) * mm, v(39.5, -42.42) * mm, v(39.02, -42.38) * mm, v(38.18, -42.32) * mm]});
            skFitSpline(sketch, "E1092", {"points": [v(38.18, -42.32) * mm, v(37.88, -42.29) * mm, v(37.6, -42.27) * mm, v(37.37, -42.27) * mm]});
            skFitSpline(sketch, "E1093", {"points": [v(37.37, -42.27) * mm, v(36.31, -42.27) * mm, v(35.05, -42.38) * mm, v(33.6, -42.6) * mm]});
            skFitSpline(sketch, "E1094", {"points": [v(34.22, -45.5) * mm, v(34.4, -45.46) * mm, v(34.6, -45.4) * mm, v(34.84, -45.32) * mm]});
            skFitSpline(sketch, "E1095", {"points": [v(34.84, -45.32) * mm, v(34.56, -45.87) * mm, v(34.35, -46.3) * mm, v(34.2, -46.61) * mm]});
            skFitSpline(sketch, "E1096", {"points": [v(34.2, -46.61) * mm, v(33.48, -48.2) * mm, v(32.94, -49.5) * mm, v(32.6, -50.53) * mm]});
            skFitSpline(sketch, "E1097", {"points": [v(32.6, -50.53) * mm, v(32.05, -52.16) * mm, v(31.58, -53.73) * mm, v(31.19, -55.25) * mm]});
            skFitSpline(sketch, "E1098", {"points": [v(31.19, -55.25) * mm, v(32.36, -54.94) * mm, v(33.4, -54.69) * mm, v(34.3, -54.51) * mm]});
            skFitSpline(sketch, "E1099", {"points": [v(34.4, -54.5) * mm, v(34.91, -52.5) * mm, v(35.27, -51.17) * mm, v(35.46, -50.53) * mm]});
            skFitSpline(sketch, "E1100", {"points": [v(36.18, -50.01) * mm, v(37.59, -51.65) * mm, v(38.7, -53.32) * mm, v(39.55, -55.03) * mm]});
            skFitSpline(sketch, "E1101", {"points": [v(42.47, -53.97) * mm, v(41.6, -52.52) * mm, v(40.5, -51.07) * mm, v(39.18, -49.63) * mm]});
            skFitSpline(sketch, "E1102", {"points": [v(39.18, -49.63) * mm, v(41.24, -49.15) * mm, v(42.45, -47.97) * mm, v(42.8, -46.09) * mm]});
            skFitSpline(sketch, "E1103", {"points": [v(42.8, -46.09) * mm, v(42.85, -45.82) * mm, v(42.87, -45.6) * mm, v(42.87, -45.44) * mm]});
            skFitSpline(sketch, "E1104", {"points": [v(39.1, -47.18) * mm, v(38.57, -47.37) * mm, v(37.93, -47.48) * mm, v(37.18, -47.5) * mm]});
            skFitSpline(sketch, "E1105", {"points": [v(36.45, -47.52) * mm, v(36.66, -46.95) * mm, v(36.77, -46.65) * mm, v(36.79, -46.61) * mm]});
            skFitSpline(sketch, "E1106", {"points": [v(36.79, -46.61) * mm, v(37, -46.09) * mm, v(37.22, -45.64) * mm, v(37.42, -45.28) * mm]});
            skFitSpline(sketch, "E1107", {"points": [v(36.82, -44.97) * mm, v(37.41, -44.8) * mm, v(37.88, -44.71) * mm, v(38.24, -44.7) * mm]});
            skFitSpline(sketch, "E1108", {"points": [v(38.46, -44.7) * mm, v(38.85, -44.7) * mm, v(39.14, -44.73) * mm, v(39.32, -44.8) * mm]});
            skFitSpline(sketch, "E1109", {"points": [v(39.32, -44.8) * mm, v(39.92, -45.02) * mm, v(40.22, -45.36) * mm, v(40.22, -45.8) * mm]});
            skFitSpline(sketch, "E1110", {"points": [v(40.22, -45.8) * mm, v(40.22, -46.42) * mm, v(39.84, -46.88) * mm, v(39.1, -47.18) * mm]});
            skFitSpline(sketch, "E1111", {"points": [v(37.6, -4.75) * mm, v(38.3, -4.76) * mm, v(38.99, -4.78) * mm, v(39.69, -4.79) * mm]});
            skFitSpline(sketch, "E1112", {"points": [v(39.69, -4.79) * mm, v(39.91, -4.8) * mm, v(40.13, -4.79) * mm, v(40.38, -4.88) * mm]});
            skFitSpline(sketch, "E1113", {"points": [v(40.38, -4.88) * mm, v(40.26, -4.93) * mm, v(40.15, -5) * mm, v(40.02, -5.05) * mm]});
            skFitSpline(sketch, "E1114", {"points": [v(40.02, -5.05) * mm, v(37.5, -6.16) * mm, v(35.08, -7.44) * mm, v(32.93, -9.2) * mm]});
            skFitSpline(sketch, "E1115", {"points": [v(32.93, -9.2) * mm, v(31.94, -10) * mm, v(31.04, -10.89) * mm, v(30.29, -11.92) * mm]});
            skFitSpline(sketch, "E1116", {"points": [v(30.29, -11.92) * mm, v(28.27, -14.7) * mm, v(27.9, -17.7) * mm, v(29.14, -20.9) * mm]});
            skFitSpline(sketch, "E1117", {"points": [v(29.14, -20.9) * mm, v(29.21, -21.07) * mm, v(29.29, -21.25) * mm, v(29.38, -21.5) * mm]});
            skFitSpline(sketch, "E1118", {"points": [v(29.38, -21.5) * mm, v(28.72, -21.37) * mm, v(28.12, -21.23) * mm, v(27.51, -21.14) * mm]});
            skFitSpline(sketch, "E1119", {"points": [v(27.51, -21.14) * mm, v(20.29, -20.01) * mm, v(13.42, -21.07) * mm, v(7, -24.63) * mm]});
            skFitSpline(sketch, "E1120", {"points": [v(7, -24.63) * mm, v(4.82, -25.84) * mm, v(2.9, -27.38) * mm, v(1.47, -29.47) * mm]});
            skFitSpline(sketch, "E1121", {"points": [v(1.47, -29.47) * mm, v(1.12, -29.99) * mm, v(0.8, -30.55) * mm, v(0.56, -31.13) * mm]});
            skFitSpline(sketch, "E1122", {"points": [v(0.56, -31.13) * mm, v(0.31, -31.7) * mm, v(0.17, -32.3) * mm, v(-0.02, -32.92) * mm]});
            skFitSpline(sketch, "E1123", {"points": [v(-0.02, -32.92) * mm, v(-0.06, -32.75) * mm, v(-0.1, -32.6) * mm, v(-0.14, -32.44) * mm]});
            skFitSpline(sketch, "E1124", {"points": [v(-0.14, -32.44) * mm, v(-0.59, -30.5) * mm, v(-1.69, -28.93) * mm, v(-3.09, -27.55) * mm]});
            skFitSpline(sketch, "E1125", {"points": [v(-3.09, -27.55) * mm, v(-5.36, -25.33) * mm, v(-8.08, -23.84) * mm, v(-11.03, -22.74) * mm]});
            skFitSpline(sketch, "E1126", {"points": [v(-11.03, -22.74) * mm, v(-15.71, -20.99) * mm, v(-20.55, -20.37) * mm, v(-25.52, -20.87) * mm]});
            skFitSpline(sketch, "E1127", {"points": [v(-25.52, -20.87) * mm, v(-26.68, -20.98) * mm, v(-27.82, -21.23) * mm, v(-28.97, -21.42) * mm]});
            skFitSpline(sketch, "E1128", {"points": [v(-28.97, -21.42) * mm, v(-29.1, -21.44) * mm, v(-29.21, -21.46) * mm, v(-29.3, -21.48) * mm]});
            skFitSpline(sketch, "E1129", {"points": [v(-29.3, -21.48) * mm, v(-29.06, -20.58) * mm, v(-28.74, -19.72) * mm, v(-28.58, -18.83) * mm]});
            skFitSpline(sketch, "E1130", {"points": [v(-28.58, -18.83) * mm, v(-28.13, -16.39) * mm, v(-28.73, -14.17) * mm, v(-30.14, -12.15) * mm]});
            skFitSpline(sketch, "E1131", {"points": [v(-30.14, -12.15) * mm, v(-31.43, -10.3) * mm, v(-33.1, -8.86) * mm, v(-35, -7.72) * mm]});
            skFitSpline(sketch, "E1132", {"points": [v(-35, -7.72) * mm, v(-36.62, -6.75) * mm, v(-38.33, -5.94) * mm, v(-40, -5.06) * mm]});
            skFitSpline(sketch, "E1133", {"points": [v(-40, -5.06) * mm, v(-40.13, -5) * mm, v(-40.26, -4.94) * mm, v(-40.38, -4.88) * mm]});
            skFitSpline(sketch, "E1134", {"points": [v(-40.38, -4.88) * mm, v(-40.38, -4.84) * mm, v(-40.38, -4.8) * mm, v(-40.38, -4.75) * mm]});
            skFitSpline(sketch, "E1135", {"points": [v(-40.38, -4.75) * mm, v(-39.45, -4.75) * mm, v(-38.53, -4.75) * mm, v(-37.6, -4.75) * mm]});
            skFitSpline(sketch, "E1136", {"points": [v(-37.6, -4.75) * mm, v(-29.52, -4.75) * mm, v(-21.43, -4.75) * mm, v(-13.33, -4.75) * mm]});
            skFitSpline(sketch, "E1137", {"points": [v(-13.33, -4.75) * mm, v(-13.25, -5.01) * mm, v(-13.18, -5.28) * mm, v(-13.09, -5.54) * mm]});
            skFitSpline(sketch, "E1138", {"points": [v(-13.09, -5.54) * mm, v(-12.75, -6.54) * mm, v(-12.45, -7.55) * mm, v(-12.05, -8.53) * mm]});
            skFitSpline(sketch, "E1139", {"points": [v(-12.05, -8.53) * mm, v(-11.5, -9.85) * mm, v(-10.47, -10.7) * mm, v(-9.06, -10.92) * mm]});
            skFitSpline(sketch, "E1140", {"points": [v(-9.06, -10.92) * mm, v(-7.22, -11.22) * mm, v(-5.37, -11.42) * mm, v(-3.53, -11.65) * mm]});
            skFitSpline(sketch, "E1141", {"points": [v(-3.53, -11.65) * mm, v(-3.43, -11.66) * mm, v(-3.28, -11.6) * mm, v(-3.24, -11.53) * mm]});
            skFitSpline(sketch, "E1142", {"points": [v(-3.24, -11.53) * mm, v(-2.95, -11.07) * mm, v(-2.67, -10.62) * mm, v(-2.63, -10.05) * mm]});
            skFitSpline(sketch, "E1143", {"points": [v(-2.63, -10.05) * mm, v(-2.58, -9.24) * mm, v(-2.46, -8.44) * mm, v(-2.37, -7.64) * mm]});
            skFitSpline(sketch, "E1144", {"points": [v(-2.37, -7.64) * mm, v(-2.32, -7.16) * mm, v(-2.25, -6.67) * mm, v(-2.2, -6.19) * mm]});
            skFitSpline(sketch, "E1145", {"points": [v(-2.11, -6.19) * mm, v(-1.89, -7.08) * mm, v(-1.67, -7.97) * mm, v(-1.43, -8.92) * mm]});
            skFitSpline(sketch, "E1146", {"points": [v(-1.43, -8.92) * mm, v(-0.46, -8.49) * mm, v(0.48, -8.53) * mm, v(1.42, -8.9) * mm]});
            skFitSpline(sketch, "E1147", {"points": [v(1.42, -8.9) * mm, v(1.66, -7.94) * mm, v(1.88, -7.06) * mm, v(2.1, -6.18) * mm]});
            skFitSpline(sketch, "E1148", {"points": [v(2.1, -6.18) * mm, v(2.3, -7.19) * mm, v(2.42, -8.18) * mm, v(2.53, -9.18) * mm]});
            skFitSpline(sketch, "E1149", {"points": [v(2.53, -9.18) * mm, v(2.63, -9.96) * mm, v(2.63, -10.76) * mm, v(3.15, -11.43) * mm]});
            skFitSpline(sketch, "E1150", {"points": [v(3.15, -11.43) * mm, v(3.28, -11.6) * mm, v(3.38, -11.68) * mm, v(3.6, -11.66) * mm]});
            skFitSpline(sketch, "E1151", {"points": [v(3.6, -11.66) * mm, v(4.17, -11.59) * mm, v(4.75, -11.54) * mm, v(5.33, -11.48) * mm]});
            skFitSpline(sketch, "E1152", {"points": [v(5.33, -11.48) * mm, v(6.76, -11.33) * mm, v(8.2, -11.23) * mm, v(9.58, -10.78) * mm]});
            skFitSpline(sketch, "E1153", {"points": [v(9.58, -10.78) * mm, v(10.53, -10.47) * mm, v(11.29, -9.93) * mm, v(11.75, -9.05) * mm]});
            skFitSpline(sketch, "E1154", {"points": [v(11.75, -9.05) * mm, v(12.07, -8.44) * mm, v(12.37, -7.82) * mm, v(12.6, -7.17) * mm]});
            skFitSpline(sketch, "E1155", {"points": [v(12.6, -7.17) * mm, v(12.88, -6.38) * mm, v(13.08, -5.56) * mm, v(13.32, -4.75) * mm]});
            skFitSpline(sketch, "E1156", {"points": [v(13.32, -4.75) * mm, v(21.41, -4.75) * mm, v(29.5, -4.75) * mm, v(37.6, -4.75) * mm]});
            skSolve(sketch);
        }
        {
            var Q0;
            Q0 = qSketchRegion(id + "F5", true);
            extrude(context, id + "F6", {"entities" : qUnion([Q0]), "operationType" : NewBodyOperationType.ADD, "depth" : 1 * mm, "offsetDistance" : 25 * mm});
        }
        {
            var Q0;
            Q0=makeQuery(id+"F6.opExtrude","CAP_FACE",FACE,{"disambiguationData":[OSD([sQuery(id+"F5.wireOp",EDGE,"E798"),sQuery(id+"F5.wireOp",EDGE,"E799"),sQuery(id+"F5.wireOp",EDGE,"E800"),sQuery(id+"F5.wireOp",EDGE,"E801"),sQuery(id+"F5.wireOp",EDGE,"E802"),sQuery(id+"F5.wireOp",EDGE,"E803"),sQuery(id+"F5.wireOp",EDGE,"E804"),sQuery(id+"F5.wireOp",EDGE,"E863"),sQuery(id+"F5.wireOp",EDGE,"E864"),sQuery(id+"F5.wireOp",EDGE,"E865"),sQuery(id+"F5.wireOp",EDGE,"E866"),sQuery(id+"F5.wireOp",EDGE,"E867"),sQuery(id+"F5.wireOp",EDGE,"E868"),sQuery(id+"F5.wireOp",EDGE,"E869"),sQuery(id+"F5.wireOp",EDGE,"E870"),sQuery(id+"F5.wireOp",EDGE,"E871"),sQuery(id+"F5.wireOp",EDGE,"E872"),sQuery(id+"F5.wireOp",EDGE,"E873"),sQuery(id+"F5.wireOp",EDGE,"E874"),sQuery(id+"F5.wireOp",EDGE,"E875"),sQuery(id+"F5.wireOp",EDGE,"E876"),sQuery(id+"F5.wireOp",EDGE,"E877"),sQuery(id+"F5.wireOp",EDGE,"E878"),sQuery(id+"F5.wireOp",EDGE,"E879"),sQuery(id+"F5.wireOp",EDGE,"E880"),sQuery(id+"F5.wireOp",EDGE,"E881"),sQuery(id+"F5.wireOp",EDGE,"E882"),sQuery(id+"F5.wireOp",EDGE,"E883"),sQuery(id+"F5.wireOp",EDGE,"E884"),sQuery(id+"F5.wireOp",EDGE,"E885"),sQuery(id+"F5.wireOp",EDGE,"E886"),sQuery(id+"F5.wireOp",EDGE,"E887"),sQuery(id+"F5.wireOp",EDGE,"E888"),sQuery(id+"F5.wireOp",EDGE,"E889"),sQuery(id+"F5.wireOp",EDGE,"E890"),sQuery(id+"F5.wireOp",EDGE,"E891"),sQuery(id+"F5.wireOp",EDGE,"E892"),sQuery(id+"F5.wireOp",EDGE,"E893"),sQuery(id+"F5.wireOp",EDGE,"E894"),sQuery(id+"F5.wireOp",EDGE,"E895"),sQuery(id+"F5.wireOp",EDGE,"E896"),sQuery(id+"F5.wireOp",EDGE,"E897"),sQuery(id+"F5.wireOp",EDGE,"E898"),sQuery(id+"F5.wireOp",EDGE,"E899"),sQuery(id+"F5.wireOp",EDGE,"E900"),sQuery(id+"F5.wireOp",EDGE,"E901"),sQuery(id+"F5.wireOp",EDGE,"E902"),sQuery(id+"F5.wireOp",EDGE,"E903"),sQuery(id+"F5.wireOp",EDGE,"E904"),sQuery(id+"F5.wireOp",EDGE,"E905"),sQuery(id+"F5.wireOp",EDGE,"E906"),sQuery(id+"F5.wireOp",EDGE,"E907"),sQuery(id+"F5.wireOp",EDGE,"E908"),sQuery(id+"F5.wireOp",EDGE,"E909"),sQuery(id+"F5.wireOp",EDGE,"E910"),sQuery(id+"F5.wireOp",EDGE,"E911"),sQuery(id+"F5.wireOp",EDGE,"E912"),sQuery(id+"F5.wireOp",EDGE,"E913"),sQuery(id+"F5.wireOp",EDGE,"E914"),sQuery(id+"F5.wireOp",EDGE,"E915"),sQuery(id+"F5.wireOp",EDGE,"E916"),sQuery(id+"F5.wireOp",EDGE,"E917"),sQuery(id+"F5.wireOp",EDGE,"E918"),sQuery(id+"F5.wireOp",EDGE,"E919"),sQuery(id+"F5.wireOp",EDGE,"E920"),sQuery(id+"F5.wireOp",EDGE,"E921"),sQuery(id+"F5.wireOp",EDGE,"E922"),sQuery(id+"F5.wireOp",EDGE,"E923"),sQuery(id+"F5.wireOp",EDGE,"E924"),sQuery(id+"F5.wireOp",EDGE,"E925"),sQuery(id+"F5.wireOp",EDGE,"E926"),sQuery(id+"F5.wireOp",EDGE,"E927"),sQuery(id+"F5.wireOp",EDGE,"E928"),sQuery(id+"F5.wireOp",EDGE,"E929"),sQuery(id+"F5.wireOp",EDGE,"E930"),sQuery(id+"F5.wireOp",EDGE,"E931"),sQuery(id+"F5.wireOp",EDGE,"E932"),sQuery(id+"F5.wireOp",EDGE,"E933"),sQuery(id+"F5.wireOp",EDGE,"E934"),sQuery(id+"F5.wireOp",EDGE,"E935"),sQuery(id+"F5.wireOp",EDGE,"E936"),sQuery(id+"F5.wireOp",EDGE,"E937"),sQuery(id+"F5.wireOp",EDGE,"E938"),sQuery(id+"F5.wireOp",EDGE,"E939"),sQuery(id+"F5.wireOp",EDGE,"E940"),sQuery(id+"F5.wireOp",EDGE,"E941"),sQuery(id+"F5.wireOp",EDGE,"E942"),sQuery(id+"F5.wireOp",EDGE,"E943"),sQuery(id+"F5.wireOp",EDGE,"E944"),sQuery(id+"F5.wireOp",EDGE,"E945"),sQuery(id+"F5.wireOp",EDGE,"E946"),sQuery(id+"F5.wireOp",EDGE,"E947"),sQuery(id+"F5.wireOp",EDGE,"E948"),sQuery(id+"F5.wireOp",EDGE,"E949"),sQuery(id+"F5.wireOp",EDGE,"E950"),sQuery(id+"F5.wireOp",EDGE,"E951"),sQuery(id+"F5.wireOp",EDGE,"E952"),sQuery(id+"F5.wireOp",EDGE,"E953"),sQuery(id+"F5.wireOp",EDGE,"E954"),sQuery(id+"F5.wireOp",EDGE,"E955"),sQuery(id+"F5.wireOp",EDGE,"E956"),sQuery(id+"F5.wireOp",EDGE,"E957"),sQuery(id+"F5.wireOp",EDGE,"E958"),sQuery(id+"F5.wireOp",EDGE,"E959"),sQuery(id+"F5.wireOp",EDGE,"E960"),sQuery(id+"F5.wireOp",EDGE,"E961"),sQuery(id+"F5.wireOp",EDGE,"E962"),sQuery(id+"F5.wireOp",EDGE,"E963"),sQuery(id+"F5.wireOp",EDGE,"E964"),sQuery(id+"F5.wireOp",EDGE,"E965"),sQuery(id+"F5.wireOp",EDGE,"E966"),sQuery(id+"F5.wireOp",EDGE,"E967"),sQuery(id+"F5.wireOp",EDGE,"E968"),sQuery(id+"F5.wireOp",EDGE,"E969"),sQuery(id+"F5.wireOp",EDGE,"E970")])],"isStart":false});
            var sketch = newSketch(context, id + "F7", { "sketchPlane" : qUnion([Q0])});
            skLineSegment(sketch, "E1157", {"start": v(-19.8, 54.8) * mm, "end": v(11.46, 54.85) * mm});
            skLineSegment(sketch, "E1158", {"start": v(22.62, 54.86) * mm, "end": v(26.38, 54.86) * mm});
            skLineSegment(sketch, "E1159", {"start": v(26.38, 54.86) * mm, "end": v(27.64, 53.63) * mm});
            skLineSegment(sketch, "E1160", {"start": v(34.39, 40.32) * mm, "end": v(32.73, 38.61) * mm});
            skLineSegment(sketch, "E1161", {"start": v(28.04, 33.92) * mm, "end": v(9.46, 15.2) * mm});
            skLineSegment(sketch, "E1162", {"start": v(-10.99, 16.65) * mm, "end": v(-16.2, 22.18) * mm});
            skLineSegment(sketch, "E1163", {"start": v(-20.74, 26.75) * mm, "end": v(-32.33, 38.38) * mm});
            skSolve(sketch);
        }
        {
            var Q0;
            Q0=makeQuery(id+"F7.imprint","IMPRINT",FACE,{"disambiguationData":[TD([[makeQuery(id+"F7.imprint","IMPRINT",EDGE,{"derivedFrom":sQuery(id+"F7.wireOp",EDGE,"E1157")}),1.0]])]});
            extrude(context, id + "F8", {"entities" : qUnion([Q0]), "operationType" : NewBodyOperationType.ADD, "depth" : 1 * mm, "offsetDistance" : 25 * mm});
        }
    });
